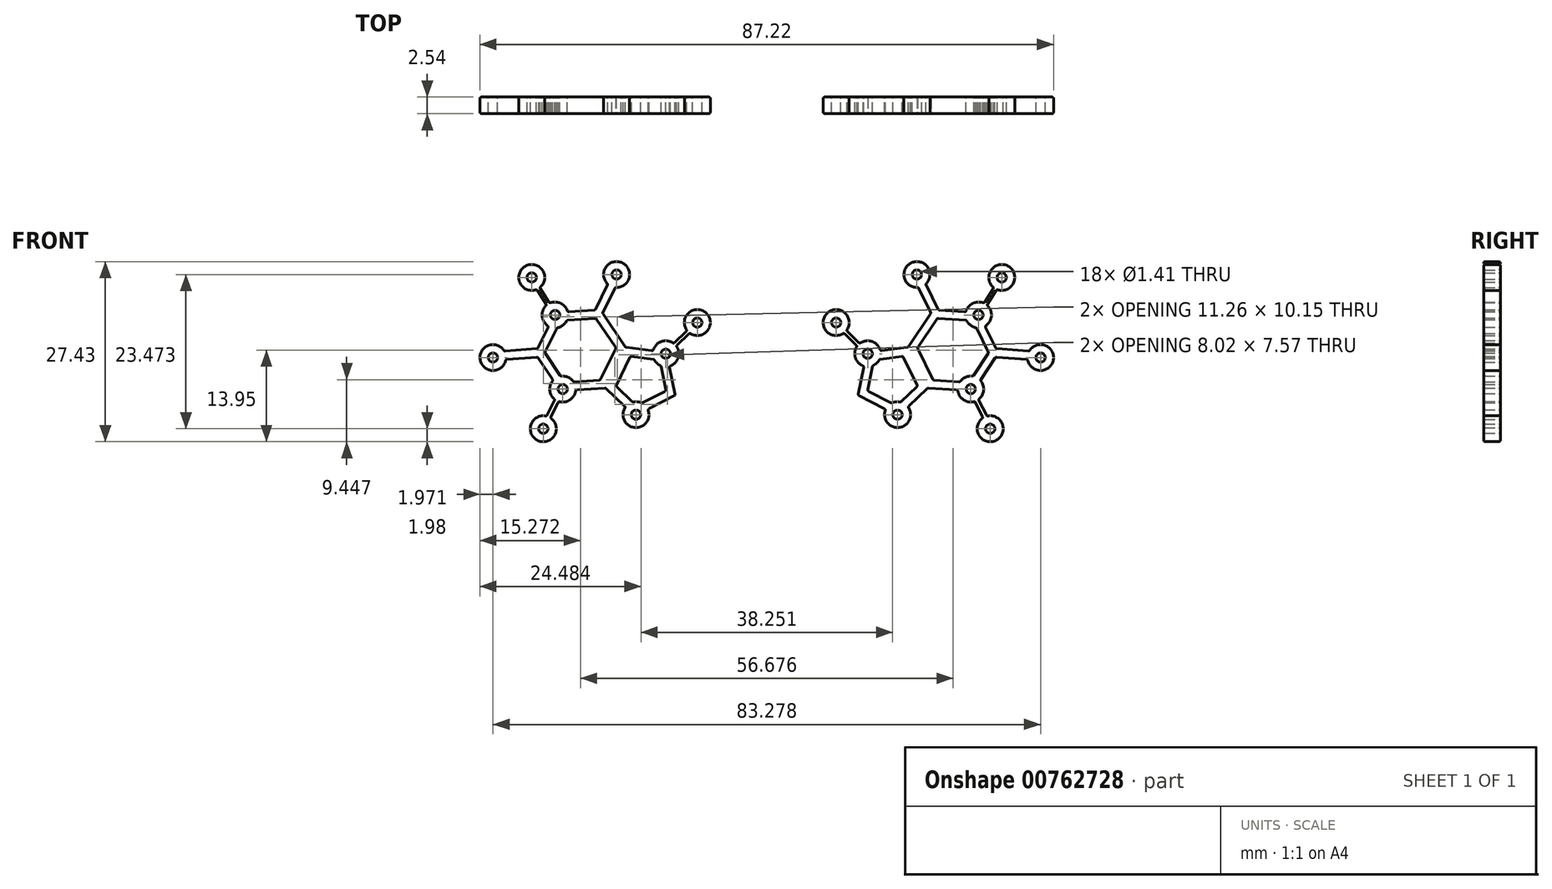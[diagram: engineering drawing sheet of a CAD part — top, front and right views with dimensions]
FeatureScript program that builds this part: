
annotation { "Feature Type Name" : "Feature", "Feature Type Description" : "" }
export const myFeature = defineFeature(function(context is Context, id is Id, definition is map)
    precondition{}
    {
        {
            var Q0;
            Q0=qCreatedBy(makeId("Front.planeOp"),FACE);
            var sketch = newSketch(context, id + "F0", { "sketchPlane" : qUnion([Q0])});
            skLineSegment(sketch, "E0.1", {"start": v(-24.49, 20.36) * mm, "end": v(-29.05, 20.05) * mm});
            skLineSegment(sketch, "E0.2", {"start": v(-32.47, 21.54) * mm, "end": v(-34.85, 25.07) * mm});
            skLineSegment(sketch, "E0.3", {"start": v(-34.85, 26.35) * mm, "end": v(-33.18, 29.77) * mm});
            skLineSegment(sketch, "E0.4", {"start": v(-30.27, 31.94) * mm, "end": v(-26.12, 32.22) * mm});
            skLineSegment(sketch, "E0.5", {"start": v(-24.98, 31.78) * mm, "end": v(-21.46, 26.56) * mm});
            skPoint(sketch, "E0.0.midPoint", {"position": v(-22.97, 23.46) * mm});
            skLineSegment(sketch, "E1", {"start": v(-24.49, 20.36) * mm, "end": v(-21.46, 17.5) * mm});
            skLineSegment(sketch, "E2", {"start": v(-21.46, 26.56) * mm, "end": v(-17.28, 26.01) * mm});
            skLineSegment(sketch, "E3", {"start": v(-14.8, 23.68) * mm, "end": v(-13.9, 19.26) * mm});
            skLineSegment(sketch, "E4", {"start": v(-13.9, 19.26) * mm, "end": v(-18.09, 17.1) * mm});
            skPoint(sketch, "E5.third.point", {"position": v(-19.84, 14.33) * mm});
            skArc(sketch, "E6", {"start": v(-14.8, 23.68) * mm, "mid": v(-13.48, 24.95) * mm, "end": v(-13.77, 26.75) * mm});
            skArc(sketch, "E7", {"start": v(-33.48, 16.07) * mm, "mid": v(-34.78, 12.35) * mm, "end": v(-32.9, 15.81) * mm});
            skArc(sketch, "E8", {"start": v(-39.92, 25.97) * mm, "mid": v(-43.58, 24.63) * mm, "end": v(-39.69, 24.7) * mm});
            skArc(sketch, "E9", {"start": v(-30.27, 31.94) * mm, "mid": v(-33.37, 33.06) * mm, "end": v(-33.18, 29.77) * mm});
            skArc(sketch, "E10", {"start": v(-23.05, 35.67) * mm, "mid": v(-22.02, 39.43) * mm, "end": v(-24.16, 36.17) * mm});
            skArc(sketch, "E11", {"start": v(-34.55, 35.6) * mm, "mid": v(-36.71, 38.9) * mm, "end": v(-35, 35.36) * mm});
            skArc(sketch, "E12", {"start": v(-11.72, 28.73) * mm, "mid": v(-9.19, 31.75) * mm, "end": v(-12.1, 29.1) * mm});
            skLineSegment(sketch, "E13", {"start": v(-26.12, 32.22) * mm, "end": v(-24.16, 36.17) * mm});
            skLineSegment(sketch, "E14", {"start": v(-23.05, 35.67) * mm, "end": v(-24.98, 31.78) * mm});
            skLineSegment(sketch, "E15", {"start": v(-39.92, 25.97) * mm, "end": v(-34.85, 26.35) * mm});
            skLineSegment(sketch, "E16", {"start": v(-39.69, 24.7) * mm, "end": v(-34.85, 25.07) * mm});
            skLineSegment(sketch, "E17", {"start": v(-33.48, 16.07) * mm, "end": v(-32.2, 18.6) * mm});
            skLineSegment(sketch, "E18", {"start": v(-32.9, 15.81) * mm, "end": v(-31.67, 18.33) * mm});
            skLineSegment(sketch, "E19", {"start": v(-35, 35.36) * mm, "end": v(-33.47, 32.97) * mm});
            skLineSegment(sketch, "E20", {"start": v(-34.55, 35.6) * mm, "end": v(-33.02, 33.27) * mm});
            skLineSegment(sketch, "E21", {"start": v(-14.15, 27.14) * mm, "end": v(-12.1, 29.1) * mm});
            skLineSegment(sketch, "E22", {"start": v(-13.77, 26.75) * mm, "end": v(-11.72, 28.73) * mm});
            skPoint(sketch, "E23.orphan", {"position": v(-25.3, 32.28) * mm});
            skArc(sketch, "E24.trimOffspring", {"start": v(-31.67, 18.33) * mm, "mid": v(-29.94, 18.55) * mm, "end": v(-29.05, 20.05) * mm});
            skPoint(sketch, "E25.orphan", {"position": v(-32.19, 31.8) * mm});
            skCircle(sketch, "E26", {"center": v(-41.64, 25) * mm, "radius": 0.7 * mm});
            skCircle(sketch, "E27", {"center": v(-33.98, 14.16) * mm, "radius": 0.7 * mm});
            skCircle(sketch, "E28", {"center": v(-31.02, 20.2) * mm, "radius": 0.7 * mm});
            skCircle(sketch, "E29", {"center": v(-19.89, 16.3) * mm, "radius": 0.7 * mm});
            skCircle(sketch, "E30", {"center": v(-15.36, 25.58) * mm, "radius": 0.7 * mm});
            skCircle(sketch, "E31", {"center": v(-10.56, 30.32) * mm, "radius": 0.7 * mm});
            skCircle(sketch, "E32", {"center": v(-22.83, 37.63) * mm, "radius": 0.7 * mm});
            skCircle(sketch, "E33", {"center": v(-35.74, 37.18) * mm, "radius": 0.7 * mm});
            skCircle(sketch, "E34", {"center": v(-32.19, 31.47) * mm, "radius": 0.7 * mm});
            skLineSegment(sketch, "E35.0", {"start": v(-33.71, 25.8) * mm, "end": v(-32.04, 29.21) * mm});
            skLineSegment(sketch, "E36.0", {"start": v(-29.72, 30.7) * mm, "end": v(-26.03, 30.96) * mm});
            skLineSegment(sketch, "E37.0", {"start": v(-25.95, 30.96) * mm, "end": v(-22.92, 26.46) * mm});
            skLineSegment(sketch, "E38.0", {"start": v(-22.92, 26.46) * mm, "end": v(-25.3, 21.58) * mm});
            skLineSegment(sketch, "E39.0", {"start": v(-25.3, 21.58) * mm, "end": v(-29.14, 21.32) * mm});
            skLineSegment(sketch, "E40.0", {"start": v(-31.42, 22.24) * mm, "end": v(-33.75, 25.71) * mm});
            skLineSegment(sketch, "E41", {"start": v(-32.04, 29.21) * mm, "end": v(-31.9, 29.52) * mm});
            skLineSegment(sketch, "E42", {"start": v(-29.72, 30.7) * mm, "end": v(-30.4, 30.66) * mm});
            skLineSegment(sketch, "E43", {"start": v(-26.03, 30.96) * mm, "end": v(-25.95, 30.96) * mm});
            skLineSegment(sketch, "E44", {"start": v(-33.71, 25.8) * mm, "end": v(-33.75, 25.71) * mm});
            skLineSegment(sketch, "E45", {"start": v(-31.42, 22.24) * mm, "end": v(-31.35, 22.14) * mm});
            skLineSegment(sketch, "E46", {"start": v(-29.14, 21.32) * mm, "end": v(-29.39, 21.3) * mm});
            skLineSegment(sketch, "E47.0", {"start": v(-20.72, 25.18) * mm, "end": v(-22.94, 20.64) * mm});
            skLineSegment(sketch, "E48.0", {"start": v(-22.94, 20.64) * mm, "end": v(-20.59, 18.41) * mm});
            skLineSegment(sketch, "E49.0", {"start": v(-15.34, 19.95) * mm, "end": v(-18.67, 18.24) * mm});
            skLineSegment(sketch, "E50.0", {"start": v(-16.07, 23.53) * mm, "end": v(-15.34, 19.95) * mm});
            skLineSegment(sketch, "E51.0", {"start": v(-20.72, 25.18) * mm, "end": v(-17.44, 24.75) * mm});
            skLineSegment(sketch, "E52", {"start": v(-20.59, 18.41) * mm, "end": v(-20.38, 18.21) * mm});
            skLineSegment(sketch, "E53", {"start": v(-18.67, 18.24) * mm, "end": v(-19, 18.06) * mm});
            skLineSegment(sketch, "E54", {"start": v(-17.44, 24.75) * mm, "end": v(-17.13, 24.71) * mm});
            skArc(sketch, "E55.trimOffspring", {"start": v(-31.9, 29.52) * mm, "mid": v(-31, 29.9) * mm, "end": v(-30.4, 30.66) * mm});
            skArc(sketch, "E56", {"start": v(-29.39, 21.3) * mm, "mid": v(-30.25, 22.01) * mm, "end": v(-31.35, 22.14) * mm});
            skArc(sketch, "E57.trimOffspring", {"start": v(-32.47, 21.54) * mm, "mid": v(-33, 20.01) * mm, "end": v(-32.2, 18.6) * mm});
            skArc(sketch, "E58", {"start": v(-17.13, 24.71) * mm, "mid": v(-16.71, 24.14) * mm, "end": v(-16.11, 23.75) * mm});
            skLineSegment(sketch, "E59", {"start": v(-16.07, 23.53) * mm, "end": v(-16.11, 23.75) * mm});
            skArc(sketch, "E60", {"start": v(-21.46, 17.5) * mm, "mid": v(-20.11, 14.34) * mm, "end": v(-18.09, 17.1) * mm});
            skArc(sketch, "E61.trimOffspring", {"start": v(-19, 18.06) * mm, "mid": v(-19.68, 18.26) * mm, "end": v(-20.38, 18.21) * mm});
            skArc(sketch, "E62.trimOffspring", {"start": v(-14.15, 27.14) * mm, "mid": v(-16.02, 27.44) * mm, "end": v(-17.28, 26.01) * mm});
            skCircle(sketch, "E63.MirrorC", {"center": v(19.89, 16.3) * mm, "radius": 0.7 * mm});
            skLineSegment(sketch, "E64.MirrorCS", {"start": v(31.42, 22.24) * mm, "end": v(31.35, 22.14) * mm});
            skArc(sketch, "E65.MirrorCS", {"start": v(19, 18.06) * mm, "mid": v(19.68, 18.26) * mm, "end": v(20.38, 18.21) * mm});
            skLineSegment(sketch, "E66.MirrorCS", {"start": v(33.71, 25.8) * mm, "end": v(33.75, 25.71) * mm});
            skLineSegment(sketch, "E67.MirrorCS", {"start": v(20.59, 18.41) * mm, "end": v(20.38, 18.21) * mm});
            skLineSegment(sketch, "E68.MirrorCS", {"start": v(29.72, 30.7) * mm, "end": v(30.4, 30.66) * mm});
            skLineSegment(sketch, "E69.MirrorCS", {"start": v(32.04, 29.21) * mm, "end": v(31.9, 29.52) * mm});
            skLineSegment(sketch, "E70.MirrorCS", {"start": v(18.67, 18.24) * mm, "end": v(19, 18.06) * mm});
            skLineSegment(sketch, "E71.MirrorCS", {"start": v(29.14, 21.32) * mm, "end": v(29.39, 21.3) * mm});
            skLineSegment(sketch, "E72.MirrorCS", {"start": v(26.03, 30.96) * mm, "end": v(25.95, 30.96) * mm});
            skLineSegment(sketch, "E73.MirrorCS", {"start": v(17.44, 24.75) * mm, "end": v(17.13, 24.71) * mm});
            skArc(sketch, "E74.MirrorCS", {"start": v(30.27, 31.94) * mm, "mid": v(33.37, 33.06) * mm, "end": v(33.18, 29.77) * mm});
            skLineSegment(sketch, "E75.MirrorCS", {"start": v(30.27, 31.94) * mm, "end": v(26.12, 32.22) * mm});
            skLineSegment(sketch, "E76.MirrorCS", {"start": v(34.85, 26.35) * mm, "end": v(33.18, 29.77) * mm});
            skLineSegment(sketch, "E77.MirrorCS", {"start": v(29.72, 30.7) * mm, "end": v(26.03, 30.96) * mm});
            skCircle(sketch, "E78.MirrorC", {"center": v(31.02, 20.2) * mm, "radius": 0.7 * mm});
            skLineSegment(sketch, "E79.MirrorCS", {"start": v(33.71, 25.8) * mm, "end": v(32.04, 29.21) * mm});
            skLineSegment(sketch, "E80.MirrorCS", {"start": v(31.42, 22.24) * mm, "end": v(33.75, 25.71) * mm});
            skLineSegment(sketch, "E81.MirrorCS", {"start": v(22.94, 20.64) * mm, "end": v(20.59, 18.41) * mm});
            skArc(sketch, "E82.MirrorCS", {"start": v(32.47, 21.54) * mm, "mid": v(33, 20.01) * mm, "end": v(32.2, 18.6) * mm});
            skArc(sketch, "E83.MirrorCS", {"start": v(14.15, 27.14) * mm, "mid": v(16.02, 27.44) * mm, "end": v(17.28, 26.01) * mm});
            skLineSegment(sketch, "E84.MirrorCS", {"start": v(16.07, 23.53) * mm, "end": v(16.11, 23.75) * mm});
            skArc(sketch, "E85.MirrorCS", {"start": v(17.13, 24.71) * mm, "mid": v(16.71, 24.14) * mm, "end": v(16.11, 23.75) * mm});
            skCircle(sketch, "E86.MirrorC", {"center": v(32.19, 31.47) * mm, "radius": 0.7 * mm});
            skArc(sketch, "E87.MirrorCS", {"start": v(31.67, 18.33) * mm, "mid": v(29.94, 18.55) * mm, "end": v(29.05, 20.05) * mm});
            skArc(sketch, "E88.MirrorCS", {"start": v(29.39, 21.3) * mm, "mid": v(30.25, 22.01) * mm, "end": v(31.35, 22.14) * mm});
            skArc(sketch, "E89.MirrorCS", {"start": v(31.9, 29.52) * mm, "mid": v(31, 29.9) * mm, "end": v(30.4, 30.66) * mm});
            skLineSegment(sketch, "E90.MirrorCS", {"start": v(32.47, 21.54) * mm, "end": v(34.85, 25.07) * mm});
            skCircle(sketch, "E91.MirrorC", {"center": v(15.36, 25.58) * mm, "radius": 0.7 * mm});
            skArc(sketch, "E92.MirrorCS", {"start": v(14.8, 23.68) * mm, "mid": v(13.48, 24.95) * mm, "end": v(13.77, 26.75) * mm});
            skLineSegment(sketch, "E93.MirrorCS", {"start": v(13.77, 26.75) * mm, "end": v(11.72, 28.73) * mm});
            skLineSegment(sketch, "E94.MirrorCS", {"start": v(14.15, 27.14) * mm, "end": v(12.1, 29.1) * mm});
            skLineSegment(sketch, "E95.MirrorCS", {"start": v(35, 35.36) * mm, "end": v(33.47, 32.97) * mm});
            skLineSegment(sketch, "E96.MirrorCS", {"start": v(20.72, 25.18) * mm, "end": v(17.44, 24.75) * mm});
            skArc(sketch, "E97.MirrorCS", {"start": v(21.46, 17.5) * mm, "mid": v(20.11, 14.34) * mm, "end": v(18.09, 17.1) * mm});
            skLineSegment(sketch, "E98.MirrorCS", {"start": v(16.07, 23.53) * mm, "end": v(15.34, 19.95) * mm});
            skCircle(sketch, "E99.MirrorC", {"center": v(10.56, 30.32) * mm, "radius": 0.7 * mm});
            skLineSegment(sketch, "E100.MirrorCS", {"start": v(34.55, 35.6) * mm, "end": v(33.02, 33.27) * mm});
            skLineSegment(sketch, "E101.MirrorCS", {"start": v(22.92, 26.46) * mm, "end": v(25.3, 21.58) * mm});
            skLineSegment(sketch, "E102.MirrorCS", {"start": v(13.9, 19.26) * mm, "end": v(18.09, 17.1) * mm});
            skLineSegment(sketch, "E103.MirrorCS", {"start": v(21.46, 26.56) * mm, "end": v(17.28, 26.01) * mm});
            skLineSegment(sketch, "E104.MirrorCS", {"start": v(24.49, 20.36) * mm, "end": v(21.46, 17.5) * mm});
            skLineSegment(sketch, "E105.MirrorCS", {"start": v(24.98, 31.78) * mm, "end": v(21.46, 26.56) * mm});
            skLineSegment(sketch, "E106.MirrorCS", {"start": v(15.34, 19.95) * mm, "end": v(18.67, 18.24) * mm});
            skCircle(sketch, "E107.MirrorC", {"center": v(22.83, 37.63) * mm, "radius": 0.7 * mm});
            skLineSegment(sketch, "E108.MirrorCS", {"start": v(23.05, 35.67) * mm, "end": v(24.98, 31.78) * mm});
            skLineSegment(sketch, "E109.MirrorCS", {"start": v(20.72, 25.18) * mm, "end": v(22.94, 20.64) * mm});
            skLineSegment(sketch, "E110.MirrorCS", {"start": v(25.95, 30.96) * mm, "end": v(22.92, 26.46) * mm});
            skLineSegment(sketch, "E111.MirrorCS", {"start": v(25.3, 21.58) * mm, "end": v(29.14, 21.32) * mm});
            skLineSegment(sketch, "E112.MirrorCS", {"start": v(26.12, 32.22) * mm, "end": v(24.16, 36.17) * mm});
            skLineSegment(sketch, "E113.MirrorCS", {"start": v(14.8, 23.68) * mm, "end": v(13.9, 19.26) * mm});
            skLineSegment(sketch, "E114.MirrorCS", {"start": v(24.49, 20.36) * mm, "end": v(29.05, 20.05) * mm});
            skLineSegment(sketch, "E115.MirrorCS", {"start": v(32.9, 15.81) * mm, "end": v(31.67, 18.33) * mm});
            skLineSegment(sketch, "E116.MirrorCS", {"start": v(33.48, 16.07) * mm, "end": v(32.2, 18.6) * mm});
            skArc(sketch, "E117.MirrorCS", {"start": v(39.92, 25.97) * mm, "mid": v(43.58, 24.63) * mm, "end": v(39.69, 24.7) * mm});
            skArc(sketch, "E118.MirrorCS", {"start": v(33.48, 16.07) * mm, "mid": v(34.78, 12.35) * mm, "end": v(32.9, 15.81) * mm});
            skLineSegment(sketch, "E119.MirrorCS", {"start": v(39.69, 24.7) * mm, "end": v(34.85, 25.07) * mm});
            skLineSegment(sketch, "E120.MirrorCS", {"start": v(39.92, 25.97) * mm, "end": v(34.85, 26.35) * mm});
            skArc(sketch, "E121.MirrorCS", {"start": v(11.72, 28.73) * mm, "mid": v(9.19, 31.75) * mm, "end": v(12.1, 29.1) * mm});
            skArc(sketch, "E122.MirrorCS", {"start": v(23.05, 35.67) * mm, "mid": v(22.02, 39.43) * mm, "end": v(24.16, 36.17) * mm});
            skCircle(sketch, "E123.MirrorC", {"center": v(33.98, 14.16) * mm, "radius": 0.7 * mm});
            skArc(sketch, "E124.MirrorCS", {"start": v(34.55, 35.6) * mm, "mid": v(36.71, 38.9) * mm, "end": v(35, 35.36) * mm});
            skCircle(sketch, "E125.MirrorC", {"center": v(41.64, 25) * mm, "radius": 0.7 * mm});
            skCircle(sketch, "E126.MirrorC", {"center": v(35.74, 37.18) * mm, "radius": 0.7 * mm});
            skPoint(sketch, "E127.MirrorP", {"position": v(22.97, 23.46) * mm});
            skPoint(sketch, "E128.MirrorP", {"position": v(32.19, 31.8) * mm});
            skPoint(sketch, "E129.MirrorP", {"position": v(19.84, 14.33) * mm});
            skPoint(sketch, "E130.MirrorP", {"position": v(25.3, 32.28) * mm});
            skSolve(sketch);
        }
        {
            var Q0;
            Q0 = qSketchRegion(id + "F0", true);
            extrude(context, id + "F1", {"entities" : qUnion([Q0]), "depth" : 2.54 * mm, "offsetDistance" : 25.4 * mm});
        }
        {
            var Q0;
            Q0 = qSketchRegion(id + "F0", true);
            extrude(context, id + "F2", {"entities" : qUnion([Q0]), "depth" : 2.54 * mm, "offsetDistance" : 25.4 * mm});
        }
        {
            var Q0;
            Q0=makeQuery(id+"F1.opExtrude","SWEPT_FACE",FACE,{"disambiguationData":[OSD([sQuery(id+"F0.wireOp",EDGE,"E83.MirrorCS")])]});
            var Q1;
            Q1=makeQuery(id+"F1.opExtrude","SWEPT_FACE",FACE,{"disambiguationData":[OSD([sQuery(id+"F0.wireOp",EDGE,"E126.MirrorC")])]});
            var Q2;
            Q2=makeQuery(id+"F1.opExtrude","SWEPT_FACE",FACE,{"disambiguationData":[OSD([sQuery(id+"F0.wireOp",EDGE,"E108.MirrorCS")])]});
            var Q3;
            Q3=makeQuery(id+"F1.opExtrude","SWEPT_FACE",FACE,{"disambiguationData":[OSD([sQuery(id+"F0.wireOp",EDGE,"E67.MirrorCS"),sQuery(id+"F0.wireOp",EDGE,"E81.MirrorCS")])]});
            var Q4;
            Q4=makeQuery(id+"F1.opExtrude","SWEPT_FACE",FACE,{"disambiguationData":[OSD([sQuery(id+"F0.wireOp",EDGE,"E112.MirrorCS")])]});
            var Q5;
            Q5=makeQuery(id+"F1.opExtrude","SWEPT_FACE",FACE,{"disambiguationData":[OSD([sQuery(id+"F0.wireOp",EDGE,"E116.MirrorCS")])]});
            var Q6;
            Q6=makeQuery(id+"F1.opExtrude","SWEPT_FACE",FACE,{"disambiguationData":[OSD([sQuery(id+"F0.wireOp",EDGE,"E90.MirrorCS")])]});
            var Q7;
            Q7=makeQuery(id+"F1.opExtrude","SWEPT_FACE",FACE,{"disambiguationData":[OSD([sQuery(id+"F0.wireOp",EDGE,"E107.MirrorC")])]});
            var Q8;
            Q8=makeQuery(id+"F1.opExtrude","SWEPT_FACE",FACE,{"disambiguationData":[OSD([sQuery(id+"F0.wireOp",EDGE,"E76.MirrorCS")])]});
            var Q9;
            Q9=makeQuery(id+"F1.opExtrude","SWEPT_FACE",FACE,{"disambiguationData":[OSD([sQuery(id+"F0.wireOp",EDGE,"E89.MirrorCS")])]});
            var Q10;
            Q10=makeQuery(id+"F1.opExtrude","SWEPT_FACE",FACE,{"disambiguationData":[OSD([sQuery(id+"F0.wireOp",EDGE,"E125.MirrorC")])]});
            var Q11;
            Q11=makeQuery(id+"F1.opExtrude","CAP_EDGE",EDGE,{"disambiguationData":[OSD([sQuery(id+"F0.wireOp",EDGE,"E69.MirrorCS"),sQuery(id+"F0.wireOp",EDGE,"E79.MirrorCS"),sQuery(id+"F0.wireOp",EDGE,"E66.MirrorCS")])],"isStart":false});
            var Q12;
            Q12=makeQuery(id+"F1.opExtrude","CAP_EDGE",EDGE,{"disambiguationData":[OSD([sQuery(id+"F0.wireOp",EDGE,"E102.MirrorCS")])],"isStart":false});
            var Q13;
            Q13=makeQuery(id+"F1.opExtrude","SWEPT_FACE",FACE,{"disambiguationData":[OSD([sQuery(id+"F0.wireOp",EDGE,"E69.MirrorCS"),sQuery(id+"F0.wireOp",EDGE,"E79.MirrorCS"),sQuery(id+"F0.wireOp",EDGE,"E66.MirrorCS")])]});
            var Q14;
            Q14=makeQuery(id+"F1.opExtrude","SWEPT_FACE",FACE,{"disambiguationData":[OSD([sQuery(id+"F0.wireOp",EDGE,"E92.MirrorCS")])]});
            var Q15;
            Q15=makeQuery(id+"F1.opExtrude","SWEPT_FACE",FACE,{"disambiguationData":[OSD([sQuery(id+"F0.wireOp",EDGE,"E84.MirrorCS"),sQuery(id+"F0.wireOp",EDGE,"E98.MirrorCS")])]});
            var Q16;
            Q16=makeQuery(id+"F1.opExtrude","CAP_EDGE",EDGE,{"disambiguationData":[OSD([sQuery(id+"F0.wireOp",EDGE,"E90.MirrorCS")])],"isStart":false});
            var Q17;
            Q17=makeQuery(id+"F1.opExtrude","SWEPT_FACE",FACE,{"disambiguationData":[OSD([sQuery(id+"F0.wireOp",EDGE,"E119.MirrorCS")])]});
            var Q18;
            Q18=makeQuery(id+"F1.opExtrude","SWEPT_FACE",FACE,{"disambiguationData":[OSD([sQuery(id+"F0.wireOp",EDGE,"E101.MirrorCS")])]});
            var Q19;
            Q19=makeQuery(id+"F1.opExtrude","SWEPT_FACE",FACE,{"disambiguationData":[OSD([sQuery(id+"F0.wireOp",EDGE,"E91.MirrorC")])]});
            var Q20;
            {var subQ0=sQuery(id+"F0.wireOp",EDGE,"E74.MirrorCS");Q20=makeQuery(id+"F1.opExtrude","SWEPT_FACE",FACE,{"disambiguationData":[OSD([subQ0]),TDD([makeQuery(id+"F0.imprint","IMPRINT",EDGE,{"disambiguationData":[TD([[makeQuery(id+"F0.imprint","INTERSECT",VERTEX,{"derivedFrom":[sQuery(id+"F0.wireOp",EDGE,"E75.MirrorCS"),subQ0]}),-1.0]])],"derivedFrom":subQ0})])]});}
            var Q21;
            Q21=makeQuery(id+"F1.opExtrude","SWEPT_FACE",FACE,{"disambiguationData":[OSD([sQuery(id+"F0.wireOp",EDGE,"E93.MirrorCS")])]});
            var Q22;
            Q22=makeQuery(id+"F1.opExtrude","CAP_EDGE",EDGE,{"disambiguationData":[OSD([sQuery(id+"F0.wireOp",EDGE,"E112.MirrorCS")])],"isStart":false});
            var Q23;
            Q23=makeQuery(id+"F1.opExtrude","SWEPT_FACE",FACE,{"disambiguationData":[OSD([sQuery(id+"F0.wireOp",EDGE,"E75.MirrorCS")])]});
            var Q24;
            Q24=makeQuery(id+"F1.opExtrude","CAP_EDGE",EDGE,{"disambiguationData":[OSD([sQuery(id+"F0.wireOp",EDGE,"E109.MirrorCS")])],"isStart":false});
            var Q25;
            Q25=makeQuery(id+"F1.opExtrude","SWEPT_FACE",FACE,{"disambiguationData":[OSD([sQuery(id+"F0.wireOp",EDGE,"E82.MirrorCS")])]});
            var Q26;
            Q26=makeQuery(id+"F1.opExtrude","SWEPT_FACE",FACE,{"disambiguationData":[OSD([sQuery(id+"F0.wireOp",EDGE,"E85.MirrorCS")])]});
            var Q27;
            Q27=makeQuery(id+"F1.opExtrude","SWEPT_FACE",FACE,{"disambiguationData":[OSD([sQuery(id+"F0.wireOp",EDGE,"E63.MirrorC")])]});
            var Q28;
            {var subQ0=sQuery(id+"F0.wireOp",EDGE,"E74.MirrorCS");Q28=makeQuery(id+"F1.opExtrude","SWEPT_FACE",FACE,{"disambiguationData":[OSD([subQ0]),TDD([makeQuery(id+"F0.imprint","IMPRINT",EDGE,{"disambiguationData":[TD([[makeQuery(id+"F0.imprint","INTERSECT",VERTEX,{"derivedFrom":[sQuery(id+"F0.wireOp",EDGE,"E76.MirrorCS"),subQ0]}),1.0]])],"derivedFrom":subQ0})])]});}
            var Q29;
            Q29=makeQuery(id+"F1.opExtrude","CAP_EDGE",EDGE,{"disambiguationData":[OSD([sQuery(id+"F0.wireOp",EDGE,"E105.MirrorCS")])],"isStart":false});
            var Q30;
            Q30=makeQuery(id+"F1.opExtrude","SWEPT_FACE",FACE,{"disambiguationData":[OSD([sQuery(id+"F0.wireOp",EDGE,"E95.MirrorCS")])]});
            var Q31;
            Q31=makeQuery(id+"F1.opExtrude","SWEPT_FACE",FACE,{"disambiguationData":[OSD([sQuery(id+"F0.wireOp",EDGE,"E114.MirrorCS")])]});
            var Q32;
            Q32=makeQuery(id+"F1.opExtrude","SWEPT_FACE",FACE,{"disambiguationData":[OSD([sQuery(id+"F0.wireOp",EDGE,"E110.MirrorCS")])]});
            var Q33;
            Q33=makeQuery(id+"F1.opExtrude","SWEPT_FACE",FACE,{"disambiguationData":[OSD([sQuery(id+"F0.wireOp",EDGE,"E117.MirrorCS")])]});
            var Q34;
            Q34=makeQuery(id+"F1.opExtrude","SWEPT_FACE",FACE,{"disambiguationData":[OSD([sQuery(id+"F0.wireOp",EDGE,"E104.MirrorCS")])]});
            var Q35;
            Q35=makeQuery(id+"F1.opExtrude","SWEPT_FACE",FACE,{"disambiguationData":[OSD([sQuery(id+"F0.wireOp",EDGE,"E78.MirrorC")])]});
            var Q36;
            Q36=makeQuery(id+"F1.opExtrude","SWEPT_FACE",FACE,{"disambiguationData":[OSD([sQuery(id+"F0.wireOp",EDGE,"E80.MirrorCS"),sQuery(id+"F0.wireOp",EDGE,"E64.MirrorCS")])]});
            var Q37;
            Q37=makeQuery(id+"F1.opExtrude","SWEPT_FACE",FACE,{"disambiguationData":[OSD([sQuery(id+"F0.wireOp",EDGE,"E103.MirrorCS")])]});
            var Q38;
            Q38=makeQuery(id+"F1.opExtrude","SWEPT_FACE",FACE,{"disambiguationData":[OSD([sQuery(id+"F0.wireOp",EDGE,"E123.MirrorC")])]});
            var Q39;
            Q39=makeQuery(id+"F1.opExtrude","SWEPT_FACE",FACE,{"disambiguationData":[OSD([sQuery(id+"F0.wireOp",EDGE,"E94.MirrorCS")])]});
            var Q40;
            Q40=makeQuery(id+"F1.opExtrude","SWEPT_FACE",FACE,{"disambiguationData":[OSD([sQuery(id+"F0.wireOp",EDGE,"E109.MirrorCS")])]});
            var Q41;
            Q41=makeQuery(id+"F1.opExtrude","SWEPT_FACE",FACE,{"disambiguationData":[OSD([sQuery(id+"F0.wireOp",EDGE,"E88.MirrorCS")])]});
            var Q42;
            Q42=makeQuery(id+"F1.opExtrude","CAP_EDGE",EDGE,{"disambiguationData":[OSD([sQuery(id+"F0.wireOp",EDGE,"E101.MirrorCS")])],"isStart":false});
            var Q43;
            Q43=makeQuery(id+"F1.opExtrude","SWEPT_FACE",FACE,{"disambiguationData":[OSD([sQuery(id+"F0.wireOp",EDGE,"E97.MirrorCS")])]});
            var Q44;
            Q44=makeQuery(id+"F1.opExtrude","SWEPT_FACE",FACE,{"disambiguationData":[OSD([sQuery(id+"F0.wireOp",EDGE,"E120.MirrorCS")])]});
            var Q45;
            Q45=makeQuery(id+"F1.opExtrude","SWEPT_FACE",FACE,{"disambiguationData":[OSD([sQuery(id+"F0.wireOp",EDGE,"E70.MirrorCS"),sQuery(id+"F0.wireOp",EDGE,"E106.MirrorCS")])]});
            var Q46;
            Q46=makeQuery(id+"F1.opExtrude","SWEPT_FACE",FACE,{"disambiguationData":[OSD([sQuery(id+"F0.wireOp",EDGE,"E105.MirrorCS")])]});
            var Q47;
            Q47=makeQuery(id+"F1.opExtrude","SWEPT_FACE",FACE,{"disambiguationData":[OSD([sQuery(id+"F0.wireOp",EDGE,"E121.MirrorCS")])]});
            var Q48;
            Q48=makeQuery(id+"F1.opExtrude","SWEPT_FACE",FACE,{"disambiguationData":[OSD([sQuery(id+"F0.wireOp",EDGE,"E71.MirrorCS"),sQuery(id+"F0.wireOp",EDGE,"E111.MirrorCS")])]});
            var Q49;
            Q49=makeQuery(id+"F1.opExtrude","SWEPT_FACE",FACE,{"disambiguationData":[OSD([sQuery(id+"F0.wireOp",EDGE,"E122.MirrorCS")])]});
            var Q50;
            Q50=makeQuery(id+"F1.opExtrude","SWEPT_FACE",FACE,{"disambiguationData":[OSD([sQuery(id+"F0.wireOp",EDGE,"E68.MirrorCS"),sQuery(id+"F0.wireOp",EDGE,"E77.MirrorCS"),sQuery(id+"F0.wireOp",EDGE,"E72.MirrorCS")])]});
            var Q51;
            Q51=makeQuery(id+"F1.opExtrude","SWEPT_FACE",FACE,{"disambiguationData":[OSD([sQuery(id+"F0.wireOp",EDGE,"E102.MirrorCS")])]});
            var Q52;
            Q52=makeQuery(id+"F1.opExtrude","SWEPT_FACE",FACE,{"disambiguationData":[OSD([sQuery(id+"F0.wireOp",EDGE,"E86.MirrorC")])]});
            var Q53;
            Q53=makeQuery(id+"F1.opExtrude","SWEPT_FACE",FACE,{"disambiguationData":[OSD([sQuery(id+"F0.wireOp",EDGE,"E113.MirrorCS")])]});
            var Q54;
            Q54=makeQuery(id+"F1.opExtrude","SWEPT_FACE",FACE,{"disambiguationData":[OSD([sQuery(id+"F0.wireOp",EDGE,"E124.MirrorCS")])]});
            var Q55;
            Q55=makeQuery(id+"F1.opExtrude","CAP_FACE",FACE,{"disambiguationData":[OSD([sQuery(id+"F0.wireOp",EDGE,"E73.MirrorCS"),sQuery(id+"F0.wireOp",EDGE,"E68.MirrorCS"),sQuery(id+"F0.wireOp",EDGE,"E69.MirrorCS"),sQuery(id+"F0.wireOp",EDGE,"E89.MirrorCS"),sQuery(id+"F0.wireOp",EDGE,"E77.MirrorCS"),sQuery(id+"F0.wireOp",EDGE,"E67.MirrorCS"),sQuery(id+"F0.wireOp",EDGE,"E84.MirrorCS"),sQuery(id+"F0.wireOp",EDGE,"E85.MirrorCS"),sQuery(id+"F0.wireOp",EDGE,"E72.MirrorCS"),sQuery(id+"F0.wireOp",EDGE,"E91.MirrorC"),sQuery(id+"F0.wireOp",EDGE,"E75.MirrorCS"),sQuery(id+"F0.wireOp",EDGE,"E82.MirrorCS"),sQuery(id+"F0.wireOp",EDGE,"E87.MirrorCS"),sQuery(id+"F0.wireOp",EDGE,"E79.MirrorCS"),sQuery(id+"F0.wireOp",EDGE,"E78.MirrorC"),sQuery(id+"F0.wireOp",EDGE,"E70.MirrorCS"),sQuery(id+"F0.wireOp",EDGE,"E66.MirrorCS"),sQuery(id+"F0.wireOp",EDGE,"E80.MirrorCS"),sQuery(id+"F0.wireOp",EDGE,"E88.MirrorCS"),sQuery(id+"F0.wireOp",EDGE,"E86.MirrorC"),sQuery(id+"F0.wireOp",EDGE,"E65.MirrorCS"),sQuery(id+"F0.wireOp",EDGE,"E71.MirrorCS"),sQuery(id+"F0.wireOp",EDGE,"E83.MirrorCS"),sQuery(id+"F0.wireOp",EDGE,"E90.MirrorCS"),sQuery(id+"F0.wireOp",EDGE,"E76.MirrorCS"),sQuery(id+"F0.wireOp",EDGE,"E92.MirrorCS"),sQuery(id+"F0.wireOp",EDGE,"E63.MirrorC"),sQuery(id+"F0.wireOp",EDGE,"E64.MirrorCS"),sQuery(id+"F0.wireOp",EDGE,"E74.MirrorCS"),sQuery(id+"F0.wireOp",EDGE,"E96.MirrorCS"),sQuery(id+"F0.wireOp",EDGE,"E95.MirrorCS"),sQuery(id+"F0.wireOp",EDGE,"E93.MirrorCS"),sQuery(id+"F0.wireOp",EDGE,"E98.MirrorCS"),sQuery(id+"F0.wireOp",EDGE,"E94.MirrorCS"),sQuery(id+"F0.wireOp",EDGE,"E100.MirrorCS"),sQuery(id+"F0.wireOp",EDGE,"E97.MirrorCS"),sQuery(id+"F0.wireOp",EDGE,"E103.MirrorCS"),sQuery(id+"F0.wireOp",EDGE,"E113.MirrorCS"),sQuery(id+"F0.wireOp",EDGE,"E99.MirrorC"),sQuery(id+"F0.wireOp",EDGE,"E102.MirrorCS"),sQuery(id+"F0.wireOp",EDGE,"E106.MirrorCS"),sQuery(id+"F0.wireOp",EDGE,"E126.MirrorC"),sQuery(id+"F0.wireOp",EDGE,"E125.MirrorC"),sQuery(id+"F0.wireOp",EDGE,"E116.MirrorCS"),sQuery(id+"F0.wireOp",EDGE,"E115.MirrorCS"),sQuery(id+"F0.wireOp",EDGE,"E110.MirrorCS"),sQuery(id+"F0.wireOp",EDGE,"E101.MirrorCS"),sQuery(id+"F0.wireOp",EDGE,"E111.MirrorCS"),sQuery(id+"F0.wireOp",EDGE,"E119.MirrorCS"),sQuery(id+"F0.wireOp",EDGE,"E114.MirrorCS"),sQuery(id+"F0.wireOp",EDGE,"E104.MirrorCS"),sQuery(id+"F0.wireOp",EDGE,"E109.MirrorCS"),sQuery(id+"F0.wireOp",EDGE,"E105.MirrorCS"),sQuery(id+"F0.wireOp",EDGE,"E81.MirrorCS"),sQuery(id+"F0.wireOp",EDGE,"E120.MirrorCS"),sQuery(id+"F0.wireOp",EDGE,"E123.MirrorC"),sQuery(id+"F0.wireOp",EDGE,"E124.MirrorCS"),sQuery(id+"F0.wireOp",EDGE,"E122.MirrorCS"),sQuery(id+"F0.wireOp",EDGE,"E121.MirrorCS"),sQuery(id+"F0.wireOp",EDGE,"E108.MirrorCS"),sQuery(id+"F0.wireOp",EDGE,"E107.MirrorC"),sQuery(id+"F0.wireOp",EDGE,"E112.MirrorCS"),sQuery(id+"F0.wireOp",EDGE,"E118.MirrorCS"),sQuery(id+"F0.wireOp",EDGE,"E117.MirrorCS")])],"isStart":false});
            var Q56;
            Q56=makeQuery(id+"F1.opExtrude","SWEPT_FACE",FACE,{"disambiguationData":[OSD([sQuery(id+"F0.wireOp",EDGE,"E73.MirrorCS"),sQuery(id+"F0.wireOp",EDGE,"E96.MirrorCS")])]});
            var Q57;
            Q57=makeQuery(id+"F1.opExtrude","SWEPT_FACE",FACE,{"disambiguationData":[OSD([sQuery(id+"F0.wireOp",EDGE,"E99.MirrorC")])]});
            var Q58;
            Q58=makeQuery(id+"F1.opExtrude","CAP_EDGE",EDGE,{"disambiguationData":[OSD([sQuery(id+"F0.wireOp",EDGE,"E110.MirrorCS")])],"isStart":false});
            var Q59;
            Q59=makeQuery(id+"F1.opExtrude","SWEPT_FACE",FACE,{"disambiguationData":[OSD([sQuery(id+"F0.wireOp",EDGE,"E100.MirrorCS")])]});
            var Q60;
            Q60=makeQuery(id+"F1.opExtrude","SWEPT_FACE",FACE,{"disambiguationData":[OSD([sQuery(id+"F0.wireOp",EDGE,"E87.MirrorCS")])]});
            var Q61;
            Q61=makeQuery(id+"F1.opExtrude","SWEPT_FACE",FACE,{"disambiguationData":[OSD([sQuery(id+"F0.wireOp",EDGE,"E115.MirrorCS")])]});
            var Q62;
            Q62=makeQuery(id+"F1.opExtrude","SWEPT_FACE",FACE,{"disambiguationData":[OSD([sQuery(id+"F0.wireOp",EDGE,"E118.MirrorCS")])]});
            var Q63;
            Q63=makeQuery(id+"F1.opExtrude","SWEPT_FACE",FACE,{"disambiguationData":[OSD([sQuery(id+"F0.wireOp",EDGE,"E22")])]});
            var Q64;
            Q64=makeQuery(id+"F1.opExtrude","SWEPT_FACE",FACE,{"disambiguationData":[OSD([sQuery(id+"F0.wireOp",EDGE,"E40.0"),sQuery(id+"F0.wireOp",EDGE,"E45")])]});
            var Q65;
            Q65=makeQuery(id+"F1.opExtrude","SWEPT_FACE",FACE,{"disambiguationData":[OSD([sQuery(id+"F0.wireOp",EDGE,"E37.0")])]});
            var Q66;
            Q66=makeQuery(id+"F1.opExtrude","SWEPT_FACE",FACE,{"disambiguationData":[OSD([sQuery(id+"F0.wireOp",EDGE,"E19")])]});
            var Q67;
            Q67=makeQuery(id+"F1.opExtrude","SWEPT_FACE",FACE,{"disambiguationData":[OSD([sQuery(id+"F0.wireOp",EDGE,"E21")])]});
            var Q68;
            Q68=makeQuery(id+"F1.opExtrude","SWEPT_FACE",FACE,{"disambiguationData":[OSD([sQuery(id+"F0.wireOp",EDGE,"E39.0"),sQuery(id+"F0.wireOp",EDGE,"E46")])]});
            var Q69;
            Q69=makeQuery(id+"F1.opExtrude","CAP_EDGE",EDGE,{"disambiguationData":[OSD([sQuery(id+"F0.wireOp",EDGE,"E37.0")])],"isStart":false});
            var Q70;
            Q70=makeQuery(id+"F1.opExtrude","SWEPT_FACE",FACE,{"disambiguationData":[OSD([sQuery(id+"F0.wireOp",EDGE,"E20")])]});
            var Q71;
            Q71=makeQuery(id+"F1.opExtrude","SWEPT_FACE",FACE,{"disambiguationData":[OSD([sQuery(id+"F0.wireOp",EDGE,"E38.0")])]});
            var Q72;
            Q72=makeQuery(id+"F1.opExtrude","SWEPT_FACE",FACE,{"disambiguationData":[OSD([sQuery(id+"F0.wireOp",EDGE,"E61.trimOffspring")])]});
            var Q73;
            Q73=makeQuery(id+"F1.opExtrude","SWEPT_FACE",FACE,{"disambiguationData":[OSD([sQuery(id+"F0.wireOp",EDGE,"E17")])]});
            var Q74;
            Q74=makeQuery(id+"F1.opExtrude","SWEPT_FACE",FACE,{"disambiguationData":[OSD([sQuery(id+"F0.wireOp",EDGE,"E35.0"),sQuery(id+"F0.wireOp",EDGE,"E41"),sQuery(id+"F0.wireOp",EDGE,"E44")])]});
            var Q75;
            Q75=makeQuery(id+"F1.opExtrude","SWEPT_FACE",FACE,{"disambiguationData":[OSD([sQuery(id+"F0.wireOp",EDGE,"E16")])]});
            var Q76;
            Q76=makeQuery(id+"F1.opExtrude","SWEPT_FACE",FACE,{"disambiguationData":[OSD([sQuery(id+"F0.wireOp",EDGE,"E34")])]});
            var Q77;
            Q77=makeQuery(id+"F1.opExtrude","SWEPT_FACE",FACE,{"disambiguationData":[OSD([sQuery(id+"F0.wireOp",EDGE,"E60")])]});
            var Q78;
            Q78=makeQuery(id+"F1.opExtrude","SWEPT_FACE",FACE,{"disambiguationData":[OSD([sQuery(id+"F0.wireOp",EDGE,"E62.trimOffspring")])]});
            var Q79;
            Q79=makeQuery(id+"F1.opExtrude","SWEPT_FACE",FACE,{"disambiguationData":[OSD([sQuery(id+"F0.wireOp",EDGE,"E18")])]});
            var Q80;
            Q80=makeQuery(id+"F1.opExtrude","SWEPT_FACE",FACE,{"disambiguationData":[OSD([sQuery(id+"F0.wireOp",EDGE,"E36.0"),sQuery(id+"F0.wireOp",EDGE,"E42"),sQuery(id+"F0.wireOp",EDGE,"E43")])]});
            var Q81;
            Q81=makeQuery(id+"F1.opExtrude","SWEPT_FACE",FACE,{"disambiguationData":[OSD([sQuery(id+"F0.wireOp",EDGE,"E32")])]});
            var Q82;
            Q82=makeQuery(id+"F1.opExtrude","SWEPT_FACE",FACE,{"disambiguationData":[OSD([sQuery(id+"F0.wireOp",EDGE,"E57.trimOffspring")])]});
            var Q83;
            Q83=makeQuery(id+"F1.opExtrude","SWEPT_FACE",FACE,{"disambiguationData":[OSD([sQuery(id+"F0.wireOp",EDGE,"E14")])]});
            var Q84;
            Q84=makeQuery(id+"F1.opExtrude","SWEPT_FACE",FACE,{"disambiguationData":[OSD([sQuery(id+"F0.wireOp",EDGE,"E15")])]});
            var Q85;
            Q85=makeQuery(id+"F1.opExtrude","SWEPT_FACE",FACE,{"disambiguationData":[OSD([sQuery(id+"F0.wireOp",EDGE,"E33")])]});
            var Q86;
            Q86=makeQuery(id+"F1.opExtrude","SWEPT_FACE",FACE,{"disambiguationData":[OSD([sQuery(id+"F0.wireOp",EDGE,"E58")])]});
            var Q87;
            Q87=makeQuery(id+"F1.opExtrude","SWEPT_FACE",FACE,{"disambiguationData":[OSD([sQuery(id+"F0.wireOp",EDGE,"E13")])]});
            var Q88;
            Q88=makeQuery(id+"F1.opExtrude","SWEPT_FACE",FACE,{"disambiguationData":[OSD([sQuery(id+"F0.wireOp",EDGE,"E31")])]});
            var Q89;
            Q89=makeQuery(id+"F1.opExtrude","SWEPT_FACE",FACE,{"disambiguationData":[OSD([sQuery(id+"F0.wireOp",EDGE,"E56")])]});
            var Q90;
            Q90=makeQuery(id+"F1.opExtrude","CAP_EDGE",EDGE,{"disambiguationData":[OSD([sQuery(id+"F0.wireOp",EDGE,"E0.3")])],"isStart":false});
            var Q91;
            Q91=makeQuery(id+"F1.opExtrude","SWEPT_FACE",FACE,{"disambiguationData":[OSD([sQuery(id+"F0.wireOp",EDGE,"E50.0"),sQuery(id+"F0.wireOp",EDGE,"E59")])]});
            var Q92;
            Q92=makeQuery(id+"F1.opExtrude","SWEPT_FACE",FACE,{"disambiguationData":[OSD([sQuery(id+"F0.wireOp",EDGE,"E28")])]});
            var Q93;
            Q93=makeQuery(id+"F1.opExtrude","CAP_EDGE",EDGE,{"disambiguationData":[OSD([sQuery(id+"F0.wireOp",EDGE,"E14")])],"isStart":false});
            var Q94;
            Q94=makeQuery(id+"F1.opExtrude","CAP_EDGE",EDGE,{"disambiguationData":[OSD([sQuery(id+"F0.wireOp",EDGE,"E40.0"),sQuery(id+"F0.wireOp",EDGE,"E45")])],"isStart":false});
            var Q95;
            Q95=makeQuery(id+"F1.opExtrude","SWEPT_FACE",FACE,{"disambiguationData":[OSD([sQuery(id+"F0.wireOp",EDGE,"E10")])]});
            var Q96;
            Q96=makeQuery(id+"F1.opExtrude","SWEPT_FACE",FACE,{"disambiguationData":[OSD([sQuery(id+"F0.wireOp",EDGE,"E12")])]});
            var Q97;
            Q97=makeQuery(id+"F1.opExtrude","SWEPT_FACE",FACE,{"disambiguationData":[OSD([sQuery(id+"F0.wireOp",EDGE,"E30")])]});
            var Q98;
            Q98=makeQuery(id+"F1.opExtrude","SWEPT_FACE",FACE,{"disambiguationData":[OSD([sQuery(id+"F0.wireOp",EDGE,"E55.trimOffspring")])]});
            var Q99;
            Q99=makeQuery(id+"F1.opExtrude","SWEPT_FACE",FACE,{"disambiguationData":[OSD([sQuery(id+"F0.wireOp",EDGE,"E29")])]});
            var Q100;
            Q100=makeQuery(id+"F1.opExtrude","SWEPT_FACE",FACE,{"disambiguationData":[OSD([sQuery(id+"F0.wireOp",EDGE,"E51.0"),sQuery(id+"F0.wireOp",EDGE,"E54")])]});
            var Q101;
            Q101=makeQuery(id+"F1.opExtrude","SWEPT_FACE",FACE,{"disambiguationData":[OSD([sQuery(id+"F0.wireOp",EDGE,"E11")])]});
            var Q102;
            Q102=makeQuery(id+"F1.opExtrude","SWEPT_FACE",FACE,{"disambiguationData":[OSD([sQuery(id+"F0.wireOp",EDGE,"E26")])]});
            var Q103;
            Q103=makeQuery(id+"F1.opExtrude","SWEPT_FACE",FACE,{"disambiguationData":[OSD([sQuery(id+"F0.wireOp",EDGE,"E48.0"),sQuery(id+"F0.wireOp",EDGE,"E52")])]});
            var Q104;
            Q104=makeQuery(id+"F1.opExtrude","SWEPT_FACE",FACE,{"disambiguationData":[OSD([sQuery(id+"F0.wireOp",EDGE,"E24.trimOffspring")])]});
            var Q105;
            Q105=makeQuery(id+"F1.opExtrude","SWEPT_FACE",FACE,{"disambiguationData":[OSD([sQuery(id+"F0.wireOp",EDGE,"E47.0")])]});
            var Q106;
            Q106=makeQuery(id+"F1.opExtrude","SWEPT_FACE",FACE,{"disambiguationData":[OSD([sQuery(id+"F0.wireOp",EDGE,"E2")])]});
            var Q107;
            Q107=makeQuery(id+"F1.opExtrude","SWEPT_FACE",FACE,{"disambiguationData":[OSD([sQuery(id+"F0.wireOp",EDGE,"E3")])]});
            var Q108;
            Q108=makeQuery(id+"F1.opExtrude","SWEPT_FACE",FACE,{"disambiguationData":[OSD([sQuery(id+"F0.wireOp",EDGE,"E1")])]});
            var Q109;
            Q109=makeQuery(id+"F1.opExtrude","SWEPT_FACE",FACE,{"disambiguationData":[OSD([sQuery(id+"F0.wireOp",EDGE,"E0.3")])]});
            var Q110;
            Q110=makeQuery(id+"F1.opExtrude","SWEPT_FACE",FACE,{"disambiguationData":[OSD([sQuery(id+"F0.wireOp",EDGE,"E0.1")])]});
            var Q111;
            Q111=makeQuery(id+"F1.opExtrude","CAP_FACE",FACE,{"disambiguationData":[OSD([sQuery(id+"F0.wireOp",EDGE,"E0.1"),sQuery(id+"F0.wireOp",EDGE,"E0.2"),sQuery(id+"F0.wireOp",EDGE,"E0.3"),sQuery(id+"F0.wireOp",EDGE,"E0.4"),sQuery(id+"F0.wireOp",EDGE,"E0.5"),sQuery(id+"F0.wireOp",EDGE,"E1"),sQuery(id+"F0.wireOp",EDGE,"E2"),sQuery(id+"F0.wireOp",EDGE,"E3"),sQuery(id+"F0.wireOp",EDGE,"E4"),sQuery(id+"F0.wireOp",EDGE,"E6"),sQuery(id+"F0.wireOp",EDGE,"E7"),sQuery(id+"F0.wireOp",EDGE,"E8"),sQuery(id+"F0.wireOp",EDGE,"E9"),sQuery(id+"F0.wireOp",EDGE,"E10"),sQuery(id+"F0.wireOp",EDGE,"E11"),sQuery(id+"F0.wireOp",EDGE,"E12"),sQuery(id+"F0.wireOp",EDGE,"E13"),sQuery(id+"F0.wireOp",EDGE,"E14"),sQuery(id+"F0.wireOp",EDGE,"E15"),sQuery(id+"F0.wireOp",EDGE,"E16"),sQuery(id+"F0.wireOp",EDGE,"E17"),sQuery(id+"F0.wireOp",EDGE,"E18"),sQuery(id+"F0.wireOp",EDGE,"E19"),sQuery(id+"F0.wireOp",EDGE,"E20"),sQuery(id+"F0.wireOp",EDGE,"E21"),sQuery(id+"F0.wireOp",EDGE,"E22"),sQuery(id+"F0.wireOp",EDGE,"E24.trimOffspring"),sQuery(id+"F0.wireOp",EDGE,"E26"),sQuery(id+"F0.wireOp",EDGE,"E27"),sQuery(id+"F0.wireOp",EDGE,"E28"),sQuery(id+"F0.wireOp",EDGE,"E29"),sQuery(id+"F0.wireOp",EDGE,"E30"),sQuery(id+"F0.wireOp",EDGE,"E31"),sQuery(id+"F0.wireOp",EDGE,"E32"),sQuery(id+"F0.wireOp",EDGE,"E33"),sQuery(id+"F0.wireOp",EDGE,"E34"),sQuery(id+"F0.wireOp",EDGE,"E35.0"),sQuery(id+"F0.wireOp",EDGE,"E36.0"),sQuery(id+"F0.wireOp",EDGE,"E37.0"),sQuery(id+"F0.wireOp",EDGE,"E38.0"),sQuery(id+"F0.wireOp",EDGE,"E39.0"),sQuery(id+"F0.wireOp",EDGE,"E40.0"),sQuery(id+"F0.wireOp",EDGE,"E41"),sQuery(id+"F0.wireOp",EDGE,"E42"),sQuery(id+"F0.wireOp",EDGE,"E43"),sQuery(id+"F0.wireOp",EDGE,"E44"),sQuery(id+"F0.wireOp",EDGE,"E45"),sQuery(id+"F0.wireOp",EDGE,"E46"),sQuery(id+"F0.wireOp",EDGE,"E47.0"),sQuery(id+"F0.wireOp",EDGE,"E48.0"),sQuery(id+"F0.wireOp",EDGE,"E49.0"),sQuery(id+"F0.wireOp",EDGE,"E50.0"),sQuery(id+"F0.wireOp",EDGE,"E51.0"),sQuery(id+"F0.wireOp",EDGE,"E52"),sQuery(id+"F0.wireOp",EDGE,"E53"),sQuery(id+"F0.wireOp",EDGE,"E54"),sQuery(id+"F0.wireOp",EDGE,"E55.trimOffspring"),sQuery(id+"F0.wireOp",EDGE,"E56"),sQuery(id+"F0.wireOp",EDGE,"E57.trimOffspring"),sQuery(id+"F0.wireOp",EDGE,"E58"),sQuery(id+"F0.wireOp",EDGE,"E59"),sQuery(id+"F0.wireOp",EDGE,"E60"),sQuery(id+"F0.wireOp",EDGE,"E61.trimOffspring"),sQuery(id+"F0.wireOp",EDGE,"E62.trimOffspring")])],"isStart":false});
            var Q112;
            {var subQ0=sQuery(id+"F0.wireOp",EDGE,"E9");Q112=makeQuery(id+"F1.opExtrude","SWEPT_FACE",FACE,{"disambiguationData":[OSD([subQ0]),TDD([makeQuery(id+"F0.imprint","IMPRINT",EDGE,{"disambiguationData":[TD([[makeQuery(id+"F0.imprint","INTERSECT",VERTEX,{"derivedFrom":[sQuery(id+"F0.wireOp",EDGE,"E0.4"),subQ0]}),-1.0]])],"derivedFrom":subQ0})])]});}
            var Q113;
            Q113=makeQuery(id+"F1.opExtrude","SWEPT_FACE",FACE,{"disambiguationData":[OSD([sQuery(id+"F0.wireOp",EDGE,"E0.4")])]});
            var Q114;
            Q114=makeQuery(id+"F1.opExtrude","SWEPT_FACE",FACE,{"disambiguationData":[OSD([sQuery(id+"F0.wireOp",EDGE,"E0.5")])]});
            var Q115;
            Q115=makeQuery(id+"F1.opExtrude","SWEPT_FACE",FACE,{"disambiguationData":[OSD([sQuery(id+"F0.wireOp",EDGE,"E0.2")])]});
            var Q116;
            Q116=makeQuery(id+"F1.opExtrude","SWEPT_FACE",FACE,{"disambiguationData":[OSD([sQuery(id+"F0.wireOp",EDGE,"E8")])]});
            var Q117;
            {var subQ0=sQuery(id+"F0.wireOp",EDGE,"E9");Q117=makeQuery(id+"F1.opExtrude","SWEPT_FACE",FACE,{"disambiguationData":[OSD([subQ0]),TDD([makeQuery(id+"F0.imprint","IMPRINT",EDGE,{"disambiguationData":[TD([[makeQuery(id+"F0.imprint","INTERSECT",VERTEX,{"derivedFrom":[sQuery(id+"F0.wireOp",EDGE,"E0.3"),subQ0]}),1.0]])],"derivedFrom":subQ0})])]});}
            var Q118;
            Q118=makeQuery(id+"F1.opExtrude","CAP_EDGE",EDGE,{"disambiguationData":[OSD([sQuery(id+"F0.wireOp",EDGE,"E20")])],"isStart":false});
            var Q119;
            Q119=makeQuery(id+"F1.opExtrude","SWEPT_FACE",FACE,{"disambiguationData":[OSD([sQuery(id+"F0.wireOp",EDGE,"E7")])]});
            var Q120;
            Q120=makeQuery(id+"F1.opExtrude","SWEPT_FACE",FACE,{"disambiguationData":[OSD([sQuery(id+"F0.wireOp",EDGE,"E27")])]});
            var Q121;
            Q121=makeQuery(id+"F1.opExtrude","SWEPT_FACE",FACE,{"disambiguationData":[OSD([sQuery(id+"F0.wireOp",EDGE,"E49.0"),sQuery(id+"F0.wireOp",EDGE,"E53")])]});
            var Q122;
            Q122=makeQuery(id+"F1.opExtrude","SWEPT_FACE",FACE,{"disambiguationData":[OSD([sQuery(id+"F0.wireOp",EDGE,"E6")])]});
            var Q123;
            Q123=makeQuery(id+"F1.opExtrude","SWEPT_FACE",FACE,{"disambiguationData":[OSD([sQuery(id+"F0.wireOp",EDGE,"E4")])]});
            var Q124;
            Q124=makeQuery(id+"F1.opExtrude","SWEPT_FACE",FACE,{"disambiguationData":[OSD([sQuery(id+"F0.wireOp",EDGE,"E65.MirrorCS")])]});
            var Q125;
            Q125=makeQuery(id+"F2.opExtrude","SWEPT_FACE",FACE,{"disambiguationData":[OSD([sQuery(id+"F0.wireOp",EDGE,"E58")])]});
            var Q126;
            Q126=makeQuery(id+"F2.opExtrude","SWEPT_FACE",FACE,{"disambiguationData":[OSD([sQuery(id+"F0.wireOp",EDGE,"E37.0")])]});
            var Q127;
            Q127=makeQuery(id+"F2.opExtrude","SWEPT_FACE",FACE,{"disambiguationData":[OSD([sQuery(id+"F0.wireOp",EDGE,"E39.0"),sQuery(id+"F0.wireOp",EDGE,"E46")])]});
            var Q128;
            Q128=makeQuery(id+"F2.opExtrude","CAP_EDGE",EDGE,{"disambiguationData":[OSD([sQuery(id+"F0.wireOp",EDGE,"E37.0")])],"isStart":false});
            var Q129;
            Q129=makeQuery(id+"F2.opExtrude","SWEPT_FACE",FACE,{"disambiguationData":[OSD([sQuery(id+"F0.wireOp",EDGE,"E38.0")])]});
            var Q130;
            Q130=makeQuery(id+"F2.opExtrude","SWEPT_FACE",FACE,{"disambiguationData":[OSD([sQuery(id+"F0.wireOp",EDGE,"E20")])]});
            var Q131;
            Q131=makeQuery(id+"F2.opExtrude","SWEPT_FACE",FACE,{"disambiguationData":[OSD([sQuery(id+"F0.wireOp",EDGE,"E36.0"),sQuery(id+"F0.wireOp",EDGE,"E42"),sQuery(id+"F0.wireOp",EDGE,"E43")])]});
            var Q132;
            Q132=makeQuery(id+"F2.opExtrude","SWEPT_FACE",FACE,{"disambiguationData":[OSD([sQuery(id+"F0.wireOp",EDGE,"E19")])]});
            var Q133;
            Q133=makeQuery(id+"F2.opExtrude","SWEPT_FACE",FACE,{"disambiguationData":[OSD([sQuery(id+"F0.wireOp",EDGE,"E62.trimOffspring")])]});
            var Q134;
            Q134=makeQuery(id+"F2.opExtrude","SWEPT_FACE",FACE,{"disambiguationData":[OSD([sQuery(id+"F0.wireOp",EDGE,"E18")])]});
            var Q135;
            Q135=makeQuery(id+"F2.opExtrude","SWEPT_FACE",FACE,{"disambiguationData":[OSD([sQuery(id+"F0.wireOp",EDGE,"E17")])]});
            var Q136;
            Q136=makeQuery(id+"F2.opExtrude","SWEPT_FACE",FACE,{"disambiguationData":[OSD([sQuery(id+"F0.wireOp",EDGE,"E14")])]});
            var Q137;
            Q137=makeQuery(id+"F2.opExtrude","CAP_EDGE",EDGE,{"disambiguationData":[OSD([sQuery(id+"F0.wireOp",EDGE,"E0.3")])],"isStart":false});
            var Q138;
            Q138=makeQuery(id+"F2.opExtrude","CAP_EDGE",EDGE,{"disambiguationData":[OSD([sQuery(id+"F0.wireOp",EDGE,"E14")])],"isStart":false});
            var Q139;
            Q139=makeQuery(id+"F2.opExtrude","CAP_EDGE",EDGE,{"disambiguationData":[OSD([sQuery(id+"F0.wireOp",EDGE,"E40.0"),sQuery(id+"F0.wireOp",EDGE,"E45")])],"isStart":false});
            var Q140;
            Q140=makeQuery(id+"F2.opExtrude","SWEPT_FACE",FACE,{"disambiguationData":[OSD([sQuery(id+"F0.wireOp",EDGE,"E16")])]});
            var Q141;
            Q141=makeQuery(id+"F2.opExtrude","SWEPT_FACE",FACE,{"disambiguationData":[OSD([sQuery(id+"F0.wireOp",EDGE,"E57.trimOffspring")])]});
            var Q142;
            Q142=makeQuery(id+"F2.opExtrude","SWEPT_FACE",FACE,{"disambiguationData":[OSD([sQuery(id+"F0.wireOp",EDGE,"E40.0"),sQuery(id+"F0.wireOp",EDGE,"E45")])]});
            var Q143;
            Q143=makeQuery(id+"F2.opExtrude","SWEPT_FACE",FACE,{"disambiguationData":[OSD([sQuery(id+"F0.wireOp",EDGE,"E34")])]});
            var Q144;
            Q144=makeQuery(id+"F2.opExtrude","SWEPT_FACE",FACE,{"disambiguationData":[OSD([sQuery(id+"F0.wireOp",EDGE,"E33")])]});
            var Q145;
            Q145=makeQuery(id+"F2.opExtrude","SWEPT_FACE",FACE,{"disambiguationData":[OSD([sQuery(id+"F0.wireOp",EDGE,"E61.trimOffspring")])]});
            var Q146;
            Q146=makeQuery(id+"F2.opExtrude","SWEPT_FACE",FACE,{"disambiguationData":[OSD([sQuery(id+"F0.wireOp",EDGE,"E15")])]});
            var Q147;
            Q147=makeQuery(id+"F2.opExtrude","SWEPT_FACE",FACE,{"disambiguationData":[OSD([sQuery(id+"F0.wireOp",EDGE,"E60")])]});
            var Q148;
            Q148=makeQuery(id+"F2.opExtrude","SWEPT_FACE",FACE,{"disambiguationData":[OSD([sQuery(id+"F0.wireOp",EDGE,"E35.0"),sQuery(id+"F0.wireOp",EDGE,"E41"),sQuery(id+"F0.wireOp",EDGE,"E44")])]});
            var Q149;
            Q149=makeQuery(id+"F2.opExtrude","SWEPT_FACE",FACE,{"disambiguationData":[OSD([sQuery(id+"F0.wireOp",EDGE,"E32")])]});
            var Q150;
            Q150=makeQuery(id+"F2.opExtrude","SWEPT_FACE",FACE,{"disambiguationData":[OSD([sQuery(id+"F0.wireOp",EDGE,"E50.0"),sQuery(id+"F0.wireOp",EDGE,"E59")])]});
            var Q151;
            Q151=makeQuery(id+"F2.opExtrude","SWEPT_FACE",FACE,{"disambiguationData":[OSD([sQuery(id+"F0.wireOp",EDGE,"E28")])]});
            var Q152;
            Q152=makeQuery(id+"F2.opExtrude","SWEPT_FACE",FACE,{"disambiguationData":[OSD([sQuery(id+"F0.wireOp",EDGE,"E10")])]});
            var Q153;
            Q153=makeQuery(id+"F2.opExtrude","SWEPT_FACE",FACE,{"disambiguationData":[OSD([sQuery(id+"F0.wireOp",EDGE,"E48.0"),sQuery(id+"F0.wireOp",EDGE,"E52")])]});
            var Q154;
            Q154=makeQuery(id+"F2.opExtrude","SWEPT_FACE",FACE,{"disambiguationData":[OSD([sQuery(id+"F0.wireOp",EDGE,"E26")])]});
            var Q155;
            Q155=makeQuery(id+"F2.opExtrude","SWEPT_FACE",FACE,{"disambiguationData":[OSD([sQuery(id+"F0.wireOp",EDGE,"E47.0")])]});
            var Q156;
            Q156=makeQuery(id+"F2.opExtrude","SWEPT_FACE",FACE,{"disambiguationData":[OSD([sQuery(id+"F0.wireOp",EDGE,"E24.trimOffspring")])]});
            var Q157;
            Q157=makeQuery(id+"F2.opExtrude","SWEPT_FACE",FACE,{"disambiguationData":[OSD([sQuery(id+"F0.wireOp",EDGE,"E56")])]});
            var Q158;
            Q158=makeQuery(id+"F2.opExtrude","SWEPT_FACE",FACE,{"disambiguationData":[OSD([sQuery(id+"F0.wireOp",EDGE,"E31")])]});
            var Q159;
            Q159=makeQuery(id+"F2.opExtrude","SWEPT_FACE",FACE,{"disambiguationData":[OSD([sQuery(id+"F0.wireOp",EDGE,"E13")])]});
            var Q160;
            Q160=makeQuery(id+"F2.opExtrude","CAP_EDGE",EDGE,{"disambiguationData":[OSD([sQuery(id+"F0.wireOp",EDGE,"E20")])],"isStart":false});
            var Q161;
            Q161=makeQuery(id+"F2.opExtrude","SWEPT_FACE",FACE,{"disambiguationData":[OSD([sQuery(id+"F0.wireOp",EDGE,"E49.0"),sQuery(id+"F0.wireOp",EDGE,"E53")])]});
            var Q162;
            Q162=makeQuery(id+"F2.opExtrude","SWEPT_FACE",FACE,{"disambiguationData":[OSD([sQuery(id+"F0.wireOp",EDGE,"E27")])]});
            var Q163;
            Q163=makeQuery(id+"F2.opExtrude","SWEPT_FACE",FACE,{"disambiguationData":[OSD([sQuery(id+"F0.wireOp",EDGE,"E7")])]});
            var Q164;
            Q164=makeQuery(id+"F2.opExtrude","SWEPT_FACE",FACE,{"disambiguationData":[OSD([sQuery(id+"F0.wireOp",EDGE,"E6")])]});
            var Q165;
            Q165=makeQuery(id+"F2.opExtrude","SWEPT_FACE",FACE,{"disambiguationData":[OSD([sQuery(id+"F0.wireOp",EDGE,"E4")])]});
            var Q166;
            Q166=makeQuery(id+"F2.opExtrude","SWEPT_FACE",FACE,{"disambiguationData":[OSD([sQuery(id+"F0.wireOp",EDGE,"E3")])]});
            var Q167;
            Q167=makeQuery(id+"F2.opExtrude","SWEPT_FACE",FACE,{"disambiguationData":[OSD([sQuery(id+"F0.wireOp",EDGE,"E2")])]});
            var Q168;
            Q168=makeQuery(id+"F2.opExtrude","SWEPT_FACE",FACE,{"disambiguationData":[OSD([sQuery(id+"F0.wireOp",EDGE,"E1")])]});
            var Q169;
            Q169=makeQuery(id+"F2.opExtrude","SWEPT_FACE",FACE,{"disambiguationData":[OSD([sQuery(id+"F0.wireOp",EDGE,"E0.5")])]});
            var Q170;
            Q170=makeQuery(id+"F2.opExtrude","SWEPT_FACE",FACE,{"disambiguationData":[OSD([sQuery(id+"F0.wireOp",EDGE,"E0.4")])]});
            var Q171;
            Q171=makeQuery(id+"F2.opExtrude","SWEPT_FACE",FACE,{"disambiguationData":[OSD([sQuery(id+"F0.wireOp",EDGE,"E0.3")])]});
            var Q172;
            Q172=makeQuery(id+"F2.opExtrude","SWEPT_FACE",FACE,{"disambiguationData":[OSD([sQuery(id+"F0.wireOp",EDGE,"E0.2")])]});
            var Q173;
            Q173=makeQuery(id+"F2.opExtrude","CAP_FACE",FACE,{"disambiguationData":[OSD([sQuery(id+"F0.wireOp",EDGE,"E0.1"),sQuery(id+"F0.wireOp",EDGE,"E0.2"),sQuery(id+"F0.wireOp",EDGE,"E0.3"),sQuery(id+"F0.wireOp",EDGE,"E0.4"),sQuery(id+"F0.wireOp",EDGE,"E0.5"),sQuery(id+"F0.wireOp",EDGE,"E1"),sQuery(id+"F0.wireOp",EDGE,"E2"),sQuery(id+"F0.wireOp",EDGE,"E3"),sQuery(id+"F0.wireOp",EDGE,"E4"),sQuery(id+"F0.wireOp",EDGE,"E6"),sQuery(id+"F0.wireOp",EDGE,"E7"),sQuery(id+"F0.wireOp",EDGE,"E8"),sQuery(id+"F0.wireOp",EDGE,"E9"),sQuery(id+"F0.wireOp",EDGE,"E10"),sQuery(id+"F0.wireOp",EDGE,"E11"),sQuery(id+"F0.wireOp",EDGE,"E12"),sQuery(id+"F0.wireOp",EDGE,"E13"),sQuery(id+"F0.wireOp",EDGE,"E14"),sQuery(id+"F0.wireOp",EDGE,"E15"),sQuery(id+"F0.wireOp",EDGE,"E16"),sQuery(id+"F0.wireOp",EDGE,"E17"),sQuery(id+"F0.wireOp",EDGE,"E18"),sQuery(id+"F0.wireOp",EDGE,"E19"),sQuery(id+"F0.wireOp",EDGE,"E20"),sQuery(id+"F0.wireOp",EDGE,"E21"),sQuery(id+"F0.wireOp",EDGE,"E22"),sQuery(id+"F0.wireOp",EDGE,"E24.trimOffspring"),sQuery(id+"F0.wireOp",EDGE,"E26"),sQuery(id+"F0.wireOp",EDGE,"E27"),sQuery(id+"F0.wireOp",EDGE,"E28"),sQuery(id+"F0.wireOp",EDGE,"E29"),sQuery(id+"F0.wireOp",EDGE,"E30"),sQuery(id+"F0.wireOp",EDGE,"E31"),sQuery(id+"F0.wireOp",EDGE,"E32"),sQuery(id+"F0.wireOp",EDGE,"E33"),sQuery(id+"F0.wireOp",EDGE,"E34"),sQuery(id+"F0.wireOp",EDGE,"E35.0"),sQuery(id+"F0.wireOp",EDGE,"E36.0"),sQuery(id+"F0.wireOp",EDGE,"E37.0"),sQuery(id+"F0.wireOp",EDGE,"E38.0"),sQuery(id+"F0.wireOp",EDGE,"E39.0"),sQuery(id+"F0.wireOp",EDGE,"E40.0"),sQuery(id+"F0.wireOp",EDGE,"E41"),sQuery(id+"F0.wireOp",EDGE,"E42"),sQuery(id+"F0.wireOp",EDGE,"E43"),sQuery(id+"F0.wireOp",EDGE,"E44"),sQuery(id+"F0.wireOp",EDGE,"E45"),sQuery(id+"F0.wireOp",EDGE,"E46"),sQuery(id+"F0.wireOp",EDGE,"E47.0"),sQuery(id+"F0.wireOp",EDGE,"E48.0"),sQuery(id+"F0.wireOp",EDGE,"E49.0"),sQuery(id+"F0.wireOp",EDGE,"E50.0"),sQuery(id+"F0.wireOp",EDGE,"E51.0"),sQuery(id+"F0.wireOp",EDGE,"E52"),sQuery(id+"F0.wireOp",EDGE,"E53"),sQuery(id+"F0.wireOp",EDGE,"E54"),sQuery(id+"F0.wireOp",EDGE,"E55.trimOffspring"),sQuery(id+"F0.wireOp",EDGE,"E56"),sQuery(id+"F0.wireOp",EDGE,"E57.trimOffspring"),sQuery(id+"F0.wireOp",EDGE,"E58"),sQuery(id+"F0.wireOp",EDGE,"E59"),sQuery(id+"F0.wireOp",EDGE,"E60"),sQuery(id+"F0.wireOp",EDGE,"E61.trimOffspring"),sQuery(id+"F0.wireOp",EDGE,"E62.trimOffspring")])],"isStart":false});
            var Q174;
            Q174=makeQuery(id+"F2.opExtrude","SWEPT_FACE",FACE,{"disambiguationData":[OSD([sQuery(id+"F0.wireOp",EDGE,"E0.1")])]});
            var Q175;
            Q175=makeQuery(id+"F2.opExtrude","SWEPT_FACE",FACE,{"disambiguationData":[OSD([sQuery(id+"F0.wireOp",EDGE,"E55.trimOffspring")])]});
            var Q176;
            Q176=makeQuery(id+"F2.opExtrude","SWEPT_FACE",FACE,{"disambiguationData":[OSD([sQuery(id+"F0.wireOp",EDGE,"E30")])]});
            var Q177;
            Q177=makeQuery(id+"F2.opExtrude","SWEPT_FACE",FACE,{"disambiguationData":[OSD([sQuery(id+"F0.wireOp",EDGE,"E12")])]});
            var Q178;
            {var subQ0=sQuery(id+"F0.wireOp",EDGE,"E9");Q178=makeQuery(id+"F2.opExtrude","SWEPT_FACE",FACE,{"disambiguationData":[OSD([subQ0]),TDD([makeQuery(id+"F0.imprint","IMPRINT",EDGE,{"disambiguationData":[TD([[makeQuery(id+"F0.imprint","INTERSECT",VERTEX,{"derivedFrom":[sQuery(id+"F0.wireOp",EDGE,"E0.4"),subQ0]}),-1.0]])],"derivedFrom":subQ0})])]});}
            var Q179;
            Q179=makeQuery(id+"F2.opExtrude","SWEPT_FACE",FACE,{"disambiguationData":[OSD([sQuery(id+"F0.wireOp",EDGE,"E8")])]});
            var Q180;
            {var subQ0=sQuery(id+"F0.wireOp",EDGE,"E9");Q180=makeQuery(id+"F2.opExtrude","SWEPT_FACE",FACE,{"disambiguationData":[OSD([subQ0]),TDD([makeQuery(id+"F0.imprint","IMPRINT",EDGE,{"disambiguationData":[TD([[makeQuery(id+"F0.imprint","INTERSECT",VERTEX,{"derivedFrom":[sQuery(id+"F0.wireOp",EDGE,"E0.3"),subQ0]}),1.0]])],"derivedFrom":subQ0})])]});}
            var Q181;
            Q181=makeQuery(id+"F2.opExtrude","SWEPT_FACE",FACE,{"disambiguationData":[OSD([sQuery(id+"F0.wireOp",EDGE,"E51.0"),sQuery(id+"F0.wireOp",EDGE,"E54")])]});
            var Q182;
            Q182=makeQuery(id+"F2.opExtrude","SWEPT_FACE",FACE,{"disambiguationData":[OSD([sQuery(id+"F0.wireOp",EDGE,"E29")])]});
            var Q183;
            Q183=makeQuery(id+"F2.opExtrude","SWEPT_FACE",FACE,{"disambiguationData":[OSD([sQuery(id+"F0.wireOp",EDGE,"E11")])]});
            var Q184;
            Q184=makeQuery(id+"F2.opExtrude","SWEPT_FACE",FACE,{"disambiguationData":[OSD([sQuery(id+"F0.wireOp",EDGE,"E114.MirrorCS")])]});
            var Q185;
            Q185=makeQuery(id+"F2.opExtrude","CAP_EDGE",EDGE,{"disambiguationData":[OSD([sQuery(id+"F0.wireOp",EDGE,"E90.MirrorCS")])],"isStart":false});
            var Q186;
            Q186=makeQuery(id+"F2.opExtrude","SWEPT_FACE",FACE,{"disambiguationData":[OSD([sQuery(id+"F0.wireOp",EDGE,"E88.MirrorCS")])]});
            var Q187;
            Q187=makeQuery(id+"F2.opExtrude","SWEPT_FACE",FACE,{"disambiguationData":[OSD([sQuery(id+"F0.wireOp",EDGE,"E121.MirrorCS")])]});
            var Q188;
            Q188=makeQuery(id+"F2.opExtrude","SWEPT_FACE",FACE,{"disambiguationData":[OSD([sQuery(id+"F0.wireOp",EDGE,"E68.MirrorCS"),sQuery(id+"F0.wireOp",EDGE,"E77.MirrorCS"),sQuery(id+"F0.wireOp",EDGE,"E72.MirrorCS")])]});
            var Q189;
            Q189=makeQuery(id+"F2.opExtrude","SWEPT_FACE",FACE,{"disambiguationData":[OSD([sQuery(id+"F0.wireOp",EDGE,"E102.MirrorCS")])]});
            var Q190;
            Q190=makeQuery(id+"F2.opExtrude","SWEPT_FACE",FACE,{"disambiguationData":[OSD([sQuery(id+"F0.wireOp",EDGE,"E73.MirrorCS"),sQuery(id+"F0.wireOp",EDGE,"E96.MirrorCS")])]});
            var Q191;
            Q191=makeQuery(id+"F2.opExtrude","SWEPT_FACE",FACE,{"disambiguationData":[OSD([sQuery(id+"F0.wireOp",EDGE,"E122.MirrorCS")])]});
            var Q192;
            Q192=makeQuery(id+"F2.opExtrude","SWEPT_FACE",FACE,{"disambiguationData":[OSD([sQuery(id+"F0.wireOp",EDGE,"E124.MirrorCS")])]});
            var Q193;
            Q193=makeQuery(id+"F2.opExtrude","SWEPT_FACE",FACE,{"disambiguationData":[OSD([sQuery(id+"F0.wireOp",EDGE,"E86.MirrorC")])]});
            var Q194;
            Q194=makeQuery(id+"F2.opExtrude","CAP_FACE",FACE,{"disambiguationData":[OSD([sQuery(id+"F0.wireOp",EDGE,"E73.MirrorCS"),sQuery(id+"F0.wireOp",EDGE,"E68.MirrorCS"),sQuery(id+"F0.wireOp",EDGE,"E69.MirrorCS"),sQuery(id+"F0.wireOp",EDGE,"E89.MirrorCS"),sQuery(id+"F0.wireOp",EDGE,"E77.MirrorCS"),sQuery(id+"F0.wireOp",EDGE,"E67.MirrorCS"),sQuery(id+"F0.wireOp",EDGE,"E84.MirrorCS"),sQuery(id+"F0.wireOp",EDGE,"E85.MirrorCS"),sQuery(id+"F0.wireOp",EDGE,"E72.MirrorCS"),sQuery(id+"F0.wireOp",EDGE,"E91.MirrorC"),sQuery(id+"F0.wireOp",EDGE,"E75.MirrorCS"),sQuery(id+"F0.wireOp",EDGE,"E82.MirrorCS"),sQuery(id+"F0.wireOp",EDGE,"E87.MirrorCS"),sQuery(id+"F0.wireOp",EDGE,"E79.MirrorCS"),sQuery(id+"F0.wireOp",EDGE,"E78.MirrorC"),sQuery(id+"F0.wireOp",EDGE,"E70.MirrorCS"),sQuery(id+"F0.wireOp",EDGE,"E66.MirrorCS"),sQuery(id+"F0.wireOp",EDGE,"E80.MirrorCS"),sQuery(id+"F0.wireOp",EDGE,"E88.MirrorCS"),sQuery(id+"F0.wireOp",EDGE,"E86.MirrorC"),sQuery(id+"F0.wireOp",EDGE,"E65.MirrorCS"),sQuery(id+"F0.wireOp",EDGE,"E71.MirrorCS"),sQuery(id+"F0.wireOp",EDGE,"E83.MirrorCS"),sQuery(id+"F0.wireOp",EDGE,"E90.MirrorCS"),sQuery(id+"F0.wireOp",EDGE,"E76.MirrorCS"),sQuery(id+"F0.wireOp",EDGE,"E92.MirrorCS"),sQuery(id+"F0.wireOp",EDGE,"E63.MirrorC"),sQuery(id+"F0.wireOp",EDGE,"E64.MirrorCS"),sQuery(id+"F0.wireOp",EDGE,"E74.MirrorCS"),sQuery(id+"F0.wireOp",EDGE,"E96.MirrorCS"),sQuery(id+"F0.wireOp",EDGE,"E95.MirrorCS"),sQuery(id+"F0.wireOp",EDGE,"E93.MirrorCS"),sQuery(id+"F0.wireOp",EDGE,"E98.MirrorCS"),sQuery(id+"F0.wireOp",EDGE,"E94.MirrorCS"),sQuery(id+"F0.wireOp",EDGE,"E100.MirrorCS"),sQuery(id+"F0.wireOp",EDGE,"E97.MirrorCS"),sQuery(id+"F0.wireOp",EDGE,"E103.MirrorCS"),sQuery(id+"F0.wireOp",EDGE,"E113.MirrorCS"),sQuery(id+"F0.wireOp",EDGE,"E99.MirrorC"),sQuery(id+"F0.wireOp",EDGE,"E102.MirrorCS"),sQuery(id+"F0.wireOp",EDGE,"E106.MirrorCS"),sQuery(id+"F0.wireOp",EDGE,"E126.MirrorC"),sQuery(id+"F0.wireOp",EDGE,"E125.MirrorC"),sQuery(id+"F0.wireOp",EDGE,"E116.MirrorCS"),sQuery(id+"F0.wireOp",EDGE,"E115.MirrorCS"),sQuery(id+"F0.wireOp",EDGE,"E110.MirrorCS"),sQuery(id+"F0.wireOp",EDGE,"E101.MirrorCS"),sQuery(id+"F0.wireOp",EDGE,"E111.MirrorCS"),sQuery(id+"F0.wireOp",EDGE,"E119.MirrorCS"),sQuery(id+"F0.wireOp",EDGE,"E114.MirrorCS"),sQuery(id+"F0.wireOp",EDGE,"E104.MirrorCS"),sQuery(id+"F0.wireOp",EDGE,"E109.MirrorCS"),sQuery(id+"F0.wireOp",EDGE,"E105.MirrorCS"),sQuery(id+"F0.wireOp",EDGE,"E81.MirrorCS"),sQuery(id+"F0.wireOp",EDGE,"E120.MirrorCS"),sQuery(id+"F0.wireOp",EDGE,"E123.MirrorC"),sQuery(id+"F0.wireOp",EDGE,"E124.MirrorCS"),sQuery(id+"F0.wireOp",EDGE,"E122.MirrorCS"),sQuery(id+"F0.wireOp",EDGE,"E121.MirrorCS"),sQuery(id+"F0.wireOp",EDGE,"E108.MirrorCS"),sQuery(id+"F0.wireOp",EDGE,"E107.MirrorC"),sQuery(id+"F0.wireOp",EDGE,"E112.MirrorCS"),sQuery(id+"F0.wireOp",EDGE,"E118.MirrorCS"),sQuery(id+"F0.wireOp",EDGE,"E117.MirrorCS")])],"isStart":false});
            var Q195;
            Q195=makeQuery(id+"F2.opExtrude","SWEPT_FACE",FACE,{"disambiguationData":[OSD([sQuery(id+"F0.wireOp",EDGE,"E113.MirrorCS")])]});
            var Q196;
            Q196=makeQuery(id+"F2.opExtrude","SWEPT_FACE",FACE,{"disambiguationData":[OSD([sQuery(id+"F0.wireOp",EDGE,"E103.MirrorCS")])]});
            var Q197;
            Q197=makeQuery(id+"F2.opExtrude","SWEPT_FACE",FACE,{"disambiguationData":[OSD([sQuery(id+"F0.wireOp",EDGE,"E97.MirrorCS")])]});
            var Q198;
            Q198=makeQuery(id+"F2.opExtrude","SWEPT_FACE",FACE,{"disambiguationData":[OSD([sQuery(id+"F0.wireOp",EDGE,"E123.MirrorC")])]});
            var Q199;
            Q199=makeQuery(id+"F2.opExtrude","CAP_EDGE",EDGE,{"disambiguationData":[OSD([sQuery(id+"F0.wireOp",EDGE,"E101.MirrorCS")])],"isStart":false});
            var Q200;
            Q200=makeQuery(id+"F2.opExtrude","SWEPT_FACE",FACE,{"disambiguationData":[OSD([sQuery(id+"F0.wireOp",EDGE,"E99.MirrorC")])]});
            var Q201;
            Q201=makeQuery(id+"F2.opExtrude","CAP_EDGE",EDGE,{"disambiguationData":[OSD([sQuery(id+"F0.wireOp",EDGE,"E109.MirrorCS")])],"isStart":false});
            var Q202;
            Q202=makeQuery(id+"F2.opExtrude","SWEPT_FACE",FACE,{"disambiguationData":[OSD([sQuery(id+"F0.wireOp",EDGE,"E82.MirrorCS")])]});
            var Q203;
            Q203=makeQuery(id+"F2.opExtrude","CAP_EDGE",EDGE,{"disambiguationData":[OSD([sQuery(id+"F0.wireOp",EDGE,"E110.MirrorCS")])],"isStart":false});
            var Q204;
            Q204=makeQuery(id+"F2.opExtrude","SWEPT_FACE",FACE,{"disambiguationData":[OSD([sQuery(id+"F0.wireOp",EDGE,"E87.MirrorCS")])]});
            var Q205;
            Q205=makeQuery(id+"F2.opExtrude","SWEPT_FACE",FACE,{"disambiguationData":[OSD([sQuery(id+"F0.wireOp",EDGE,"E80.MirrorCS"),sQuery(id+"F0.wireOp",EDGE,"E64.MirrorCS")])]});
            var Q206;
            Q206=makeQuery(id+"F2.opExtrude","SWEPT_FACE",FACE,{"disambiguationData":[OSD([sQuery(id+"F0.wireOp",EDGE,"E120.MirrorCS")])]});
            var Q207;
            Q207=makeQuery(id+"F2.opExtrude","SWEPT_FACE",FACE,{"disambiguationData":[OSD([sQuery(id+"F0.wireOp",EDGE,"E71.MirrorCS"),sQuery(id+"F0.wireOp",EDGE,"E111.MirrorCS")])]});
            var Q208;
            Q208=makeQuery(id+"F2.opExtrude","SWEPT_FACE",FACE,{"disambiguationData":[OSD([sQuery(id+"F0.wireOp",EDGE,"E94.MirrorCS")])]});
            var Q209;
            Q209=makeQuery(id+"F2.opExtrude","SWEPT_FACE",FACE,{"disambiguationData":[OSD([sQuery(id+"F0.wireOp",EDGE,"E93.MirrorCS")])]});
            var Q210;
            Q210=makeQuery(id+"F2.opExtrude","SWEPT_FACE",FACE,{"disambiguationData":[OSD([sQuery(id+"F0.wireOp",EDGE,"E105.MirrorCS")])]});
            var Q211;
            Q211=makeQuery(id+"F2.opExtrude","SWEPT_FACE",FACE,{"disambiguationData":[OSD([sQuery(id+"F0.wireOp",EDGE,"E109.MirrorCS")])]});
            var Q212;
            Q212=makeQuery(id+"F2.opExtrude","SWEPT_FACE",FACE,{"disambiguationData":[OSD([sQuery(id+"F0.wireOp",EDGE,"E70.MirrorCS"),sQuery(id+"F0.wireOp",EDGE,"E106.MirrorCS")])]});
            var Q213;
            Q213=makeQuery(id+"F2.opExtrude","SWEPT_FACE",FACE,{"disambiguationData":[OSD([sQuery(id+"F0.wireOp",EDGE,"E104.MirrorCS")])]});
            var Q214;
            Q214=makeQuery(id+"F2.opExtrude","SWEPT_FACE",FACE,{"disambiguationData":[OSD([sQuery(id+"F0.wireOp",EDGE,"E78.MirrorC")])]});
            var Q215;
            Q215=makeQuery(id+"F2.opExtrude","SWEPT_FACE",FACE,{"disambiguationData":[OSD([sQuery(id+"F0.wireOp",EDGE,"E100.MirrorCS")])]});
            var Q216;
            Q216=makeQuery(id+"F2.opExtrude","SWEPT_FACE",FACE,{"disambiguationData":[OSD([sQuery(id+"F0.wireOp",EDGE,"E95.MirrorCS")])]});
            var Q217;
            Q217=makeQuery(id+"F2.opExtrude","SWEPT_FACE",FACE,{"disambiguationData":[OSD([sQuery(id+"F0.wireOp",EDGE,"E118.MirrorCS")])]});
            var Q218;
            Q218=makeQuery(id+"F2.opExtrude","SWEPT_FACE",FACE,{"disambiguationData":[OSD([sQuery(id+"F0.wireOp",EDGE,"E115.MirrorCS")])]});
            var Q219;
            Q219=makeQuery(id+"F2.opExtrude","SWEPT_FACE",FACE,{"disambiguationData":[OSD([sQuery(id+"F0.wireOp",EDGE,"E92.MirrorCS")])]});
            var Q220;
            Q220=makeQuery(id+"F2.opExtrude","SWEPT_FACE",FACE,{"disambiguationData":[OSD([sQuery(id+"F0.wireOp",EDGE,"E84.MirrorCS"),sQuery(id+"F0.wireOp",EDGE,"E98.MirrorCS")])]});
            var Q221;
            Q221=makeQuery(id+"F2.opExtrude","CAP_EDGE",EDGE,{"disambiguationData":[OSD([sQuery(id+"F0.wireOp",EDGE,"E69.MirrorCS"),sQuery(id+"F0.wireOp",EDGE,"E79.MirrorCS"),sQuery(id+"F0.wireOp",EDGE,"E66.MirrorCS")])],"isStart":false});
            var Q222;
            Q222=makeQuery(id+"F2.opExtrude","SWEPT_FACE",FACE,{"disambiguationData":[OSD([sQuery(id+"F0.wireOp",EDGE,"E107.MirrorC")])]});
            var Q223;
            Q223=makeQuery(id+"F2.opExtrude","SWEPT_FACE",FACE,{"disambiguationData":[OSD([sQuery(id+"F0.wireOp",EDGE,"E125.MirrorC")])]});
            var Q224;
            Q224=makeQuery(id+"F2.opExtrude","SWEPT_FACE",FACE,{"disambiguationData":[OSD([sQuery(id+"F0.wireOp",EDGE,"E90.MirrorCS")])]});
            var Q225;
            Q225=makeQuery(id+"F2.opExtrude","SWEPT_FACE",FACE,{"disambiguationData":[OSD([sQuery(id+"F0.wireOp",EDGE,"E89.MirrorCS")])]});
            var Q226;
            Q226=makeQuery(id+"F2.opExtrude","SWEPT_FACE",FACE,{"disambiguationData":[OSD([sQuery(id+"F0.wireOp",EDGE,"E108.MirrorCS")])]});
            var Q227;
            Q227=makeQuery(id+"F2.opExtrude","SWEPT_FACE",FACE,{"disambiguationData":[OSD([sQuery(id+"F0.wireOp",EDGE,"E126.MirrorC")])]});
            var Q228;
            Q228=makeQuery(id+"F2.opExtrude","SWEPT_FACE",FACE,{"disambiguationData":[OSD([sQuery(id+"F0.wireOp",EDGE,"E83.MirrorCS")])]});
            var Q229;
            Q229=makeQuery(id+"F2.opExtrude","SWEPT_FACE",FACE,{"disambiguationData":[OSD([sQuery(id+"F0.wireOp",EDGE,"E69.MirrorCS"),sQuery(id+"F0.wireOp",EDGE,"E79.MirrorCS"),sQuery(id+"F0.wireOp",EDGE,"E66.MirrorCS")])]});
            var Q230;
            Q230=makeQuery(id+"F2.opExtrude","SWEPT_FACE",FACE,{"disambiguationData":[OSD([sQuery(id+"F0.wireOp",EDGE,"E119.MirrorCS")])]});
            var Q231;
            Q231=makeQuery(id+"F2.opExtrude","CAP_EDGE",EDGE,{"disambiguationData":[OSD([sQuery(id+"F0.wireOp",EDGE,"E102.MirrorCS")])],"isStart":false});
            var Q232;
            {var subQ0=sQuery(id+"F0.wireOp",EDGE,"E74.MirrorCS");Q232=makeQuery(id+"F2.opExtrude","SWEPT_FACE",FACE,{"disambiguationData":[OSD([subQ0]),TDD([makeQuery(id+"F0.imprint","IMPRINT",EDGE,{"disambiguationData":[TD([[makeQuery(id+"F0.imprint","INTERSECT",VERTEX,{"derivedFrom":[sQuery(id+"F0.wireOp",EDGE,"E76.MirrorCS"),subQ0]}),1.0]])],"derivedFrom":subQ0})])]});}
            var Q233;
            Q233=makeQuery(id+"F2.opExtrude","SWEPT_FACE",FACE,{"disambiguationData":[OSD([sQuery(id+"F0.wireOp",EDGE,"E75.MirrorCS")])]});
            var Q234;
            Q234=makeQuery(id+"F2.opExtrude","CAP_EDGE",EDGE,{"disambiguationData":[OSD([sQuery(id+"F0.wireOp",EDGE,"E112.MirrorCS")])],"isStart":false});
            var Q235;
            Q235=makeQuery(id+"F2.opExtrude","CAP_EDGE",EDGE,{"disambiguationData":[OSD([sQuery(id+"F0.wireOp",EDGE,"E105.MirrorCS")])],"isStart":false});
            var Q236;
            Q236=makeQuery(id+"F2.opExtrude","SWEPT_FACE",FACE,{"disambiguationData":[OSD([sQuery(id+"F0.wireOp",EDGE,"E112.MirrorCS")])]});
            var Q237;
            Q237=makeQuery(id+"F2.opExtrude","SWEPT_FACE",FACE,{"disambiguationData":[OSD([sQuery(id+"F0.wireOp",EDGE,"E116.MirrorCS")])]});
            var Q238;
            Q238=makeQuery(id+"F2.opExtrude","SWEPT_FACE",FACE,{"disambiguationData":[OSD([sQuery(id+"F0.wireOp",EDGE,"E76.MirrorCS")])]});
            var Q239;
            Q239=makeQuery(id+"F2.opExtrude","SWEPT_FACE",FACE,{"disambiguationData":[OSD([sQuery(id+"F0.wireOp",EDGE,"E67.MirrorCS"),sQuery(id+"F0.wireOp",EDGE,"E81.MirrorCS")])]});
            var Q240;
            Q240=makeQuery(id+"F2.opExtrude","SWEPT_FACE",FACE,{"disambiguationData":[OSD([sQuery(id+"F0.wireOp",EDGE,"E101.MirrorCS")])]});
            var Q241;
            {var subQ0=sQuery(id+"F0.wireOp",EDGE,"E74.MirrorCS");Q241=makeQuery(id+"F2.opExtrude","SWEPT_FACE",FACE,{"disambiguationData":[OSD([subQ0]),TDD([makeQuery(id+"F0.imprint","IMPRINT",EDGE,{"disambiguationData":[TD([[makeQuery(id+"F0.imprint","INTERSECT",VERTEX,{"derivedFrom":[sQuery(id+"F0.wireOp",EDGE,"E75.MirrorCS"),subQ0]}),-1.0]])],"derivedFrom":subQ0})])]});}
            var Q242;
            Q242=makeQuery(id+"F2.opExtrude","SWEPT_FACE",FACE,{"disambiguationData":[OSD([sQuery(id+"F0.wireOp",EDGE,"E91.MirrorC")])]});
            var Q243;
            Q243=makeQuery(id+"F2.opExtrude","SWEPT_FACE",FACE,{"disambiguationData":[OSD([sQuery(id+"F0.wireOp",EDGE,"E117.MirrorCS")])]});
            var Q244;
            Q244=makeQuery(id+"F2.opExtrude","SWEPT_FACE",FACE,{"disambiguationData":[OSD([sQuery(id+"F0.wireOp",EDGE,"E110.MirrorCS")])]});
            var Q245;
            Q245=makeQuery(id+"F2.opExtrude","SWEPT_FACE",FACE,{"disambiguationData":[OSD([sQuery(id+"F0.wireOp",EDGE,"E63.MirrorC")])]});
            var Q246;
            Q246=makeQuery(id+"F2.opExtrude","SWEPT_FACE",FACE,{"disambiguationData":[OSD([sQuery(id+"F0.wireOp",EDGE,"E85.MirrorCS")])]});
            var Q247;
            Q247=makeQuery(id+"F1.opExtrude","SWEPT_EDGE",EDGE,{"disambiguationData":[OSD([sQuery(id+"F0.wireOp",EDGE,"E97.MirrorCS"),sQuery(id+"F0.wireOp",EDGE,"E102.MirrorCS")])]});
            var Q248;
            Q248=makeQuery(id+"F1.opExtrude","SWEPT_EDGE",EDGE,{"disambiguationData":[OSD([sQuery(id+"F0.wireOp",EDGE,"E69.MirrorCS"),sQuery(id+"F0.wireOp",EDGE,"E89.MirrorCS")])]});
            var Q249;
            Q249=makeQuery(id+"F1.opExtrude","CAP_EDGE",EDGE,{"disambiguationData":[OSD([sQuery(id+"F0.wireOp",EDGE,"E109.MirrorCS")])],"isStart":true});
            var Q250;
            Q250=makeQuery(id+"F1.opExtrude","SWEPT_EDGE",EDGE,{"disambiguationData":[OSD([sQuery(id+"F0.wireOp",EDGE,"E90.MirrorCS"),sQuery(id+"F0.wireOp",EDGE,"E119.MirrorCS")])]});
            var Q251;
            Q251=makeQuery(id+"F1.opExtrude","CAP_EDGE",EDGE,{"disambiguationData":[OSD([sQuery(id+"F0.wireOp",EDGE,"E90.MirrorCS")])],"isStart":true});
            var Q252;
            Q252=makeQuery(id+"F1.opExtrude","CAP_EDGE",EDGE,{"disambiguationData":[OSD([sQuery(id+"F0.wireOp",EDGE,"E87.MirrorCS")])],"isStart":false});
            var Q253;
            Q253=makeQuery(id+"F1.opExtrude","SWEPT_EDGE",EDGE,{"disambiguationData":[OSD([sQuery(id+"F0.wireOp",EDGE,"E83.MirrorCS"),sQuery(id+"F0.wireOp",EDGE,"E103.MirrorCS")])]});
            var Q254;
            Q254=makeQuery(id+"F1.opExtrude","CAP_EDGE",EDGE,{"disambiguationData":[OSD([sQuery(id+"F0.wireOp",EDGE,"E82.MirrorCS")])],"isStart":false});
            var Q255;
            Q255=makeQuery(id+"F1.opExtrude","CAP_EDGE",EDGE,{"disambiguationData":[OSD([sQuery(id+"F0.wireOp",EDGE,"E71.MirrorCS"),sQuery(id+"F0.wireOp",EDGE,"E111.MirrorCS")])],"isStart":false});
            var Q256;
            Q256=makeQuery(id+"F1.opExtrude","SWEPT_EDGE",EDGE,{"disambiguationData":[OSD([sQuery(id+"F0.wireOp",EDGE,"E103.MirrorCS"),sQuery(id+"F0.wireOp",EDGE,"E105.MirrorCS")])]});
            var Q257;
            Q257=makeQuery(id+"F1.opExtrude","CAP_EDGE",EDGE,{"disambiguationData":[OSD([sQuery(id+"F0.wireOp",EDGE,"E114.MirrorCS")])],"isStart":false});
            var Q258;
            Q258=makeQuery(id+"F1.opExtrude","CAP_EDGE",EDGE,{"disambiguationData":[OSD([sQuery(id+"F0.wireOp",EDGE,"E68.MirrorCS"),sQuery(id+"F0.wireOp",EDGE,"E77.MirrorCS"),sQuery(id+"F0.wireOp",EDGE,"E72.MirrorCS")])],"isStart":false});
            var Q259;
            Q259=makeQuery(id+"F1.opExtrude","CAP_EDGE",EDGE,{"disambiguationData":[OSD([sQuery(id+"F0.wireOp",EDGE,"E95.MirrorCS")])],"isStart":false});
            var Q260;
            Q260=makeQuery(id+"F1.opExtrude","SWEPT_EDGE",EDGE,{"disambiguationData":[OSD([sQuery(id+"F0.wireOp",EDGE,"E88.MirrorCS"),sQuery(id+"F0.wireOp",EDGE,"E64.MirrorCS")])]});
            var Q261;
            Q261=makeQuery(id+"F1.opExtrude","SWEPT_EDGE",EDGE,{"disambiguationData":[OSD([sQuery(id+"F0.wireOp",EDGE,"E97.MirrorCS"),sQuery(id+"F0.wireOp",EDGE,"E104.MirrorCS")])]});
            var Q262;
            Q262=makeQuery(id+"F1.opExtrude","CAP_EDGE",EDGE,{"disambiguationData":[OSD([sQuery(id+"F0.wireOp",EDGE,"E121.MirrorCS")])],"isStart":false});
            var Q263;
            Q263=makeQuery(id+"F1.opExtrude","CAP_EDGE",EDGE,{"disambiguationData":[OSD([sQuery(id+"F0.wireOp",EDGE,"E89.MirrorCS")])],"isStart":false});
            var Q264;
            Q264=makeQuery(id+"F1.opExtrude","CAP_EDGE",EDGE,{"disambiguationData":[OSD([sQuery(id+"F0.wireOp",EDGE,"E78.MirrorC")])],"isStart":false});
            var Q265;
            Q265=makeQuery(id+"F1.opExtrude","SWEPT_EDGE",EDGE,{"disambiguationData":[OSD([sQuery(id+"F0.wireOp",EDGE,"E76.MirrorCS"),sQuery(id+"F0.wireOp",EDGE,"E120.MirrorCS")])]});
            var Q266;
            Q266=makeQuery(id+"F1.opExtrude","CAP_EDGE",EDGE,{"disambiguationData":[OSD([sQuery(id+"F0.wireOp",EDGE,"E67.MirrorCS"),sQuery(id+"F0.wireOp",EDGE,"E81.MirrorCS")])],"isStart":false});
            var Q267;
            Q267=makeQuery(id+"F1.opExtrude","CAP_EDGE",EDGE,{"disambiguationData":[OSD([sQuery(id+"F0.wireOp",EDGE,"E76.MirrorCS")])],"isStart":false});
            var Q268;
            Q268=makeQuery(id+"F1.opExtrude","SWEPT_EDGE",EDGE,{"disambiguationData":[OSD([sQuery(id+"F0.wireOp",EDGE,"E92.MirrorCS"),sQuery(id+"F0.wireOp",EDGE,"E113.MirrorCS")])]});
            var Q269;
            Q269=makeQuery(id+"F1.opExtrude","SWEPT_EDGE",EDGE,{"disambiguationData":[OSD([sQuery(id+"F0.wireOp",EDGE,"E84.MirrorCS"),sQuery(id+"F0.wireOp",EDGE,"E85.MirrorCS")])]});
            var Q270;
            Q270=makeQuery(id+"F1.opExtrude","SWEPT_EDGE",EDGE,{"disambiguationData":[OSD([sQuery(id+"F0.wireOp",EDGE,"E76.MirrorCS"),sQuery(id+"F0.wireOp",EDGE,"E74.MirrorCS")])]});
            var Q271;
            Q271=makeQuery(id+"F1.opExtrude","SWEPT_EDGE",EDGE,{"disambiguationData":[OSD([sQuery(id+"F0.wireOp",EDGE,"E115.MirrorCS"),sQuery(id+"F0.wireOp",EDGE,"E118.MirrorCS")])]});
            var Q272;
            Q272=makeQuery(id+"F1.opExtrude","CAP_EDGE",EDGE,{"disambiguationData":[OSD([sQuery(id+"F0.wireOp",EDGE,"E112.MirrorCS")])],"isStart":true});
            var Q273;
            Q273=makeQuery(id+"F1.opExtrude","CAP_EDGE",EDGE,{"disambiguationData":[OSD([sQuery(id+"F0.wireOp",EDGE,"E84.MirrorCS"),sQuery(id+"F0.wireOp",EDGE,"E98.MirrorCS")])],"isStart":false});
            var Q274;
            Q274=makeQuery(id+"F1.opExtrude","SWEPT_EDGE",EDGE,{"disambiguationData":[OSD([sQuery(id+"F0.wireOp",EDGE,"E96.MirrorCS"),sQuery(id+"F0.wireOp",EDGE,"E109.MirrorCS")])]});
            var Q275;
            Q275=makeQuery(id+"F1.opExtrude","SWEPT_EDGE",EDGE,{"disambiguationData":[OSD([sQuery(id+"F0.wireOp",EDGE,"E119.MirrorCS"),sQuery(id+"F0.wireOp",EDGE,"E117.MirrorCS")])]});
            var Q276;
            Q276=makeQuery(id+"F1.opExtrude","CAP_EDGE",EDGE,{"disambiguationData":[OSD([sQuery(id+"F0.wireOp",EDGE,"E80.MirrorCS"),sQuery(id+"F0.wireOp",EDGE,"E64.MirrorCS")])],"isStart":false});
            var Q277;
            Q277=makeQuery(id+"F1.opExtrude","CAP_EDGE",EDGE,{"disambiguationData":[OSD([sQuery(id+"F0.wireOp",EDGE,"E97.MirrorCS")])],"isStart":false});
            var Q278;
            Q278=makeQuery(id+"F1.opExtrude","CAP_EDGE",EDGE,{"disambiguationData":[OSD([sQuery(id+"F0.wireOp",EDGE,"E118.MirrorCS")])],"isStart":false});
            var Q279;
            Q279=makeQuery(id+"F1.opExtrude","CAP_EDGE",EDGE,{"disambiguationData":[OSD([sQuery(id+"F0.wireOp",EDGE,"E116.MirrorCS")])],"isStart":false});
            var Q280;
            Q280=makeQuery(id+"F1.opExtrude","SWEPT_EDGE",EDGE,{"disambiguationData":[OSD([sQuery(id+"F0.wireOp",EDGE,"E110.MirrorCS"),sQuery(id+"F0.wireOp",EDGE,"E101.MirrorCS")])]});
            var Q281;
            Q281=makeQuery(id+"F1.opExtrude","CAP_EDGE",EDGE,{"disambiguationData":[OSD([sQuery(id+"F0.wireOp",EDGE,"E100.MirrorCS")])],"isStart":false});
            var Q282;
            Q282=makeQuery(id+"F1.opExtrude","SWEPT_EDGE",EDGE,{"disambiguationData":[OSD([sQuery(id+"F0.wireOp",EDGE,"E75.MirrorCS"),sQuery(id+"F0.wireOp",EDGE,"E74.MirrorCS")])]});
            var Q283;
            Q283=makeQuery(id+"F1.opExtrude","CAP_EDGE",EDGE,{"disambiguationData":[OSD([sQuery(id+"F0.wireOp",EDGE,"E125.MirrorC")])],"isStart":false});
            var Q284;
            Q284=makeQuery(id+"F1.opExtrude","CAP_EDGE",EDGE,{"disambiguationData":[OSD([sQuery(id+"F0.wireOp",EDGE,"E70.MirrorCS"),sQuery(id+"F0.wireOp",EDGE,"E106.MirrorCS")])],"isStart":false});
            var Q285;
            Q285=makeQuery(id+"F1.opExtrude","CAP_EDGE",EDGE,{"disambiguationData":[OSD([sQuery(id+"F0.wireOp",EDGE,"E94.MirrorCS")])],"isStart":false});
            var Q286;
            Q286=makeQuery(id+"F1.opExtrude","CAP_EDGE",EDGE,{"disambiguationData":[OSD([sQuery(id+"F0.wireOp",EDGE,"E107.MirrorC")])],"isStart":false});
            var Q287;
            Q287=makeQuery(id+"F1.opExtrude","CAP_EDGE",EDGE,{"disambiguationData":[OSD([sQuery(id+"F0.wireOp",EDGE,"E110.MirrorCS")])],"isStart":true});
            var Q288;
            Q288=makeQuery(id+"F1.opExtrude","CAP_EDGE",EDGE,{"disambiguationData":[OSD([sQuery(id+"F0.wireOp",EDGE,"E91.MirrorC")])],"isStart":false});
            var Q289;
            {var subQ0=sQuery(id+"F0.wireOp",EDGE,"E74.MirrorCS");Q289=makeQuery(id+"F1.opExtrude","CAP_EDGE",EDGE,{"disambiguationData":[OSD([subQ0]),TDD([makeQuery(id+"F0.imprint","IMPRINT",EDGE,{"disambiguationData":[TD([[makeQuery(id+"F0.imprint","INTERSECT",VERTEX,{"derivedFrom":[sQuery(id+"F0.wireOp",EDGE,"E75.MirrorCS"),subQ0]}),-1.0]])],"derivedFrom":subQ0})])],"isStart":false});}
            var Q290;
            Q290=makeQuery(id+"F1.opExtrude","CAP_EDGE",EDGE,{"disambiguationData":[OSD([sQuery(id+"F0.wireOp",EDGE,"E101.MirrorCS")])],"isStart":true});
            var Q291;
            Q291=makeQuery(id+"F1.opExtrude","CAP_EDGE",EDGE,{"disambiguationData":[OSD([sQuery(id+"F0.wireOp",EDGE,"E113.MirrorCS")])],"isStart":false});
            var Q292;
            Q292=makeQuery(id+"F1.opExtrude","CAP_FACE",FACE,{"disambiguationData":[OSD([sQuery(id+"F0.wireOp",EDGE,"E73.MirrorCS"),sQuery(id+"F0.wireOp",EDGE,"E68.MirrorCS"),sQuery(id+"F0.wireOp",EDGE,"E69.MirrorCS"),sQuery(id+"F0.wireOp",EDGE,"E89.MirrorCS"),sQuery(id+"F0.wireOp",EDGE,"E77.MirrorCS"),sQuery(id+"F0.wireOp",EDGE,"E67.MirrorCS"),sQuery(id+"F0.wireOp",EDGE,"E84.MirrorCS"),sQuery(id+"F0.wireOp",EDGE,"E85.MirrorCS"),sQuery(id+"F0.wireOp",EDGE,"E72.MirrorCS"),sQuery(id+"F0.wireOp",EDGE,"E91.MirrorC"),sQuery(id+"F0.wireOp",EDGE,"E75.MirrorCS"),sQuery(id+"F0.wireOp",EDGE,"E82.MirrorCS"),sQuery(id+"F0.wireOp",EDGE,"E87.MirrorCS"),sQuery(id+"F0.wireOp",EDGE,"E79.MirrorCS"),sQuery(id+"F0.wireOp",EDGE,"E78.MirrorC"),sQuery(id+"F0.wireOp",EDGE,"E70.MirrorCS"),sQuery(id+"F0.wireOp",EDGE,"E66.MirrorCS"),sQuery(id+"F0.wireOp",EDGE,"E80.MirrorCS"),sQuery(id+"F0.wireOp",EDGE,"E88.MirrorCS"),sQuery(id+"F0.wireOp",EDGE,"E86.MirrorC"),sQuery(id+"F0.wireOp",EDGE,"E65.MirrorCS"),sQuery(id+"F0.wireOp",EDGE,"E71.MirrorCS"),sQuery(id+"F0.wireOp",EDGE,"E83.MirrorCS"),sQuery(id+"F0.wireOp",EDGE,"E90.MirrorCS"),sQuery(id+"F0.wireOp",EDGE,"E76.MirrorCS"),sQuery(id+"F0.wireOp",EDGE,"E92.MirrorCS"),sQuery(id+"F0.wireOp",EDGE,"E63.MirrorC"),sQuery(id+"F0.wireOp",EDGE,"E64.MirrorCS"),sQuery(id+"F0.wireOp",EDGE,"E74.MirrorCS"),sQuery(id+"F0.wireOp",EDGE,"E96.MirrorCS"),sQuery(id+"F0.wireOp",EDGE,"E95.MirrorCS"),sQuery(id+"F0.wireOp",EDGE,"E93.MirrorCS"),sQuery(id+"F0.wireOp",EDGE,"E98.MirrorCS"),sQuery(id+"F0.wireOp",EDGE,"E94.MirrorCS"),sQuery(id+"F0.wireOp",EDGE,"E100.MirrorCS"),sQuery(id+"F0.wireOp",EDGE,"E97.MirrorCS"),sQuery(id+"F0.wireOp",EDGE,"E103.MirrorCS"),sQuery(id+"F0.wireOp",EDGE,"E113.MirrorCS"),sQuery(id+"F0.wireOp",EDGE,"E99.MirrorC"),sQuery(id+"F0.wireOp",EDGE,"E102.MirrorCS"),sQuery(id+"F0.wireOp",EDGE,"E106.MirrorCS"),sQuery(id+"F0.wireOp",EDGE,"E126.MirrorC"),sQuery(id+"F0.wireOp",EDGE,"E125.MirrorC"),sQuery(id+"F0.wireOp",EDGE,"E116.MirrorCS"),sQuery(id+"F0.wireOp",EDGE,"E115.MirrorCS"),sQuery(id+"F0.wireOp",EDGE,"E110.MirrorCS"),sQuery(id+"F0.wireOp",EDGE,"E101.MirrorCS"),sQuery(id+"F0.wireOp",EDGE,"E111.MirrorCS"),sQuery(id+"F0.wireOp",EDGE,"E119.MirrorCS"),sQuery(id+"F0.wireOp",EDGE,"E114.MirrorCS"),sQuery(id+"F0.wireOp",EDGE,"E104.MirrorCS"),sQuery(id+"F0.wireOp",EDGE,"E109.MirrorCS"),sQuery(id+"F0.wireOp",EDGE,"E105.MirrorCS"),sQuery(id+"F0.wireOp",EDGE,"E81.MirrorCS"),sQuery(id+"F0.wireOp",EDGE,"E120.MirrorCS"),sQuery(id+"F0.wireOp",EDGE,"E123.MirrorC"),sQuery(id+"F0.wireOp",EDGE,"E124.MirrorCS"),sQuery(id+"F0.wireOp",EDGE,"E122.MirrorCS"),sQuery(id+"F0.wireOp",EDGE,"E121.MirrorCS"),sQuery(id+"F0.wireOp",EDGE,"E108.MirrorCS"),sQuery(id+"F0.wireOp",EDGE,"E107.MirrorC"),sQuery(id+"F0.wireOp",EDGE,"E112.MirrorCS"),sQuery(id+"F0.wireOp",EDGE,"E118.MirrorCS"),sQuery(id+"F0.wireOp",EDGE,"E117.MirrorCS")])],"isStart":true});
            var Q293;
            Q293=makeQuery(id+"F1.opExtrude","CAP_EDGE",EDGE,{"disambiguationData":[OSD([sQuery(id+"F0.wireOp",EDGE,"E85.MirrorCS")])],"isStart":false});
            var Q294;
            Q294=makeQuery(id+"F1.opExtrude","CAP_EDGE",EDGE,{"disambiguationData":[OSD([sQuery(id+"F0.wireOp",EDGE,"E124.MirrorCS")])],"isStart":false});
            var Q295;
            Q295=makeQuery(id+"F1.opExtrude","CAP_EDGE",EDGE,{"disambiguationData":[OSD([sQuery(id+"F0.wireOp",EDGE,"E86.MirrorC")])],"isStart":false});
            var Q296;
            Q296=makeQuery(id+"F1.opExtrude","CAP_EDGE",EDGE,{"disambiguationData":[OSD([sQuery(id+"F0.wireOp",EDGE,"E63.MirrorC")])],"isStart":false});
            var Q297;
            Q297=makeQuery(id+"F1.opExtrude","CAP_EDGE",EDGE,{"disambiguationData":[OSD([sQuery(id+"F0.wireOp",EDGE,"E103.MirrorCS")])],"isStart":false});
            var Q298;
            Q298=makeQuery(id+"F1.opExtrude","CAP_EDGE",EDGE,{"disambiguationData":[OSD([sQuery(id+"F0.wireOp",EDGE,"E117.MirrorCS")])],"isStart":false});
            var Q299;
            Q299=makeQuery(id+"F1.opExtrude","CAP_EDGE",EDGE,{"disambiguationData":[OSD([sQuery(id+"F0.wireOp",EDGE,"E99.MirrorC")])],"isStart":false});
            var Q300;
            Q300=makeQuery(id+"F1.opExtrude","CAP_EDGE",EDGE,{"disambiguationData":[OSD([sQuery(id+"F0.wireOp",EDGE,"E102.MirrorCS")])],"isStart":true});
            var Q301;
            Q301=makeQuery(id+"F1.opExtrude","CAP_EDGE",EDGE,{"disambiguationData":[OSD([sQuery(id+"F0.wireOp",EDGE,"E75.MirrorCS")])],"isStart":false});
            var Q302;
            Q302=makeQuery(id+"F1.opExtrude","CAP_EDGE",EDGE,{"disambiguationData":[OSD([sQuery(id+"F0.wireOp",EDGE,"E73.MirrorCS"),sQuery(id+"F0.wireOp",EDGE,"E96.MirrorCS")])],"isStart":false});
            var Q303;
            Q303=makeQuery(id+"F1.opExtrude","CAP_EDGE",EDGE,{"disambiguationData":[OSD([sQuery(id+"F0.wireOp",EDGE,"E122.MirrorCS")])],"isStart":false});
            var Q304;
            Q304=makeQuery(id+"F1.opExtrude","CAP_EDGE",EDGE,{"disambiguationData":[OSD([sQuery(id+"F0.wireOp",EDGE,"E119.MirrorCS")])],"isStart":false});
            var Q305;
            Q305=makeQuery(id+"F1.opExtrude","SWEPT_EDGE",EDGE,{"disambiguationData":[OSD([sQuery(id+"F0.wireOp",EDGE,"E122.MirrorCS"),sQuery(id+"F0.wireOp",EDGE,"E112.MirrorCS")])]});
            var Q306;
            {var subQ0=sQuery(id+"F0.wireOp",EDGE,"E74.MirrorCS");Q306=makeQuery(id+"F1.opExtrude","CAP_EDGE",EDGE,{"disambiguationData":[OSD([subQ0]),TDD([makeQuery(id+"F0.imprint","IMPRINT",EDGE,{"disambiguationData":[TD([[makeQuery(id+"F0.imprint","INTERSECT",VERTEX,{"derivedFrom":[sQuery(id+"F0.wireOp",EDGE,"E76.MirrorCS"),subQ0]}),1.0]])],"derivedFrom":subQ0})])],"isStart":false});}
            var Q307;
            Q307=makeQuery(id+"F1.opExtrude","CAP_EDGE",EDGE,{"disambiguationData":[OSD([sQuery(id+"F0.wireOp",EDGE,"E88.MirrorCS")])],"isStart":false});
            var Q308;
            Q308=makeQuery(id+"F1.opExtrude","CAP_EDGE",EDGE,{"disambiguationData":[OSD([sQuery(id+"F0.wireOp",EDGE,"E123.MirrorC")])],"isStart":false});
            var Q309;
            Q309=makeQuery(id+"F1.opExtrude","CAP_EDGE",EDGE,{"disambiguationData":[OSD([sQuery(id+"F0.wireOp",EDGE,"E92.MirrorCS")])],"isStart":false});
            var Q310;
            Q310=makeQuery(id+"F1.opExtrude","CAP_EDGE",EDGE,{"disambiguationData":[OSD([sQuery(id+"F0.wireOp",EDGE,"E115.MirrorCS")])],"isStart":false});
            var Q311;
            Q311=makeQuery(id+"F1.opExtrude","CAP_EDGE",EDGE,{"disambiguationData":[OSD([sQuery(id+"F0.wireOp",EDGE,"E120.MirrorCS")])],"isStart":false});
            var Q312;
            Q312=makeQuery(id+"F1.opExtrude","SWEPT_EDGE",EDGE,{"disambiguationData":[OSD([sQuery(id+"F0.wireOp",EDGE,"E75.MirrorCS"),sQuery(id+"F0.wireOp",EDGE,"E112.MirrorCS")])]});
            var Q313;
            Q313=makeQuery(id+"F1.opExtrude","CAP_EDGE",EDGE,{"disambiguationData":[OSD([sQuery(id+"F0.wireOp",EDGE,"E105.MirrorCS")])],"isStart":true});
            var Q314;
            Q314=makeQuery(id+"F1.opExtrude","CAP_EDGE",EDGE,{"disambiguationData":[OSD([sQuery(id+"F0.wireOp",EDGE,"E126.MirrorC")])],"isStart":false});
            var Q315;
            Q315=makeQuery(id+"F1.opExtrude","CAP_EDGE",EDGE,{"disambiguationData":[OSD([sQuery(id+"F0.wireOp",EDGE,"E104.MirrorCS")])],"isStart":false});
            var Q316;
            Q316=makeQuery(id+"F1.opExtrude","CAP_EDGE",EDGE,{"disambiguationData":[OSD([sQuery(id+"F0.wireOp",EDGE,"E108.MirrorCS")])],"isStart":false});
            var Q317;
            Q317=makeQuery(id+"F1.opExtrude","CAP_EDGE",EDGE,{"disambiguationData":[OSD([sQuery(id+"F0.wireOp",EDGE,"E83.MirrorCS")])],"isStart":false});
            var Q318;
            Q318=makeQuery(id+"F1.opExtrude","CAP_EDGE",EDGE,{"disambiguationData":[OSD([sQuery(id+"F0.wireOp",EDGE,"E93.MirrorCS")])],"isStart":false});
            var Q319;
            Q319=makeQuery(id+"F1.opExtrude","SWEPT_EDGE",EDGE,{"disambiguationData":[OSD([sQuery(id+"F0.wireOp",EDGE,"E116.MirrorCS"),sQuery(id+"F0.wireOp",EDGE,"E118.MirrorCS")])]});
            var Q320;
            Q320=makeQuery(id+"F1.opExtrude","SWEPT_EDGE",EDGE,{"disambiguationData":[OSD([sQuery(id+"F0.wireOp",EDGE,"E113.MirrorCS"),sQuery(id+"F0.wireOp",EDGE,"E102.MirrorCS")])]});
            var Q321;
            Q321=makeQuery(id+"F1.opExtrude","SWEPT_EDGE",EDGE,{"disambiguationData":[OSD([sQuery(id+"F0.wireOp",EDGE,"E73.MirrorCS"),sQuery(id+"F0.wireOp",EDGE,"E85.MirrorCS")])]});
            var Q322;
            Q322=makeQuery(id+"F1.opExtrude","SWEPT_EDGE",EDGE,{"disambiguationData":[OSD([sQuery(id+"F0.wireOp",EDGE,"E83.MirrorCS"),sQuery(id+"F0.wireOp",EDGE,"E94.MirrorCS")])]});
            var Q323;
            Q323=makeQuery(id+"F1.opExtrude","CAP_EDGE",EDGE,{"disambiguationData":[OSD([sQuery(id+"F0.wireOp",EDGE,"E69.MirrorCS"),sQuery(id+"F0.wireOp",EDGE,"E79.MirrorCS"),sQuery(id+"F0.wireOp",EDGE,"E66.MirrorCS")])],"isStart":true});
            var Q324;
            Q324=makeQuery(id+"F1.opExtrude","CAP_EDGE",EDGE,{"disambiguationData":[OSD([sQuery(id+"F0.wireOp",EDGE,"E20")])],"isStart":true});
            var Q325;
            Q325=makeQuery(id+"F1.opExtrude","CAP_EDGE",EDGE,{"disambiguationData":[OSD([sQuery(id+"F0.wireOp",EDGE,"E51.0"),sQuery(id+"F0.wireOp",EDGE,"E54")])],"isStart":false});
            var Q326;
            Q326=makeQuery(id+"F1.opExtrude","CAP_EDGE",EDGE,{"disambiguationData":[OSD([sQuery(id+"F0.wireOp",EDGE,"E11")])],"isStart":false});
            var Q327;
            Q327=makeQuery(id+"F1.opExtrude","CAP_EDGE",EDGE,{"disambiguationData":[OSD([sQuery(id+"F0.wireOp",EDGE,"E37.0")])],"isStart":true});
            var Q328;
            Q328=makeQuery(id+"F1.opExtrude","CAP_EDGE",EDGE,{"disambiguationData":[OSD([sQuery(id+"F0.wireOp",EDGE,"E3")])],"isStart":false});
            var Q329;
            Q329=makeQuery(id+"F1.opExtrude","CAP_EDGE",EDGE,{"disambiguationData":[OSD([sQuery(id+"F0.wireOp",EDGE,"E19")])],"isStart":false});
            var Q330;
            Q330=makeQuery(id+"F1.opExtrude","CAP_EDGE",EDGE,{"disambiguationData":[OSD([sQuery(id+"F0.wireOp",EDGE,"E29")])],"isStart":false});
            var Q331;
            Q331=makeQuery(id+"F1.opExtrude","CAP_EDGE",EDGE,{"disambiguationData":[OSD([sQuery(id+"F0.wireOp",EDGE,"E49.0"),sQuery(id+"F0.wireOp",EDGE,"E53")])],"isStart":false});
            var Q332;
            Q332=makeQuery(id+"F1.opExtrude","CAP_EDGE",EDGE,{"disambiguationData":[OSD([sQuery(id+"F0.wireOp",EDGE,"E61.trimOffspring")])],"isStart":false});
            var Q333;
            {var subQ0=sQuery(id+"F0.wireOp",EDGE,"E9");Q333=makeQuery(id+"F1.opExtrude","CAP_EDGE",EDGE,{"disambiguationData":[OSD([subQ0]),TDD([makeQuery(id+"F0.imprint","IMPRINT",EDGE,{"disambiguationData":[TD([[makeQuery(id+"F0.imprint","INTERSECT",VERTEX,{"derivedFrom":[sQuery(id+"F0.wireOp",EDGE,"E0.3"),subQ0]}),1.0]])],"derivedFrom":subQ0})])],"isStart":false});}
            var Q334;
            Q334=makeQuery(id+"F1.opExtrude","CAP_EDGE",EDGE,{"disambiguationData":[OSD([sQuery(id+"F0.wireOp",EDGE,"E17")])],"isStart":false});
            var Q335;
            Q335=makeQuery(id+"F1.opExtrude","CAP_EDGE",EDGE,{"disambiguationData":[OSD([sQuery(id+"F0.wireOp",EDGE,"E27")])],"isStart":false});
            var Q336;
            Q336=makeQuery(id+"F1.opExtrude","CAP_EDGE",EDGE,{"disambiguationData":[OSD([sQuery(id+"F0.wireOp",EDGE,"E35.0"),sQuery(id+"F0.wireOp",EDGE,"E41"),sQuery(id+"F0.wireOp",EDGE,"E44")])],"isStart":false});
            var Q337;
            Q337=makeQuery(id+"F1.opExtrude","CAP_EDGE",EDGE,{"disambiguationData":[OSD([sQuery(id+"F0.wireOp",EDGE,"E1")])],"isStart":false});
            var Q338;
            Q338=makeQuery(id+"F1.opExtrude","CAP_EDGE",EDGE,{"disambiguationData":[OSD([sQuery(id+"F0.wireOp",EDGE,"E50.0"),sQuery(id+"F0.wireOp",EDGE,"E59")])],"isStart":false});
            var Q339;
            Q339=makeQuery(id+"F1.opExtrude","CAP_EDGE",EDGE,{"disambiguationData":[OSD([sQuery(id+"F0.wireOp",EDGE,"E62.trimOffspring")])],"isStart":false});
            var Q340;
            Q340=makeQuery(id+"F1.opExtrude","CAP_EDGE",EDGE,{"disambiguationData":[OSD([sQuery(id+"F0.wireOp",EDGE,"E36.0"),sQuery(id+"F0.wireOp",EDGE,"E42"),sQuery(id+"F0.wireOp",EDGE,"E43")])],"isStart":false});
            var Q341;
            Q341=makeQuery(id+"F1.opExtrude","CAP_EDGE",EDGE,{"disambiguationData":[OSD([sQuery(id+"F0.wireOp",EDGE,"E2")])],"isStart":false});
            var Q342;
            Q342=makeQuery(id+"F1.opExtrude","CAP_EDGE",EDGE,{"disambiguationData":[OSD([sQuery(id+"F0.wireOp",EDGE,"E10")])],"isStart":false});
            var Q343;
            Q343=makeQuery(id+"F1.opExtrude","CAP_EDGE",EDGE,{"disambiguationData":[OSD([sQuery(id+"F0.wireOp",EDGE,"E18")])],"isStart":false});
            var Q344;
            Q344=makeQuery(id+"F1.opExtrude","CAP_EDGE",EDGE,{"disambiguationData":[OSD([sQuery(id+"F0.wireOp",EDGE,"E28")])],"isStart":false});
            var Q345;
            Q345=makeQuery(id+"F1.opExtrude","SWEPT_EDGE",EDGE,{"disambiguationData":[OSD([sQuery(id+"F0.wireOp",EDGE,"E11"),sQuery(id+"F0.wireOp",EDGE,"E19")])]});
            var Q346;
            Q346=makeQuery(id+"F1.opExtrude","CAP_EDGE",EDGE,{"disambiguationData":[OSD([sQuery(id+"F0.wireOp",EDGE,"E60")])],"isStart":false});
            var Q347;
            Q347=makeQuery(id+"F1.opExtrude","CAP_EDGE",EDGE,{"disambiguationData":[OSD([sQuery(id+"F0.wireOp",EDGE,"E16")])],"isStart":false});
            var Q348;
            Q348=makeQuery(id+"F1.opExtrude","CAP_EDGE",EDGE,{"disambiguationData":[OSD([sQuery(id+"F0.wireOp",EDGE,"E26")])],"isStart":false});
            var Q349;
            Q349=makeQuery(id+"F1.opExtrude","CAP_EDGE",EDGE,{"disambiguationData":[OSD([sQuery(id+"F0.wireOp",EDGE,"E34")])],"isStart":false});
            var Q350;
            Q350=makeQuery(id+"F1.opExtrude","CAP_EDGE",EDGE,{"disambiguationData":[OSD([sQuery(id+"F0.wireOp",EDGE,"E48.0"),sQuery(id+"F0.wireOp",EDGE,"E52")])],"isStart":false});
            var Q351;
            Q351=makeQuery(id+"F1.opExtrude","SWEPT_EDGE",EDGE,{"disambiguationData":[OSD([sQuery(id+"F0.wireOp",EDGE,"E11"),sQuery(id+"F0.wireOp",EDGE,"E20")])]});
            var Q352;
            Q352=makeQuery(id+"F1.opExtrude","CAP_EDGE",EDGE,{"disambiguationData":[OSD([sQuery(id+"F0.wireOp",EDGE,"E0.5")])],"isStart":false});
            var Q353;
            {var subQ0=sQuery(id+"F0.wireOp",EDGE,"E9");Q353=makeQuery(id+"F1.opExtrude","CAP_EDGE",EDGE,{"disambiguationData":[OSD([subQ0]),TDD([makeQuery(id+"F0.imprint","IMPRINT",EDGE,{"disambiguationData":[TD([[makeQuery(id+"F0.imprint","INTERSECT",VERTEX,{"derivedFrom":[sQuery(id+"F0.wireOp",EDGE,"E0.4"),subQ0]}),-1.0]])],"derivedFrom":subQ0})])],"isStart":false});}
            var Q354;
            Q354=makeQuery(id+"F1.opExtrude","CAP_EDGE",EDGE,{"disambiguationData":[OSD([sQuery(id+"F0.wireOp",EDGE,"E58")])],"isStart":false});
            var Q355;
            Q355=makeQuery(id+"F1.opExtrude","CAP_EDGE",EDGE,{"disambiguationData":[OSD([sQuery(id+"F0.wireOp",EDGE,"E15")])],"isStart":false});
            var Q356;
            Q356=makeQuery(id+"F1.opExtrude","CAP_EDGE",EDGE,{"disambiguationData":[OSD([sQuery(id+"F0.wireOp",EDGE,"E24.trimOffspring")])],"isStart":false});
            var Q357;
            Q357=makeQuery(id+"F1.opExtrude","CAP_EDGE",EDGE,{"disambiguationData":[OSD([sQuery(id+"F0.wireOp",EDGE,"E33")])],"isStart":false});
            var Q358;
            Q358=makeQuery(id+"F1.opExtrude","CAP_EDGE",EDGE,{"disambiguationData":[OSD([sQuery(id+"F0.wireOp",EDGE,"E47.0")])],"isStart":false});
            var Q359;
            Q359=makeQuery(id+"F1.opExtrude","SWEPT_EDGE",EDGE,{"disambiguationData":[OSD([sQuery(id+"F0.wireOp",EDGE,"E10"),sQuery(id+"F0.wireOp",EDGE,"E14")])]});
            var Q360;
            Q360=makeQuery(id+"F1.opExtrude","CAP_EDGE",EDGE,{"disambiguationData":[OSD([sQuery(id+"F0.wireOp",EDGE,"E0.4")])],"isStart":false});
            var Q361;
            Q361=makeQuery(id+"F1.opExtrude","CAP_EDGE",EDGE,{"disambiguationData":[OSD([sQuery(id+"F0.wireOp",EDGE,"E8")])],"isStart":false});
            var Q362;
            Q362=makeQuery(id+"F1.opExtrude","CAP_EDGE",EDGE,{"disambiguationData":[OSD([sQuery(id+"F0.wireOp",EDGE,"E7")])],"isStart":false});
            var Q363;
            Q363=makeQuery(id+"F1.opExtrude","CAP_EDGE",EDGE,{"disambiguationData":[OSD([sQuery(id+"F0.wireOp",EDGE,"E32")])],"isStart":false});
            var Q364;
            Q364=makeQuery(id+"F1.opExtrude","SWEPT_EDGE",EDGE,{"disambiguationData":[OSD([sQuery(id+"F0.wireOp",EDGE,"E8"),sQuery(id+"F0.wireOp",EDGE,"E15")])]});
            var Q365;
            Q365=makeQuery(id+"F1.opExtrude","CAP_EDGE",EDGE,{"disambiguationData":[OSD([sQuery(id+"F0.wireOp",EDGE,"E14")])],"isStart":true});
            var Q366;
            Q366=makeQuery(id+"F1.opExtrude","CAP_EDGE",EDGE,{"disambiguationData":[OSD([sQuery(id+"F0.wireOp",EDGE,"E0.3")])],"isStart":true});
            var Q367;
            Q367=makeQuery(id+"F1.opExtrude","CAP_EDGE",EDGE,{"disambiguationData":[OSD([sQuery(id+"F0.wireOp",EDGE,"E31")])],"isStart":false});
            var Q368;
            Q368=makeQuery(id+"F1.opExtrude","CAP_EDGE",EDGE,{"disambiguationData":[OSD([sQuery(id+"F0.wireOp",EDGE,"E39.0"),sQuery(id+"F0.wireOp",EDGE,"E46")])],"isStart":false});
            var Q369;
            Q369=makeQuery(id+"F1.opExtrude","SWEPT_EDGE",EDGE,{"disambiguationData":[OSD([sQuery(id+"F0.wireOp",EDGE,"E40.0"),sQuery(id+"F0.wireOp",EDGE,"E44")])]});
            var Q370;
            Q370=makeQuery(id+"F1.opExtrude","CAP_EDGE",EDGE,{"disambiguationData":[OSD([sQuery(id+"F0.wireOp",EDGE,"E40.0"),sQuery(id+"F0.wireOp",EDGE,"E45")])],"isStart":true});
            var Q371;
            Q371=makeQuery(id+"F1.opExtrude","SWEPT_EDGE",EDGE,{"disambiguationData":[OSD([sQuery(id+"F0.wireOp",EDGE,"E7"),sQuery(id+"F0.wireOp",EDGE,"E18")])]});
            var Q372;
            Q372=makeQuery(id+"F1.opExtrude","CAP_EDGE",EDGE,{"disambiguationData":[OSD([sQuery(id+"F0.wireOp",EDGE,"E21")])],"isStart":false});
            var Q373;
            Q373=makeQuery(id+"F1.opExtrude","CAP_EDGE",EDGE,{"disambiguationData":[OSD([sQuery(id+"F0.wireOp",EDGE,"E56")])],"isStart":false});
            var Q374;
            Q374=makeQuery(id+"F1.opExtrude","CAP_EDGE",EDGE,{"disambiguationData":[OSD([sQuery(id+"F0.wireOp",EDGE,"E0.2")])],"isStart":false});
            var Q375;
            Q375=makeQuery(id+"F1.opExtrude","CAP_EDGE",EDGE,{"disambiguationData":[OSD([sQuery(id+"F0.wireOp",EDGE,"E6")])],"isStart":false});
            var Q376;
            Q376=makeQuery(id+"F1.opExtrude","CAP_EDGE",EDGE,{"disambiguationData":[OSD([sQuery(id+"F0.wireOp",EDGE,"E13")])],"isStart":false});
            var Q377;
            Q377=makeQuery(id+"F1.opExtrude","SWEPT_EDGE",EDGE,{"disambiguationData":[OSD([sQuery(id+"F0.wireOp",EDGE,"E8"),sQuery(id+"F0.wireOp",EDGE,"E16")])]});
            var Q378;
            Q378=makeQuery(id+"F1.opExtrude","CAP_EDGE",EDGE,{"disambiguationData":[OSD([sQuery(id+"F0.wireOp",EDGE,"E57.trimOffspring")])],"isStart":false});
            var Q379;
            Q379=makeQuery(id+"F1.opExtrude","SWEPT_EDGE",EDGE,{"disambiguationData":[OSD([sQuery(id+"F0.wireOp",EDGE,"E37.0"),sQuery(id+"F0.wireOp",EDGE,"E43")])]});
            var Q380;
            Q380=makeQuery(id+"F1.opExtrude","SWEPT_EDGE",EDGE,{"disambiguationData":[OSD([sQuery(id+"F0.wireOp",EDGE,"E0.5"),sQuery(id+"F0.wireOp",EDGE,"E14")])]});
            var Q381;
            Q381=makeQuery(id+"F1.opExtrude","SWEPT_EDGE",EDGE,{"disambiguationData":[OSD([sQuery(id+"F0.wireOp",EDGE,"E0.4"),sQuery(id+"F0.wireOp",EDGE,"E9")])]});
            var Q382;
            Q382=makeQuery(id+"F1.opExtrude","SWEPT_EDGE",EDGE,{"disambiguationData":[OSD([sQuery(id+"F0.wireOp",EDGE,"E0.2"),sQuery(id+"F0.wireOp",EDGE,"E16")])]});
            var Q383;
            Q383=makeQuery(id+"F1.opExtrude","SWEPT_EDGE",EDGE,{"disambiguationData":[OSD([sQuery(id+"F0.wireOp",EDGE,"E7"),sQuery(id+"F0.wireOp",EDGE,"E17")])]});
            var Q384;
            Q384=makeQuery(id+"F1.opExtrude","SWEPT_EDGE",EDGE,{"disambiguationData":[OSD([sQuery(id+"F0.wireOp",EDGE,"E0.5"),sQuery(id+"F0.wireOp",EDGE,"E2")])]});
            var Q385;
            Q385=makeQuery(id+"F1.opExtrude","SWEPT_EDGE",EDGE,{"disambiguationData":[OSD([sQuery(id+"F0.wireOp",EDGE,"E0.4"),sQuery(id+"F0.wireOp",EDGE,"E13")])]});
            var Q386;
            Q386=makeQuery(id+"F1.opExtrude","SWEPT_EDGE",EDGE,{"disambiguationData":[OSD([sQuery(id+"F0.wireOp",EDGE,"E0.3"),sQuery(id+"F0.wireOp",EDGE,"E15")])]});
            var Q387;
            Q387=makeQuery(id+"F1.opExtrude","SWEPT_EDGE",EDGE,{"disambiguationData":[OSD([sQuery(id+"F0.wireOp",EDGE,"E0.3"),sQuery(id+"F0.wireOp",EDGE,"E9")])]});
            var Q388;
            Q388=makeQuery(id+"F1.opExtrude","SWEPT_EDGE",EDGE,{"disambiguationData":[OSD([sQuery(id+"F0.wireOp",EDGE,"E0.1"),sQuery(id+"F0.wireOp",EDGE,"E1")])]});
            var Q389;
            Q389=makeQuery(id+"F1.opExtrude","SWEPT_EDGE",EDGE,{"disambiguationData":[OSD([sQuery(id+"F0.wireOp",EDGE,"E0.1"),sQuery(id+"F0.wireOp",EDGE,"E24.trimOffspring")])]});
            var Q390;
            Q390=makeQuery(id+"F1.opExtrude","CAP_FACE",FACE,{"disambiguationData":[OSD([sQuery(id+"F0.wireOp",EDGE,"E0.1"),sQuery(id+"F0.wireOp",EDGE,"E0.2"),sQuery(id+"F0.wireOp",EDGE,"E0.3"),sQuery(id+"F0.wireOp",EDGE,"E0.4"),sQuery(id+"F0.wireOp",EDGE,"E0.5"),sQuery(id+"F0.wireOp",EDGE,"E1"),sQuery(id+"F0.wireOp",EDGE,"E2"),sQuery(id+"F0.wireOp",EDGE,"E3"),sQuery(id+"F0.wireOp",EDGE,"E4"),sQuery(id+"F0.wireOp",EDGE,"E6"),sQuery(id+"F0.wireOp",EDGE,"E7"),sQuery(id+"F0.wireOp",EDGE,"E8"),sQuery(id+"F0.wireOp",EDGE,"E9"),sQuery(id+"F0.wireOp",EDGE,"E10"),sQuery(id+"F0.wireOp",EDGE,"E11"),sQuery(id+"F0.wireOp",EDGE,"E12"),sQuery(id+"F0.wireOp",EDGE,"E13"),sQuery(id+"F0.wireOp",EDGE,"E14"),sQuery(id+"F0.wireOp",EDGE,"E15"),sQuery(id+"F0.wireOp",EDGE,"E16"),sQuery(id+"F0.wireOp",EDGE,"E17"),sQuery(id+"F0.wireOp",EDGE,"E18"),sQuery(id+"F0.wireOp",EDGE,"E19"),sQuery(id+"F0.wireOp",EDGE,"E20"),sQuery(id+"F0.wireOp",EDGE,"E21"),sQuery(id+"F0.wireOp",EDGE,"E22"),sQuery(id+"F0.wireOp",EDGE,"E24.trimOffspring"),sQuery(id+"F0.wireOp",EDGE,"E26"),sQuery(id+"F0.wireOp",EDGE,"E27"),sQuery(id+"F0.wireOp",EDGE,"E28"),sQuery(id+"F0.wireOp",EDGE,"E29"),sQuery(id+"F0.wireOp",EDGE,"E30"),sQuery(id+"F0.wireOp",EDGE,"E31"),sQuery(id+"F0.wireOp",EDGE,"E32"),sQuery(id+"F0.wireOp",EDGE,"E33"),sQuery(id+"F0.wireOp",EDGE,"E34"),sQuery(id+"F0.wireOp",EDGE,"E35.0"),sQuery(id+"F0.wireOp",EDGE,"E36.0"),sQuery(id+"F0.wireOp",EDGE,"E37.0"),sQuery(id+"F0.wireOp",EDGE,"E38.0"),sQuery(id+"F0.wireOp",EDGE,"E39.0"),sQuery(id+"F0.wireOp",EDGE,"E40.0"),sQuery(id+"F0.wireOp",EDGE,"E41"),sQuery(id+"F0.wireOp",EDGE,"E42"),sQuery(id+"F0.wireOp",EDGE,"E43"),sQuery(id+"F0.wireOp",EDGE,"E44"),sQuery(id+"F0.wireOp",EDGE,"E45"),sQuery(id+"F0.wireOp",EDGE,"E46"),sQuery(id+"F0.wireOp",EDGE,"E47.0"),sQuery(id+"F0.wireOp",EDGE,"E48.0"),sQuery(id+"F0.wireOp",EDGE,"E49.0"),sQuery(id+"F0.wireOp",EDGE,"E50.0"),sQuery(id+"F0.wireOp",EDGE,"E51.0"),sQuery(id+"F0.wireOp",EDGE,"E52"),sQuery(id+"F0.wireOp",EDGE,"E53"),sQuery(id+"F0.wireOp",EDGE,"E54"),sQuery(id+"F0.wireOp",EDGE,"E55.trimOffspring"),sQuery(id+"F0.wireOp",EDGE,"E56"),sQuery(id+"F0.wireOp",EDGE,"E57.trimOffspring"),sQuery(id+"F0.wireOp",EDGE,"E58"),sQuery(id+"F0.wireOp",EDGE,"E59"),sQuery(id+"F0.wireOp",EDGE,"E60"),sQuery(id+"F0.wireOp",EDGE,"E61.trimOffspring"),sQuery(id+"F0.wireOp",EDGE,"E62.trimOffspring")])],"isStart":true});
            var Q391;
            Q391=makeQuery(id+"F1.opExtrude","SWEPT_EDGE",EDGE,{"disambiguationData":[OSD([sQuery(id+"F0.wireOp",EDGE,"E0.2"),sQuery(id+"F0.wireOp",EDGE,"E57.trimOffspring")])]});
            var Q392;
            Q392=makeQuery(id+"F1.opExtrude","SWEPT_EDGE",EDGE,{"disambiguationData":[OSD([sQuery(id+"F0.wireOp",EDGE,"E4"),sQuery(id+"F0.wireOp",EDGE,"E60")])]});
            var Q393;
            Q393=makeQuery(id+"F1.opExtrude","CAP_EDGE",EDGE,{"disambiguationData":[OSD([sQuery(id+"F0.wireOp",EDGE,"E30")])],"isStart":false});
            var Q394;
            Q394=makeQuery(id+"F1.opExtrude","CAP_EDGE",EDGE,{"disambiguationData":[OSD([sQuery(id+"F0.wireOp",EDGE,"E38.0")])],"isStart":false});
            var Q395;
            Q395=makeQuery(id+"F1.opExtrude","CAP_EDGE",EDGE,{"disambiguationData":[OSD([sQuery(id+"F0.wireOp",EDGE,"E55.trimOffspring")])],"isStart":false});
            var Q396;
            Q396=makeQuery(id+"F1.opExtrude","SWEPT_EDGE",EDGE,{"disambiguationData":[OSD([sQuery(id+"F0.wireOp",EDGE,"E2"),sQuery(id+"F0.wireOp",EDGE,"E62.trimOffspring")])]});
            var Q397;
            Q397=makeQuery(id+"F1.opExtrude","CAP_EDGE",EDGE,{"disambiguationData":[OSD([sQuery(id+"F0.wireOp",EDGE,"E0.1")])],"isStart":false});
            var Q398;
            Q398=makeQuery(id+"F1.opExtrude","CAP_EDGE",EDGE,{"disambiguationData":[OSD([sQuery(id+"F0.wireOp",EDGE,"E4")])],"isStart":false});
            var Q399;
            Q399=makeQuery(id+"F1.opExtrude","CAP_EDGE",EDGE,{"disambiguationData":[OSD([sQuery(id+"F0.wireOp",EDGE,"E12")])],"isStart":false});
            var Q400;
            Q400=makeQuery(id+"F1.opExtrude","SWEPT_EDGE",EDGE,{"disambiguationData":[OSD([sQuery(id+"F0.wireOp",EDGE,"E3"),sQuery(id+"F0.wireOp",EDGE,"E4")])]});
            var Q401;
            Q401=makeQuery(id+"F1.opExtrude","SWEPT_EDGE",EDGE,{"disambiguationData":[OSD([sQuery(id+"F0.wireOp",EDGE,"E1"),sQuery(id+"F0.wireOp",EDGE,"E60")])]});
            var Q402;
            Q402=makeQuery(id+"F1.opExtrude","SWEPT_EDGE",EDGE,{"disambiguationData":[OSD([sQuery(id+"F0.wireOp",EDGE,"E3"),sQuery(id+"F0.wireOp",EDGE,"E6")])]});
            var Q403;
            Q403=makeQuery(id+"F2.opExtrude","SWEPT_FACE",FACE,{"disambiguationData":[OSD([sQuery(id+"F0.wireOp",EDGE,"E22")])]});
            var Q404;
            Q404=makeQuery(id+"F2.opExtrude","SWEPT_FACE",FACE,{"disambiguationData":[OSD([sQuery(id+"F0.wireOp",EDGE,"E21")])]});
            var Q405;
            Q405=makeQuery(id+"F2.opExtrude","SWEPT_FACE",FACE,{"disambiguationData":[OSD([sQuery(id+"F0.wireOp",EDGE,"E65.MirrorCS")])]});
            var Q406;
            Q406=makeQuery(id+"F1.opExtrude","SWEPT_EDGE",EDGE,{"disambiguationData":[OSD([sQuery(id+"F0.wireOp",EDGE,"E68.MirrorCS"),sQuery(id+"F0.wireOp",EDGE,"E89.MirrorCS")])]});
            var Q407;
            Q407=makeQuery(id+"F1.opExtrude","SWEPT_EDGE",EDGE,{"disambiguationData":[OSD([sQuery(id+"F0.wireOp",EDGE,"E72.MirrorCS"),sQuery(id+"F0.wireOp",EDGE,"E110.MirrorCS")])]});
            var Q408;
            Q408=makeQuery(id+"F1.opExtrude","SWEPT_EDGE",EDGE,{"disambiguationData":[OSD([sQuery(id+"F0.wireOp",EDGE,"E92.MirrorCS"),sQuery(id+"F0.wireOp",EDGE,"E93.MirrorCS")])]});
            var Q409;
            Q409=makeQuery(id+"F1.opExtrude","SWEPT_EDGE",EDGE,{"disambiguationData":[OSD([sQuery(id+"F0.wireOp",EDGE,"E101.MirrorCS"),sQuery(id+"F0.wireOp",EDGE,"E111.MirrorCS")])]});
            var Q410;
            Q410=makeQuery(id+"F1.opExtrude","SWEPT_EDGE",EDGE,{"disambiguationData":[OSD([sQuery(id+"F0.wireOp",EDGE,"E95.MirrorCS"),sQuery(id+"F0.wireOp",EDGE,"E124.MirrorCS")])]});
            var Q411;
            Q411=makeQuery(id+"F1.opExtrude","SWEPT_EDGE",EDGE,{"disambiguationData":[OSD([sQuery(id+"F0.wireOp",EDGE,"E114.MirrorCS"),sQuery(id+"F0.wireOp",EDGE,"E104.MirrorCS")])]});
            var Q412;
            Q412=makeQuery(id+"F1.opExtrude","SWEPT_EDGE",EDGE,{"disambiguationData":[OSD([sQuery(id+"F0.wireOp",EDGE,"E82.MirrorCS"),sQuery(id+"F0.wireOp",EDGE,"E90.MirrorCS")])]});
            var Q413;
            Q413=makeQuery(id+"F1.opExtrude","SWEPT_EDGE",EDGE,{"disambiguationData":[OSD([sQuery(id+"F0.wireOp",EDGE,"E105.MirrorCS"),sQuery(id+"F0.wireOp",EDGE,"E108.MirrorCS")])]});
            var Q414;
            Q414=makeQuery(id+"F1.opExtrude","SWEPT_EDGE",EDGE,{"disambiguationData":[OSD([sQuery(id+"F0.wireOp",EDGE,"E87.MirrorCS"),sQuery(id+"F0.wireOp",EDGE,"E114.MirrorCS")])]});
            var Q415;
            Q415=makeQuery(id+"F1.opExtrude","SWEPT_EDGE",EDGE,{"disambiguationData":[OSD([sQuery(id+"F0.wireOp",EDGE,"E98.MirrorCS"),sQuery(id+"F0.wireOp",EDGE,"E106.MirrorCS")])]});
            var Q416;
            Q416=makeQuery(id+"F1.opExtrude","SWEPT_EDGE",EDGE,{"disambiguationData":[OSD([sQuery(id+"F0.wireOp",EDGE,"E70.MirrorCS"),sQuery(id+"F0.wireOp",EDGE,"E65.MirrorCS")])]});
            var Q417;
            Q417=makeQuery(id+"F1.opExtrude","SWEPT_EDGE",EDGE,{"disambiguationData":[OSD([sQuery(id+"F0.wireOp",EDGE,"E122.MirrorCS"),sQuery(id+"F0.wireOp",EDGE,"E108.MirrorCS")])]});
            var Q418;
            Q418=makeQuery(id+"F1.opExtrude","SWEPT_EDGE",EDGE,{"disambiguationData":[OSD([sQuery(id+"F0.wireOp",EDGE,"E94.MirrorCS"),sQuery(id+"F0.wireOp",EDGE,"E121.MirrorCS")])]});
            var Q419;
            Q419=makeQuery(id+"F1.opExtrude","SWEPT_EDGE",EDGE,{"disambiguationData":[OSD([sQuery(id+"F0.wireOp",EDGE,"E120.MirrorCS"),sQuery(id+"F0.wireOp",EDGE,"E117.MirrorCS")])]});
            var Q420;
            Q420=makeQuery(id+"F1.opExtrude","SWEPT_EDGE",EDGE,{"disambiguationData":[OSD([sQuery(id+"F0.wireOp",EDGE,"E82.MirrorCS"),sQuery(id+"F0.wireOp",EDGE,"E116.MirrorCS")])]});
            var Q421;
            Q421=makeQuery(id+"F1.opExtrude","SWEPT_EDGE",EDGE,{"disambiguationData":[OSD([sQuery(id+"F0.wireOp",EDGE,"E74.MirrorCS"),sQuery(id+"F0.wireOp",EDGE,"E95.MirrorCS")])]});
            var Q422;
            Q422=makeQuery(id+"F1.opExtrude","SWEPT_EDGE",EDGE,{"disambiguationData":[OSD([sQuery(id+"F0.wireOp",EDGE,"E109.MirrorCS"),sQuery(id+"F0.wireOp",EDGE,"E81.MirrorCS")])]});
            var Q423;
            Q423=makeQuery(id+"F1.opExtrude","SWEPT_EDGE",EDGE,{"disambiguationData":[OSD([sQuery(id+"F0.wireOp",EDGE,"E87.MirrorCS"),sQuery(id+"F0.wireOp",EDGE,"E115.MirrorCS")])]});
            var Q424;
            Q424=makeQuery(id+"F1.opExtrude","SWEPT_EDGE",EDGE,{"disambiguationData":[OSD([sQuery(id+"F0.wireOp",EDGE,"E93.MirrorCS"),sQuery(id+"F0.wireOp",EDGE,"E121.MirrorCS")])]});
            var Q425;
            Q425=makeQuery(id+"F1.opExtrude","SWEPT_EDGE",EDGE,{"disambiguationData":[OSD([sQuery(id+"F0.wireOp",EDGE,"E100.MirrorCS"),sQuery(id+"F0.wireOp",EDGE,"E124.MirrorCS")])]});
            var Q426;
            Q426=makeQuery(id+"F1.opExtrude","SWEPT_EDGE",EDGE,{"disambiguationData":[OSD([sQuery(id+"F0.wireOp",EDGE,"E88.MirrorCS"),sQuery(id+"F0.wireOp",EDGE,"E71.MirrorCS")])]});
            var Q427;
            Q427=makeQuery(id+"F1.opExtrude","SWEPT_EDGE",EDGE,{"disambiguationData":[OSD([sQuery(id+"F0.wireOp",EDGE,"E74.MirrorCS"),sQuery(id+"F0.wireOp",EDGE,"E100.MirrorCS")])]});
            var Q428;
            Q428=makeQuery(id+"F1.opExtrude","SWEPT_EDGE",EDGE,{"disambiguationData":[OSD([sQuery(id+"F0.wireOp",EDGE,"E66.MirrorCS"),sQuery(id+"F0.wireOp",EDGE,"E80.MirrorCS")])]});
            var Q429;
            Q429=makeQuery(id+"F1.opExtrude","CAP_EDGE",EDGE,{"disambiguationData":[OSD([sQuery(id+"F0.wireOp",EDGE,"E65.MirrorCS")])],"isStart":false});
            var Q430;
            Q430=makeQuery(id+"F1.opExtrude","SWEPT_EDGE",EDGE,{"disambiguationData":[OSD([sQuery(id+"F0.wireOp",EDGE,"E67.MirrorCS"),sQuery(id+"F0.wireOp",EDGE,"E65.MirrorCS")])]});
            var Q431;
            Q431=makeQuery(id+"F1.opExtrude","SWEPT_EDGE",EDGE,{"disambiguationData":[OSD([sQuery(id+"F0.wireOp",EDGE,"E9"),sQuery(id+"F0.wireOp",EDGE,"E20")])]});
            var Q432;
            Q432=makeQuery(id+"F1.opExtrude","SWEPT_EDGE",EDGE,{"disambiguationData":[OSD([sQuery(id+"F0.wireOp",EDGE,"E58"),sQuery(id+"F0.wireOp",EDGE,"E59")])]});
            var Q433;
            Q433=makeQuery(id+"F1.opExtrude","SWEPT_EDGE",EDGE,{"disambiguationData":[OSD([sQuery(id+"F0.wireOp",EDGE,"E54"),sQuery(id+"F0.wireOp",EDGE,"E58")])]});
            var Q434;
            Q434=makeQuery(id+"F1.opExtrude","SWEPT_EDGE",EDGE,{"disambiguationData":[OSD([sQuery(id+"F0.wireOp",EDGE,"E18"),sQuery(id+"F0.wireOp",EDGE,"E24.trimOffspring")])]});
            var Q435;
            Q435=makeQuery(id+"F1.opExtrude","SWEPT_EDGE",EDGE,{"disambiguationData":[OSD([sQuery(id+"F0.wireOp",EDGE,"E9"),sQuery(id+"F0.wireOp",EDGE,"E19")])]});
            var Q436;
            Q436=makeQuery(id+"F1.opExtrude","SWEPT_EDGE",EDGE,{"disambiguationData":[OSD([sQuery(id+"F0.wireOp",EDGE,"E53"),sQuery(id+"F0.wireOp",EDGE,"E61.trimOffspring")])]});
            var Q437;
            Q437=makeQuery(id+"F1.opExtrude","SWEPT_EDGE",EDGE,{"disambiguationData":[OSD([sQuery(id+"F0.wireOp",EDGE,"E12"),sQuery(id+"F0.wireOp",EDGE,"E21")])]});
            var Q438;
            Q438=makeQuery(id+"F1.opExtrude","SWEPT_EDGE",EDGE,{"disambiguationData":[OSD([sQuery(id+"F0.wireOp",EDGE,"E49.0"),sQuery(id+"F0.wireOp",EDGE,"E50.0")])]});
            var Q439;
            Q439=makeQuery(id+"F1.opExtrude","SWEPT_EDGE",EDGE,{"disambiguationData":[OSD([sQuery(id+"F0.wireOp",EDGE,"E47.0"),sQuery(id+"F0.wireOp",EDGE,"E48.0")])]});
            var Q440;
            Q440=makeQuery(id+"F1.opExtrude","SWEPT_EDGE",EDGE,{"disambiguationData":[OSD([sQuery(id+"F0.wireOp",EDGE,"E17"),sQuery(id+"F0.wireOp",EDGE,"E57.trimOffspring")])]});
            var Q441;
            Q441=makeQuery(id+"F1.opExtrude","SWEPT_EDGE",EDGE,{"disambiguationData":[OSD([sQuery(id+"F0.wireOp",EDGE,"E52"),sQuery(id+"F0.wireOp",EDGE,"E61.trimOffspring")])]});
            var Q442;
            Q442=makeQuery(id+"F1.opExtrude","SWEPT_EDGE",EDGE,{"disambiguationData":[OSD([sQuery(id+"F0.wireOp",EDGE,"E10"),sQuery(id+"F0.wireOp",EDGE,"E13")])]});
            var Q443;
            Q443=makeQuery(id+"F1.opExtrude","SWEPT_EDGE",EDGE,{"disambiguationData":[OSD([sQuery(id+"F0.wireOp",EDGE,"E45"),sQuery(id+"F0.wireOp",EDGE,"E56")])]});
            var Q444;
            Q444=makeQuery(id+"F1.opExtrude","SWEPT_EDGE",EDGE,{"disambiguationData":[OSD([sQuery(id+"F0.wireOp",EDGE,"E47.0"),sQuery(id+"F0.wireOp",EDGE,"E51.0")])]});
            var Q445;
            Q445=makeQuery(id+"F1.opExtrude","SWEPT_EDGE",EDGE,{"disambiguationData":[OSD([sQuery(id+"F0.wireOp",EDGE,"E46"),sQuery(id+"F0.wireOp",EDGE,"E56")])]});
            var Q446;
            Q446=makeQuery(id+"F1.opExtrude","SWEPT_EDGE",EDGE,{"disambiguationData":[OSD([sQuery(id+"F0.wireOp",EDGE,"E42"),sQuery(id+"F0.wireOp",EDGE,"E55.trimOffspring")])]});
            var Q447;
            Q447=makeQuery(id+"F1.opExtrude","CAP_EDGE",EDGE,{"disambiguationData":[OSD([sQuery(id+"F0.wireOp",EDGE,"E22")])],"isStart":false});
            var Q448;
            Q448=makeQuery(id+"F1.opExtrude","SWEPT_EDGE",EDGE,{"disambiguationData":[OSD([sQuery(id+"F0.wireOp",EDGE,"E38.0"),sQuery(id+"F0.wireOp",EDGE,"E39.0")])]});
            var Q449;
            Q449=makeQuery(id+"F1.opExtrude","SWEPT_EDGE",EDGE,{"disambiguationData":[OSD([sQuery(id+"F0.wireOp",EDGE,"E37.0"),sQuery(id+"F0.wireOp",EDGE,"E38.0")])]});
            var Q450;
            Q450=makeQuery(id+"F1.opExtrude","SWEPT_EDGE",EDGE,{"disambiguationData":[OSD([sQuery(id+"F0.wireOp",EDGE,"E41"),sQuery(id+"F0.wireOp",EDGE,"E55.trimOffspring")])]});
            var Q451;
            Q451=makeQuery(id+"F1.opExtrude","SWEPT_EDGE",EDGE,{"disambiguationData":[OSD([sQuery(id+"F0.wireOp",EDGE,"E6"),sQuery(id+"F0.wireOp",EDGE,"E22")])]});
            var Q452;
            Q452=makeQuery(id+"F1.opExtrude","SWEPT_EDGE",EDGE,{"disambiguationData":[OSD([sQuery(id+"F0.wireOp",EDGE,"E21"),sQuery(id+"F0.wireOp",EDGE,"E62.trimOffspring")])]});
            var Q453;
            Q453=makeQuery(id+"F2.opExtrude","CAP_EDGE",EDGE,{"disambiguationData":[OSD([sQuery(id+"F0.wireOp",EDGE,"E19")])],"isStart":false});
            var Q454;
            Q454=makeQuery(id+"F2.opExtrude","CAP_EDGE",EDGE,{"disambiguationData":[OSD([sQuery(id+"F0.wireOp",EDGE,"E7")])],"isStart":false});
            var Q455;
            Q455=makeQuery(id+"F2.opExtrude","SWEPT_EDGE",EDGE,{"disambiguationData":[OSD([sQuery(id+"F0.wireOp",EDGE,"E40.0"),sQuery(id+"F0.wireOp",EDGE,"E44")])]});
            var Q456;
            Q456=makeQuery(id+"F2.opExtrude","CAP_EDGE",EDGE,{"disambiguationData":[OSD([sQuery(id+"F0.wireOp",EDGE,"E11")])],"isStart":false});
            var Q457;
            Q457=makeQuery(id+"F2.opExtrude","CAP_EDGE",EDGE,{"disambiguationData":[OSD([sQuery(id+"F0.wireOp",EDGE,"E20")])],"isStart":true});
            var Q458;
            Q458=makeQuery(id+"F2.opExtrude","CAP_EDGE",EDGE,{"disambiguationData":[OSD([sQuery(id+"F0.wireOp",EDGE,"E26")])],"isStart":false});
            var Q459;
            Q459=makeQuery(id+"F2.opExtrude","CAP_EDGE",EDGE,{"disambiguationData":[OSD([sQuery(id+"F0.wireOp",EDGE,"E32")])],"isStart":false});
            var Q460;
            Q460=makeQuery(id+"F2.opExtrude","CAP_EDGE",EDGE,{"disambiguationData":[OSD([sQuery(id+"F0.wireOp",EDGE,"E37.0")])],"isStart":true});
            var Q461;
            Q461=makeQuery(id+"F2.opExtrude","CAP_EDGE",EDGE,{"disambiguationData":[OSD([sQuery(id+"F0.wireOp",EDGE,"E29")])],"isStart":false});
            var Q462;
            Q462=makeQuery(id+"F2.opExtrude","CAP_EDGE",EDGE,{"disambiguationData":[OSD([sQuery(id+"F0.wireOp",EDGE,"E51.0"),sQuery(id+"F0.wireOp",EDGE,"E54")])],"isStart":false});
            var Q463;
            Q463=makeQuery(id+"F2.opExtrude","CAP_EDGE",EDGE,{"disambiguationData":[OSD([sQuery(id+"F0.wireOp",EDGE,"E3")])],"isStart":false});
            var Q464;
            Q464=makeQuery(id+"F2.opExtrude","CAP_EDGE",EDGE,{"disambiguationData":[OSD([sQuery(id+"F0.wireOp",EDGE,"E36.0"),sQuery(id+"F0.wireOp",EDGE,"E42"),sQuery(id+"F0.wireOp",EDGE,"E43")])],"isStart":false});
            var Q465;
            Q465=makeQuery(id+"F2.opExtrude","CAP_EDGE",EDGE,{"disambiguationData":[OSD([sQuery(id+"F0.wireOp",EDGE,"E62.trimOffspring")])],"isStart":false});
            var Q466;
            Q466=makeQuery(id+"F2.opExtrude","CAP_EDGE",EDGE,{"disambiguationData":[OSD([sQuery(id+"F0.wireOp",EDGE,"E18")])],"isStart":false});
            var Q467;
            Q467=makeQuery(id+"F2.opExtrude","CAP_EDGE",EDGE,{"disambiguationData":[OSD([sQuery(id+"F0.wireOp",EDGE,"E2")])],"isStart":false});
            var Q468;
            Q468=makeQuery(id+"F2.opExtrude","CAP_EDGE",EDGE,{"disambiguationData":[OSD([sQuery(id+"F0.wireOp",EDGE,"E50.0"),sQuery(id+"F0.wireOp",EDGE,"E59")])],"isStart":false});
            var Q469;
            Q469=makeQuery(id+"F2.opExtrude","CAP_EDGE",EDGE,{"disambiguationData":[OSD([sQuery(id+"F0.wireOp",EDGE,"E10")])],"isStart":false});
            var Q470;
            Q470=makeQuery(id+"F2.opExtrude","CAP_EDGE",EDGE,{"disambiguationData":[OSD([sQuery(id+"F0.wireOp",EDGE,"E28")])],"isStart":false});
            var Q471;
            Q471=makeQuery(id+"F2.opExtrude","CAP_EDGE",EDGE,{"disambiguationData":[OSD([sQuery(id+"F0.wireOp",EDGE,"E61.trimOffspring")])],"isStart":false});
            var Q472;
            Q472=makeQuery(id+"F2.opExtrude","CAP_EDGE",EDGE,{"disambiguationData":[OSD([sQuery(id+"F0.wireOp",EDGE,"E60")])],"isStart":false});
            var Q473;
            {var subQ0=sQuery(id+"F0.wireOp",EDGE,"E9");Q473=makeQuery(id+"F2.opExtrude","CAP_EDGE",EDGE,{"disambiguationData":[OSD([subQ0]),TDD([makeQuery(id+"F0.imprint","IMPRINT",EDGE,{"disambiguationData":[TD([[makeQuery(id+"F0.imprint","INTERSECT",VERTEX,{"derivedFrom":[sQuery(id+"F0.wireOp",EDGE,"E0.4"),subQ0]}),-1.0]])],"derivedFrom":subQ0})])],"isStart":false});}
            var Q474;
            Q474=makeQuery(id+"F2.opExtrude","CAP_EDGE",EDGE,{"disambiguationData":[OSD([sQuery(id+"F0.wireOp",EDGE,"E0.5")])],"isStart":false});
            var Q475;
            Q475=makeQuery(id+"F2.opExtrude","SWEPT_EDGE",EDGE,{"disambiguationData":[OSD([sQuery(id+"F0.wireOp",EDGE,"E11"),sQuery(id+"F0.wireOp",EDGE,"E19")])]});
            var Q476;
            Q476=makeQuery(id+"F2.opExtrude","CAP_EDGE",EDGE,{"disambiguationData":[OSD([sQuery(id+"F0.wireOp",EDGE,"E34")])],"isStart":false});
            var Q477;
            Q477=makeQuery(id+"F2.opExtrude","CAP_EDGE",EDGE,{"disambiguationData":[OSD([sQuery(id+"F0.wireOp",EDGE,"E1")])],"isStart":false});
            var Q478;
            Q478=makeQuery(id+"F2.opExtrude","CAP_EDGE",EDGE,{"disambiguationData":[OSD([sQuery(id+"F0.wireOp",EDGE,"E16")])],"isStart":false});
            var Q479;
            Q479=makeQuery(id+"F2.opExtrude","CAP_EDGE",EDGE,{"disambiguationData":[OSD([sQuery(id+"F0.wireOp",EDGE,"E57.trimOffspring")])],"isStart":false});
            var Q480;
            Q480=makeQuery(id+"F2.opExtrude","CAP_EDGE",EDGE,{"disambiguationData":[OSD([sQuery(id+"F0.wireOp",EDGE,"E48.0"),sQuery(id+"F0.wireOp",EDGE,"E52")])],"isStart":false});
            var Q481;
            Q481=makeQuery(id+"F2.opExtrude","SWEPT_EDGE",EDGE,{"disambiguationData":[OSD([sQuery(id+"F0.wireOp",EDGE,"E11"),sQuery(id+"F0.wireOp",EDGE,"E20")])]});
            var Q482;
            Q482=makeQuery(id+"F2.opExtrude","CAP_EDGE",EDGE,{"disambiguationData":[OSD([sQuery(id+"F0.wireOp",EDGE,"E49.0"),sQuery(id+"F0.wireOp",EDGE,"E53")])],"isStart":false});
            var Q483;
            {var subQ0=sQuery(id+"F0.wireOp",EDGE,"E9");Q483=makeQuery(id+"F2.opExtrude","CAP_EDGE",EDGE,{"disambiguationData":[OSD([subQ0]),TDD([makeQuery(id+"F0.imprint","IMPRINT",EDGE,{"disambiguationData":[TD([[makeQuery(id+"F0.imprint","INTERSECT",VERTEX,{"derivedFrom":[sQuery(id+"F0.wireOp",EDGE,"E0.3"),subQ0]}),1.0]])],"derivedFrom":subQ0})])],"isStart":false});}
            var Q484;
            Q484=makeQuery(id+"F2.opExtrude","CAP_EDGE",EDGE,{"disambiguationData":[OSD([sQuery(id+"F0.wireOp",EDGE,"E27")])],"isStart":false});
            var Q485;
            Q485=makeQuery(id+"F2.opExtrude","CAP_EDGE",EDGE,{"disambiguationData":[OSD([sQuery(id+"F0.wireOp",EDGE,"E35.0"),sQuery(id+"F0.wireOp",EDGE,"E41"),sQuery(id+"F0.wireOp",EDGE,"E44")])],"isStart":false});
            var Q486;
            Q486=makeQuery(id+"F2.opExtrude","CAP_EDGE",EDGE,{"disambiguationData":[OSD([sQuery(id+"F0.wireOp",EDGE,"E17")])],"isStart":false});
            var Q487;
            Q487=makeQuery(id+"F2.opExtrude","SWEPT_EDGE",EDGE,{"disambiguationData":[OSD([sQuery(id+"F0.wireOp",EDGE,"E8"),sQuery(id+"F0.wireOp",EDGE,"E15")])]});
            var Q488;
            Q488=makeQuery(id+"F2.opExtrude","CAP_EDGE",EDGE,{"disambiguationData":[OSD([sQuery(id+"F0.wireOp",EDGE,"E40.0"),sQuery(id+"F0.wireOp",EDGE,"E45")])],"isStart":true});
            var Q489;
            Q489=makeQuery(id+"F2.opExtrude","CAP_EDGE",EDGE,{"disambiguationData":[OSD([sQuery(id+"F0.wireOp",EDGE,"E14")])],"isStart":true});
            var Q490;
            Q490=makeQuery(id+"F2.opExtrude","CAP_EDGE",EDGE,{"disambiguationData":[OSD([sQuery(id+"F0.wireOp",EDGE,"E0.3")])],"isStart":true});
            var Q491;
            Q491=makeQuery(id+"F2.opExtrude","SWEPT_EDGE",EDGE,{"disambiguationData":[OSD([sQuery(id+"F0.wireOp",EDGE,"E7"),sQuery(id+"F0.wireOp",EDGE,"E18")])]});
            var Q492;
            Q492=makeQuery(id+"F2.opExtrude","CAP_EDGE",EDGE,{"disambiguationData":[OSD([sQuery(id+"F0.wireOp",EDGE,"E56")])],"isStart":false});
            var Q493;
            Q493=makeQuery(id+"F2.opExtrude","CAP_EDGE",EDGE,{"disambiguationData":[OSD([sQuery(id+"F0.wireOp",EDGE,"E39.0"),sQuery(id+"F0.wireOp",EDGE,"E46")])],"isStart":false});
            var Q494;
            Q494=makeQuery(id+"F2.opExtrude","CAP_EDGE",EDGE,{"disambiguationData":[OSD([sQuery(id+"F0.wireOp",EDGE,"E31")])],"isStart":false});
            var Q495;
            Q495=makeQuery(id+"F2.opExtrude","CAP_EDGE",EDGE,{"disambiguationData":[OSD([sQuery(id+"F0.wireOp",EDGE,"E21")])],"isStart":false});
            var Q496;
            Q496=makeQuery(id+"F2.opExtrude","CAP_EDGE",EDGE,{"disambiguationData":[OSD([sQuery(id+"F0.wireOp",EDGE,"E13")])],"isStart":false});
            var Q497;
            Q497=makeQuery(id+"F2.opExtrude","CAP_EDGE",EDGE,{"disambiguationData":[OSD([sQuery(id+"F0.wireOp",EDGE,"E6")])],"isStart":false});
            var Q498;
            Q498=makeQuery(id+"F2.opExtrude","CAP_EDGE",EDGE,{"disambiguationData":[OSD([sQuery(id+"F0.wireOp",EDGE,"E0.2")])],"isStart":false});
            var Q499;
            Q499=makeQuery(id+"F2.opExtrude","SWEPT_EDGE",EDGE,{"disambiguationData":[OSD([sQuery(id+"F0.wireOp",EDGE,"E37.0"),sQuery(id+"F0.wireOp",EDGE,"E43")])]});
            var Q500;
            Q500=makeQuery(id+"F2.opExtrude","CAP_EDGE",EDGE,{"disambiguationData":[OSD([sQuery(id+"F0.wireOp",EDGE,"E55.trimOffspring")])],"isStart":false});
            var Q501;
            Q501=makeQuery(id+"F2.opExtrude","CAP_EDGE",EDGE,{"disambiguationData":[OSD([sQuery(id+"F0.wireOp",EDGE,"E38.0")])],"isStart":false});
            var Q502;
            Q502=makeQuery(id+"F2.opExtrude","CAP_EDGE",EDGE,{"disambiguationData":[OSD([sQuery(id+"F0.wireOp",EDGE,"E30")])],"isStart":false});
            var Q503;
            Q503=makeQuery(id+"F2.opExtrude","CAP_EDGE",EDGE,{"disambiguationData":[OSD([sQuery(id+"F0.wireOp",EDGE,"E12")])],"isStart":false});
            var Q504;
            Q504=makeQuery(id+"F2.opExtrude","CAP_EDGE",EDGE,{"disambiguationData":[OSD([sQuery(id+"F0.wireOp",EDGE,"E4")])],"isStart":false});
            var Q505;
            Q505=makeQuery(id+"F2.opExtrude","CAP_EDGE",EDGE,{"disambiguationData":[OSD([sQuery(id+"F0.wireOp",EDGE,"E0.1")])],"isStart":false});
            var Q506;
            Q506=makeQuery(id+"F2.opExtrude","SWEPT_EDGE",EDGE,{"disambiguationData":[OSD([sQuery(id+"F0.wireOp",EDGE,"E2"),sQuery(id+"F0.wireOp",EDGE,"E62.trimOffspring")])]});
            var Q507;
            Q507=makeQuery(id+"F2.opExtrude","CAP_EDGE",EDGE,{"disambiguationData":[OSD([sQuery(id+"F0.wireOp",EDGE,"E58")])],"isStart":false});
            var Q508;
            Q508=makeQuery(id+"F2.opExtrude","CAP_EDGE",EDGE,{"disambiguationData":[OSD([sQuery(id+"F0.wireOp",EDGE,"E47.0")])],"isStart":false});
            var Q509;
            Q509=makeQuery(id+"F2.opExtrude","CAP_EDGE",EDGE,{"disambiguationData":[OSD([sQuery(id+"F0.wireOp",EDGE,"E33")])],"isStart":false});
            var Q510;
            Q510=makeQuery(id+"F2.opExtrude","CAP_EDGE",EDGE,{"disambiguationData":[OSD([sQuery(id+"F0.wireOp",EDGE,"E24.trimOffspring")])],"isStart":false});
            var Q511;
            Q511=makeQuery(id+"F2.opExtrude","CAP_EDGE",EDGE,{"disambiguationData":[OSD([sQuery(id+"F0.wireOp",EDGE,"E15")])],"isStart":false});
            var Q512;
            Q512=makeQuery(id+"F2.opExtrude","CAP_EDGE",EDGE,{"disambiguationData":[OSD([sQuery(id+"F0.wireOp",EDGE,"E8")])],"isStart":false});
            var Q513;
            Q513=makeQuery(id+"F2.opExtrude","CAP_EDGE",EDGE,{"disambiguationData":[OSD([sQuery(id+"F0.wireOp",EDGE,"E0.4")])],"isStart":false});
            var Q514;
            Q514=makeQuery(id+"F2.opExtrude","SWEPT_EDGE",EDGE,{"disambiguationData":[OSD([sQuery(id+"F0.wireOp",EDGE,"E10"),sQuery(id+"F0.wireOp",EDGE,"E14")])]});
            var Q515;
            Q515=makeQuery(id+"F2.opExtrude","SWEPT_EDGE",EDGE,{"disambiguationData":[OSD([sQuery(id+"F0.wireOp",EDGE,"E3"),sQuery(id+"F0.wireOp",EDGE,"E4")])]});
            var Q516;
            Q516=makeQuery(id+"F2.opExtrude","SWEPT_EDGE",EDGE,{"disambiguationData":[OSD([sQuery(id+"F0.wireOp",EDGE,"E3"),sQuery(id+"F0.wireOp",EDGE,"E6")])]});
            var Q517;
            Q517=makeQuery(id+"F2.opExtrude","SWEPT_EDGE",EDGE,{"disambiguationData":[OSD([sQuery(id+"F0.wireOp",EDGE,"E1"),sQuery(id+"F0.wireOp",EDGE,"E60")])]});
            var Q518;
            Q518=makeQuery(id+"F2.opExtrude","SWEPT_EDGE",EDGE,{"disambiguationData":[OSD([sQuery(id+"F0.wireOp",EDGE,"E0.5"),sQuery(id+"F0.wireOp",EDGE,"E2")])]});
            var Q519;
            Q519=makeQuery(id+"F2.opExtrude","SWEPT_EDGE",EDGE,{"disambiguationData":[OSD([sQuery(id+"F0.wireOp",EDGE,"E0.5"),sQuery(id+"F0.wireOp",EDGE,"E14")])]});
            var Q520;
            Q520=makeQuery(id+"F2.opExtrude","SWEPT_EDGE",EDGE,{"disambiguationData":[OSD([sQuery(id+"F0.wireOp",EDGE,"E0.4"),sQuery(id+"F0.wireOp",EDGE,"E13")])]});
            var Q521;
            Q521=makeQuery(id+"F2.opExtrude","SWEPT_EDGE",EDGE,{"disambiguationData":[OSD([sQuery(id+"F0.wireOp",EDGE,"E0.4"),sQuery(id+"F0.wireOp",EDGE,"E9")])]});
            var Q522;
            Q522=makeQuery(id+"F2.opExtrude","SWEPT_EDGE",EDGE,{"disambiguationData":[OSD([sQuery(id+"F0.wireOp",EDGE,"E0.3"),sQuery(id+"F0.wireOp",EDGE,"E9")])]});
            var Q523;
            Q523=makeQuery(id+"F2.opExtrude","SWEPT_EDGE",EDGE,{"disambiguationData":[OSD([sQuery(id+"F0.wireOp",EDGE,"E0.3"),sQuery(id+"F0.wireOp",EDGE,"E15")])]});
            var Q524;
            Q524=makeQuery(id+"F2.opExtrude","SWEPT_EDGE",EDGE,{"disambiguationData":[OSD([sQuery(id+"F0.wireOp",EDGE,"E0.2"),sQuery(id+"F0.wireOp",EDGE,"E16")])]});
            var Q525;
            Q525=makeQuery(id+"F2.opExtrude","SWEPT_EDGE",EDGE,{"disambiguationData":[OSD([sQuery(id+"F0.wireOp",EDGE,"E0.2"),sQuery(id+"F0.wireOp",EDGE,"E57.trimOffspring")])]});
            var Q526;
            Q526=makeQuery(id+"F2.opExtrude","CAP_FACE",FACE,{"disambiguationData":[OSD([sQuery(id+"F0.wireOp",EDGE,"E0.1"),sQuery(id+"F0.wireOp",EDGE,"E0.2"),sQuery(id+"F0.wireOp",EDGE,"E0.3"),sQuery(id+"F0.wireOp",EDGE,"E0.4"),sQuery(id+"F0.wireOp",EDGE,"E0.5"),sQuery(id+"F0.wireOp",EDGE,"E1"),sQuery(id+"F0.wireOp",EDGE,"E2"),sQuery(id+"F0.wireOp",EDGE,"E3"),sQuery(id+"F0.wireOp",EDGE,"E4"),sQuery(id+"F0.wireOp",EDGE,"E6"),sQuery(id+"F0.wireOp",EDGE,"E7"),sQuery(id+"F0.wireOp",EDGE,"E8"),sQuery(id+"F0.wireOp",EDGE,"E9"),sQuery(id+"F0.wireOp",EDGE,"E10"),sQuery(id+"F0.wireOp",EDGE,"E11"),sQuery(id+"F0.wireOp",EDGE,"E12"),sQuery(id+"F0.wireOp",EDGE,"E13"),sQuery(id+"F0.wireOp",EDGE,"E14"),sQuery(id+"F0.wireOp",EDGE,"E15"),sQuery(id+"F0.wireOp",EDGE,"E16"),sQuery(id+"F0.wireOp",EDGE,"E17"),sQuery(id+"F0.wireOp",EDGE,"E18"),sQuery(id+"F0.wireOp",EDGE,"E19"),sQuery(id+"F0.wireOp",EDGE,"E20"),sQuery(id+"F0.wireOp",EDGE,"E21"),sQuery(id+"F0.wireOp",EDGE,"E22"),sQuery(id+"F0.wireOp",EDGE,"E24.trimOffspring"),sQuery(id+"F0.wireOp",EDGE,"E26"),sQuery(id+"F0.wireOp",EDGE,"E27"),sQuery(id+"F0.wireOp",EDGE,"E28"),sQuery(id+"F0.wireOp",EDGE,"E29"),sQuery(id+"F0.wireOp",EDGE,"E30"),sQuery(id+"F0.wireOp",EDGE,"E31"),sQuery(id+"F0.wireOp",EDGE,"E32"),sQuery(id+"F0.wireOp",EDGE,"E33"),sQuery(id+"F0.wireOp",EDGE,"E34"),sQuery(id+"F0.wireOp",EDGE,"E35.0"),sQuery(id+"F0.wireOp",EDGE,"E36.0"),sQuery(id+"F0.wireOp",EDGE,"E37.0"),sQuery(id+"F0.wireOp",EDGE,"E38.0"),sQuery(id+"F0.wireOp",EDGE,"E39.0"),sQuery(id+"F0.wireOp",EDGE,"E40.0"),sQuery(id+"F0.wireOp",EDGE,"E41"),sQuery(id+"F0.wireOp",EDGE,"E42"),sQuery(id+"F0.wireOp",EDGE,"E43"),sQuery(id+"F0.wireOp",EDGE,"E44"),sQuery(id+"F0.wireOp",EDGE,"E45"),sQuery(id+"F0.wireOp",EDGE,"E46"),sQuery(id+"F0.wireOp",EDGE,"E47.0"),sQuery(id+"F0.wireOp",EDGE,"E48.0"),sQuery(id+"F0.wireOp",EDGE,"E49.0"),sQuery(id+"F0.wireOp",EDGE,"E50.0"),sQuery(id+"F0.wireOp",EDGE,"E51.0"),sQuery(id+"F0.wireOp",EDGE,"E52"),sQuery(id+"F0.wireOp",EDGE,"E53"),sQuery(id+"F0.wireOp",EDGE,"E54"),sQuery(id+"F0.wireOp",EDGE,"E55.trimOffspring"),sQuery(id+"F0.wireOp",EDGE,"E56"),sQuery(id+"F0.wireOp",EDGE,"E57.trimOffspring"),sQuery(id+"F0.wireOp",EDGE,"E58"),sQuery(id+"F0.wireOp",EDGE,"E59"),sQuery(id+"F0.wireOp",EDGE,"E60"),sQuery(id+"F0.wireOp",EDGE,"E61.trimOffspring"),sQuery(id+"F0.wireOp",EDGE,"E62.trimOffspring")])],"isStart":true});
            var Q527;
            Q527=makeQuery(id+"F2.opExtrude","SWEPT_EDGE",EDGE,{"disambiguationData":[OSD([sQuery(id+"F0.wireOp",EDGE,"E0.1"),sQuery(id+"F0.wireOp",EDGE,"E24.trimOffspring")])]});
            var Q528;
            Q528=makeQuery(id+"F2.opExtrude","SWEPT_EDGE",EDGE,{"disambiguationData":[OSD([sQuery(id+"F0.wireOp",EDGE,"E0.1"),sQuery(id+"F0.wireOp",EDGE,"E1")])]});
            var Q529;
            Q529=makeQuery(id+"F2.opExtrude","SWEPT_EDGE",EDGE,{"disambiguationData":[OSD([sQuery(id+"F0.wireOp",EDGE,"E7"),sQuery(id+"F0.wireOp",EDGE,"E17")])]});
            var Q530;
            Q530=makeQuery(id+"F2.opExtrude","SWEPT_EDGE",EDGE,{"disambiguationData":[OSD([sQuery(id+"F0.wireOp",EDGE,"E4"),sQuery(id+"F0.wireOp",EDGE,"E60")])]});
            var Q531;
            Q531=makeQuery(id+"F2.opExtrude","SWEPT_EDGE",EDGE,{"disambiguationData":[OSD([sQuery(id+"F0.wireOp",EDGE,"E8"),sQuery(id+"F0.wireOp",EDGE,"E16")])]});
            var Q532;
            Q532=makeQuery(id+"F2.opExtrude","CAP_EDGE",EDGE,{"disambiguationData":[OSD([sQuery(id+"F0.wireOp",EDGE,"E99.MirrorC")])],"isStart":false});
            var Q533;
            Q533=makeQuery(id+"F2.opExtrude","CAP_EDGE",EDGE,{"disambiguationData":[OSD([sQuery(id+"F0.wireOp",EDGE,"E119.MirrorCS")])],"isStart":false});
            var Q534;
            Q534=makeQuery(id+"F2.opExtrude","CAP_EDGE",EDGE,{"disambiguationData":[OSD([sQuery(id+"F0.wireOp",EDGE,"E92.MirrorCS")])],"isStart":false});
            var Q535;
            Q535=makeQuery(id+"F2.opExtrude","SWEPT_EDGE",EDGE,{"disambiguationData":[OSD([sQuery(id+"F0.wireOp",EDGE,"E119.MirrorCS"),sQuery(id+"F0.wireOp",EDGE,"E117.MirrorCS")])]});
            var Q536;
            Q536=makeQuery(id+"F2.opExtrude","CAP_EDGE",EDGE,{"disambiguationData":[OSD([sQuery(id+"F0.wireOp",EDGE,"E89.MirrorCS")])],"isStart":false});
            var Q537;
            Q537=makeQuery(id+"F2.opExtrude","SWEPT_EDGE",EDGE,{"disambiguationData":[OSD([sQuery(id+"F0.wireOp",EDGE,"E116.MirrorCS"),sQuery(id+"F0.wireOp",EDGE,"E118.MirrorCS")])]});
            var Q538;
            Q538=makeQuery(id+"F2.opExtrude","CAP_EDGE",EDGE,{"disambiguationData":[OSD([sQuery(id+"F0.wireOp",EDGE,"E102.MirrorCS")])],"isStart":true});
            var Q539;
            Q539=makeQuery(id+"F2.opExtrude","CAP_EDGE",EDGE,{"disambiguationData":[OSD([sQuery(id+"F0.wireOp",EDGE,"E75.MirrorCS")])],"isStart":false});
            var Q540;
            {var subQ0=sQuery(id+"F0.wireOp",EDGE,"E74.MirrorCS");Q540=makeQuery(id+"F2.opExtrude","CAP_EDGE",EDGE,{"disambiguationData":[OSD([subQ0]),TDD([makeQuery(id+"F0.imprint","IMPRINT",EDGE,{"disambiguationData":[TD([[makeQuery(id+"F0.imprint","INTERSECT",VERTEX,{"derivedFrom":[sQuery(id+"F0.wireOp",EDGE,"E76.MirrorCS"),subQ0]}),1.0]])],"derivedFrom":subQ0})])],"isStart":false});}
            var Q541;
            Q541=makeQuery(id+"F2.opExtrude","CAP_EDGE",EDGE,{"disambiguationData":[OSD([sQuery(id+"F0.wireOp",EDGE,"E122.MirrorCS")])],"isStart":false});
            var Q542;
            Q542=makeQuery(id+"F2.opExtrude","SWEPT_EDGE",EDGE,{"disambiguationData":[OSD([sQuery(id+"F0.wireOp",EDGE,"E122.MirrorCS"),sQuery(id+"F0.wireOp",EDGE,"E112.MirrorCS")])]});
            var Q543;
            Q543=makeQuery(id+"F2.opExtrude","CAP_EDGE",EDGE,{"disambiguationData":[OSD([sQuery(id+"F0.wireOp",EDGE,"E113.MirrorCS")])],"isStart":false});
            var Q544;
            Q544=makeQuery(id+"F2.opExtrude","CAP_EDGE",EDGE,{"disambiguationData":[OSD([sQuery(id+"F0.wireOp",EDGE,"E124.MirrorCS")])],"isStart":false});
            var Q545;
            {var subQ0=sQuery(id+"F0.wireOp",EDGE,"E74.MirrorCS");Q545=makeQuery(id+"F2.opExtrude","CAP_EDGE",EDGE,{"disambiguationData":[OSD([subQ0]),TDD([makeQuery(id+"F0.imprint","IMPRINT",EDGE,{"disambiguationData":[TD([[makeQuery(id+"F0.imprint","INTERSECT",VERTEX,{"derivedFrom":[sQuery(id+"F0.wireOp",EDGE,"E75.MirrorCS"),subQ0]}),-1.0]])],"derivedFrom":subQ0})])],"isStart":false});}
            var Q546;
            Q546=makeQuery(id+"F2.opExtrude","CAP_EDGE",EDGE,{"disambiguationData":[OSD([sQuery(id+"F0.wireOp",EDGE,"E91.MirrorC")])],"isStart":false});
            var Q547;
            Q547=makeQuery(id+"F2.opExtrude","CAP_EDGE",EDGE,{"disambiguationData":[OSD([sQuery(id+"F0.wireOp",EDGE,"E86.MirrorC")])],"isStart":false});
            var Q548;
            Q548=makeQuery(id+"F2.opExtrude","CAP_EDGE",EDGE,{"disambiguationData":[OSD([sQuery(id+"F0.wireOp",EDGE,"E101.MirrorCS")])],"isStart":true});
            var Q549;
            Q549=makeQuery(id+"F2.opExtrude","SWEPT_EDGE",EDGE,{"disambiguationData":[OSD([sQuery(id+"F0.wireOp",EDGE,"E75.MirrorCS"),sQuery(id+"F0.wireOp",EDGE,"E112.MirrorCS")])]});
            var Q550;
            Q550=makeQuery(id+"F2.opExtrude","CAP_EDGE",EDGE,{"disambiguationData":[OSD([sQuery(id+"F0.wireOp",EDGE,"E84.MirrorCS"),sQuery(id+"F0.wireOp",EDGE,"E98.MirrorCS")])],"isStart":false});
            var Q551;
            Q551=makeQuery(id+"F2.opExtrude","CAP_EDGE",EDGE,{"disambiguationData":[OSD([sQuery(id+"F0.wireOp",EDGE,"E125.MirrorC")])],"isStart":false});
            var Q552;
            Q552=makeQuery(id+"F2.opExtrude","CAP_EDGE",EDGE,{"disambiguationData":[OSD([sQuery(id+"F0.wireOp",EDGE,"E107.MirrorC")])],"isStart":false});
            var Q553;
            Q553=makeQuery(id+"F2.opExtrude","CAP_EDGE",EDGE,{"disambiguationData":[OSD([sQuery(id+"F0.wireOp",EDGE,"E118.MirrorCS")])],"isStart":false});
            var Q554;
            Q554=makeQuery(id+"F2.opExtrude","CAP_EDGE",EDGE,{"disambiguationData":[OSD([sQuery(id+"F0.wireOp",EDGE,"E115.MirrorCS")])],"isStart":false});
            var Q555;
            Q555=makeQuery(id+"F2.opExtrude","CAP_EDGE",EDGE,{"disambiguationData":[OSD([sQuery(id+"F0.wireOp",EDGE,"E97.MirrorCS")])],"isStart":false});
            var Q556;
            Q556=makeQuery(id+"F2.opExtrude","SWEPT_EDGE",EDGE,{"disambiguationData":[OSD([sQuery(id+"F0.wireOp",EDGE,"E76.MirrorCS"),sQuery(id+"F0.wireOp",EDGE,"E120.MirrorCS")])]});
            var Q557;
            Q557=makeQuery(id+"F2.opExtrude","CAP_EDGE",EDGE,{"disambiguationData":[OSD([sQuery(id+"F0.wireOp",EDGE,"E78.MirrorC")])],"isStart":false});
            var Q558;
            Q558=makeQuery(id+"F2.opExtrude","CAP_FACE",FACE,{"disambiguationData":[OSD([sQuery(id+"F0.wireOp",EDGE,"E73.MirrorCS"),sQuery(id+"F0.wireOp",EDGE,"E68.MirrorCS"),sQuery(id+"F0.wireOp",EDGE,"E69.MirrorCS"),sQuery(id+"F0.wireOp",EDGE,"E89.MirrorCS"),sQuery(id+"F0.wireOp",EDGE,"E77.MirrorCS"),sQuery(id+"F0.wireOp",EDGE,"E67.MirrorCS"),sQuery(id+"F0.wireOp",EDGE,"E84.MirrorCS"),sQuery(id+"F0.wireOp",EDGE,"E85.MirrorCS"),sQuery(id+"F0.wireOp",EDGE,"E72.MirrorCS"),sQuery(id+"F0.wireOp",EDGE,"E91.MirrorC"),sQuery(id+"F0.wireOp",EDGE,"E75.MirrorCS"),sQuery(id+"F0.wireOp",EDGE,"E82.MirrorCS"),sQuery(id+"F0.wireOp",EDGE,"E87.MirrorCS"),sQuery(id+"F0.wireOp",EDGE,"E79.MirrorCS"),sQuery(id+"F0.wireOp",EDGE,"E78.MirrorC"),sQuery(id+"F0.wireOp",EDGE,"E70.MirrorCS"),sQuery(id+"F0.wireOp",EDGE,"E66.MirrorCS"),sQuery(id+"F0.wireOp",EDGE,"E80.MirrorCS"),sQuery(id+"F0.wireOp",EDGE,"E88.MirrorCS"),sQuery(id+"F0.wireOp",EDGE,"E86.MirrorC"),sQuery(id+"F0.wireOp",EDGE,"E65.MirrorCS"),sQuery(id+"F0.wireOp",EDGE,"E71.MirrorCS"),sQuery(id+"F0.wireOp",EDGE,"E83.MirrorCS"),sQuery(id+"F0.wireOp",EDGE,"E90.MirrorCS"),sQuery(id+"F0.wireOp",EDGE,"E76.MirrorCS"),sQuery(id+"F0.wireOp",EDGE,"E92.MirrorCS"),sQuery(id+"F0.wireOp",EDGE,"E63.MirrorC"),sQuery(id+"F0.wireOp",EDGE,"E64.MirrorCS"),sQuery(id+"F0.wireOp",EDGE,"E74.MirrorCS"),sQuery(id+"F0.wireOp",EDGE,"E96.MirrorCS"),sQuery(id+"F0.wireOp",EDGE,"E95.MirrorCS"),sQuery(id+"F0.wireOp",EDGE,"E93.MirrorCS"),sQuery(id+"F0.wireOp",EDGE,"E98.MirrorCS"),sQuery(id+"F0.wireOp",EDGE,"E94.MirrorCS"),sQuery(id+"F0.wireOp",EDGE,"E100.MirrorCS"),sQuery(id+"F0.wireOp",EDGE,"E97.MirrorCS"),sQuery(id+"F0.wireOp",EDGE,"E103.MirrorCS"),sQuery(id+"F0.wireOp",EDGE,"E113.MirrorCS"),sQuery(id+"F0.wireOp",EDGE,"E99.MirrorC"),sQuery(id+"F0.wireOp",EDGE,"E102.MirrorCS"),sQuery(id+"F0.wireOp",EDGE,"E106.MirrorCS"),sQuery(id+"F0.wireOp",EDGE,"E126.MirrorC"),sQuery(id+"F0.wireOp",EDGE,"E125.MirrorC"),sQuery(id+"F0.wireOp",EDGE,"E116.MirrorCS"),sQuery(id+"F0.wireOp",EDGE,"E115.MirrorCS"),sQuery(id+"F0.wireOp",EDGE,"E110.MirrorCS"),sQuery(id+"F0.wireOp",EDGE,"E101.MirrorCS"),sQuery(id+"F0.wireOp",EDGE,"E111.MirrorCS"),sQuery(id+"F0.wireOp",EDGE,"E119.MirrorCS"),sQuery(id+"F0.wireOp",EDGE,"E114.MirrorCS"),sQuery(id+"F0.wireOp",EDGE,"E104.MirrorCS"),sQuery(id+"F0.wireOp",EDGE,"E109.MirrorCS"),sQuery(id+"F0.wireOp",EDGE,"E105.MirrorCS"),sQuery(id+"F0.wireOp",EDGE,"E81.MirrorCS"),sQuery(id+"F0.wireOp",EDGE,"E120.MirrorCS"),sQuery(id+"F0.wireOp",EDGE,"E123.MirrorC"),sQuery(id+"F0.wireOp",EDGE,"E124.MirrorCS"),sQuery(id+"F0.wireOp",EDGE,"E122.MirrorCS"),sQuery(id+"F0.wireOp",EDGE,"E121.MirrorCS"),sQuery(id+"F0.wireOp",EDGE,"E108.MirrorCS"),sQuery(id+"F0.wireOp",EDGE,"E107.MirrorC"),sQuery(id+"F0.wireOp",EDGE,"E112.MirrorCS"),sQuery(id+"F0.wireOp",EDGE,"E118.MirrorCS"),sQuery(id+"F0.wireOp",EDGE,"E117.MirrorCS")])],"isStart":true});
            var Q559;
            Q559=makeQuery(id+"F2.opExtrude","CAP_EDGE",EDGE,{"disambiguationData":[OSD([sQuery(id+"F0.wireOp",EDGE,"E88.MirrorCS")])],"isStart":false});
            var Q560;
            Q560=makeQuery(id+"F2.opExtrude","CAP_EDGE",EDGE,{"disambiguationData":[OSD([sQuery(id+"F0.wireOp",EDGE,"E94.MirrorCS")])],"isStart":false});
            var Q561;
            Q561=makeQuery(id+"F2.opExtrude","CAP_EDGE",EDGE,{"disambiguationData":[OSD([sQuery(id+"F0.wireOp",EDGE,"E123.MirrorC")])],"isStart":false});
            var Q562;
            Q562=makeQuery(id+"F2.opExtrude","CAP_EDGE",EDGE,{"disambiguationData":[OSD([sQuery(id+"F0.wireOp",EDGE,"E85.MirrorCS")])],"isStart":false});
            var Q563;
            Q563=makeQuery(id+"F2.opExtrude","CAP_EDGE",EDGE,{"disambiguationData":[OSD([sQuery(id+"F0.wireOp",EDGE,"E80.MirrorCS"),sQuery(id+"F0.wireOp",EDGE,"E64.MirrorCS")])],"isStart":false});
            var Q564;
            Q564=makeQuery(id+"F2.opExtrude","CAP_EDGE",EDGE,{"disambiguationData":[OSD([sQuery(id+"F0.wireOp",EDGE,"E117.MirrorCS")])],"isStart":false});
            var Q565;
            Q565=makeQuery(id+"F2.opExtrude","SWEPT_EDGE",EDGE,{"disambiguationData":[OSD([sQuery(id+"F0.wireOp",EDGE,"E96.MirrorCS"),sQuery(id+"F0.wireOp",EDGE,"E109.MirrorCS")])]});
            var Q566;
            Q566=makeQuery(id+"F2.opExtrude","CAP_EDGE",EDGE,{"disambiguationData":[OSD([sQuery(id+"F0.wireOp",EDGE,"E120.MirrorCS")])],"isStart":false});
            var Q567;
            Q567=makeQuery(id+"F2.opExtrude","CAP_EDGE",EDGE,{"disambiguationData":[OSD([sQuery(id+"F0.wireOp",EDGE,"E73.MirrorCS"),sQuery(id+"F0.wireOp",EDGE,"E96.MirrorCS")])],"isStart":false});
            var Q568;
            Q568=makeQuery(id+"F2.opExtrude","CAP_EDGE",EDGE,{"disambiguationData":[OSD([sQuery(id+"F0.wireOp",EDGE,"E110.MirrorCS")])],"isStart":true});
            var Q569;
            Q569=makeQuery(id+"F2.opExtrude","CAP_EDGE",EDGE,{"disambiguationData":[OSD([sQuery(id+"F0.wireOp",EDGE,"E103.MirrorCS")])],"isStart":false});
            var Q570;
            Q570=makeQuery(id+"F2.opExtrude","SWEPT_EDGE",EDGE,{"disambiguationData":[OSD([sQuery(id+"F0.wireOp",EDGE,"E75.MirrorCS"),sQuery(id+"F0.wireOp",EDGE,"E74.MirrorCS")])]});
            var Q571;
            Q571=makeQuery(id+"F2.opExtrude","CAP_EDGE",EDGE,{"disambiguationData":[OSD([sQuery(id+"F0.wireOp",EDGE,"E63.MirrorC")])],"isStart":false});
            var Q572;
            Q572=makeQuery(id+"F2.opExtrude","CAP_EDGE",EDGE,{"disambiguationData":[OSD([sQuery(id+"F0.wireOp",EDGE,"E109.MirrorCS")])],"isStart":true});
            var Q573;
            Q573=makeQuery(id+"F2.opExtrude","CAP_EDGE",EDGE,{"disambiguationData":[OSD([sQuery(id+"F0.wireOp",EDGE,"E90.MirrorCS")])],"isStart":true});
            var Q574;
            Q574=makeQuery(id+"F2.opExtrude","SWEPT_EDGE",EDGE,{"disambiguationData":[OSD([sQuery(id+"F0.wireOp",EDGE,"E113.MirrorCS"),sQuery(id+"F0.wireOp",EDGE,"E102.MirrorCS")])]});
            var Q575;
            Q575=makeQuery(id+"F2.opExtrude","SWEPT_EDGE",EDGE,{"disambiguationData":[OSD([sQuery(id+"F0.wireOp",EDGE,"E90.MirrorCS"),sQuery(id+"F0.wireOp",EDGE,"E119.MirrorCS")])]});
            var Q576;
            Q576=makeQuery(id+"F2.opExtrude","SWEPT_EDGE",EDGE,{"disambiguationData":[OSD([sQuery(id+"F0.wireOp",EDGE,"E69.MirrorCS"),sQuery(id+"F0.wireOp",EDGE,"E89.MirrorCS")])]});
            var Q577;
            Q577=makeQuery(id+"F2.opExtrude","CAP_EDGE",EDGE,{"disambiguationData":[OSD([sQuery(id+"F0.wireOp",EDGE,"E108.MirrorCS")])],"isStart":false});
            var Q578;
            Q578=makeQuery(id+"F2.opExtrude","CAP_EDGE",EDGE,{"disambiguationData":[OSD([sQuery(id+"F0.wireOp",EDGE,"E104.MirrorCS")])],"isStart":false});
            var Q579;
            Q579=makeQuery(id+"F2.opExtrude","CAP_EDGE",EDGE,{"disambiguationData":[OSD([sQuery(id+"F0.wireOp",EDGE,"E126.MirrorC")])],"isStart":false});
            var Q580;
            Q580=makeQuery(id+"F2.opExtrude","CAP_EDGE",EDGE,{"disambiguationData":[OSD([sQuery(id+"F0.wireOp",EDGE,"E93.MirrorCS")])],"isStart":false});
            var Q581;
            Q581=makeQuery(id+"F2.opExtrude","CAP_EDGE",EDGE,{"disambiguationData":[OSD([sQuery(id+"F0.wireOp",EDGE,"E83.MirrorCS")])],"isStart":false});
            var Q582;
            Q582=makeQuery(id+"F2.opExtrude","CAP_EDGE",EDGE,{"disambiguationData":[OSD([sQuery(id+"F0.wireOp",EDGE,"E87.MirrorCS")])],"isStart":false});
            var Q583;
            Q583=makeQuery(id+"F2.opExtrude","SWEPT_EDGE",EDGE,{"disambiguationData":[OSD([sQuery(id+"F0.wireOp",EDGE,"E103.MirrorCS"),sQuery(id+"F0.wireOp",EDGE,"E105.MirrorCS")])]});
            var Q584;
            Q584=makeQuery(id+"F2.opExtrude","SWEPT_EDGE",EDGE,{"disambiguationData":[OSD([sQuery(id+"F0.wireOp",EDGE,"E83.MirrorCS"),sQuery(id+"F0.wireOp",EDGE,"E103.MirrorCS")])]});
            var Q585;
            Q585=makeQuery(id+"F2.opExtrude","CAP_EDGE",EDGE,{"disambiguationData":[OSD([sQuery(id+"F0.wireOp",EDGE,"E69.MirrorCS"),sQuery(id+"F0.wireOp",EDGE,"E79.MirrorCS"),sQuery(id+"F0.wireOp",EDGE,"E66.MirrorCS")])],"isStart":true});
            var Q586;
            Q586=makeQuery(id+"F2.opExtrude","SWEPT_EDGE",EDGE,{"disambiguationData":[OSD([sQuery(id+"F0.wireOp",EDGE,"E97.MirrorCS"),sQuery(id+"F0.wireOp",EDGE,"E102.MirrorCS")])]});
            var Q587;
            Q587=makeQuery(id+"F2.opExtrude","SWEPT_EDGE",EDGE,{"disambiguationData":[OSD([sQuery(id+"F0.wireOp",EDGE,"E83.MirrorCS"),sQuery(id+"F0.wireOp",EDGE,"E94.MirrorCS")])]});
            var Q588;
            Q588=makeQuery(id+"F2.opExtrude","SWEPT_EDGE",EDGE,{"disambiguationData":[OSD([sQuery(id+"F0.wireOp",EDGE,"E73.MirrorCS"),sQuery(id+"F0.wireOp",EDGE,"E85.MirrorCS")])]});
            var Q589;
            Q589=makeQuery(id+"F2.opExtrude","CAP_EDGE",EDGE,{"disambiguationData":[OSD([sQuery(id+"F0.wireOp",EDGE,"E121.MirrorCS")])],"isStart":false});
            var Q590;
            Q590=makeQuery(id+"F2.opExtrude","CAP_EDGE",EDGE,{"disambiguationData":[OSD([sQuery(id+"F0.wireOp",EDGE,"E114.MirrorCS")])],"isStart":false});
            var Q591;
            Q591=makeQuery(id+"F2.opExtrude","CAP_EDGE",EDGE,{"disambiguationData":[OSD([sQuery(id+"F0.wireOp",EDGE,"E95.MirrorCS")])],"isStart":false});
            var Q592;
            Q592=makeQuery(id+"F2.opExtrude","CAP_EDGE",EDGE,{"disambiguationData":[OSD([sQuery(id+"F0.wireOp",EDGE,"E71.MirrorCS"),sQuery(id+"F0.wireOp",EDGE,"E111.MirrorCS")])],"isStart":false});
            var Q593;
            Q593=makeQuery(id+"F2.opExtrude","CAP_EDGE",EDGE,{"disambiguationData":[OSD([sQuery(id+"F0.wireOp",EDGE,"E82.MirrorCS")])],"isStart":false});
            var Q594;
            Q594=makeQuery(id+"F2.opExtrude","CAP_EDGE",EDGE,{"disambiguationData":[OSD([sQuery(id+"F0.wireOp",EDGE,"E68.MirrorCS"),sQuery(id+"F0.wireOp",EDGE,"E77.MirrorCS"),sQuery(id+"F0.wireOp",EDGE,"E72.MirrorCS")])],"isStart":false});
            var Q595;
            Q595=makeQuery(id+"F2.opExtrude","SWEPT_EDGE",EDGE,{"disambiguationData":[OSD([sQuery(id+"F0.wireOp",EDGE,"E97.MirrorCS"),sQuery(id+"F0.wireOp",EDGE,"E104.MirrorCS")])]});
            var Q596;
            Q596=makeQuery(id+"F2.opExtrude","SWEPT_EDGE",EDGE,{"disambiguationData":[OSD([sQuery(id+"F0.wireOp",EDGE,"E88.MirrorCS"),sQuery(id+"F0.wireOp",EDGE,"E64.MirrorCS")])]});
            var Q597;
            Q597=makeQuery(id+"F2.opExtrude","CAP_EDGE",EDGE,{"disambiguationData":[OSD([sQuery(id+"F0.wireOp",EDGE,"E116.MirrorCS")])],"isStart":false});
            var Q598;
            Q598=makeQuery(id+"F2.opExtrude","CAP_EDGE",EDGE,{"disambiguationData":[OSD([sQuery(id+"F0.wireOp",EDGE,"E100.MirrorCS")])],"isStart":false});
            var Q599;
            Q599=makeQuery(id+"F2.opExtrude","CAP_EDGE",EDGE,{"disambiguationData":[OSD([sQuery(id+"F0.wireOp",EDGE,"E76.MirrorCS")])],"isStart":false});
            var Q600;
            Q600=makeQuery(id+"F2.opExtrude","CAP_EDGE",EDGE,{"disambiguationData":[OSD([sQuery(id+"F0.wireOp",EDGE,"E70.MirrorCS"),sQuery(id+"F0.wireOp",EDGE,"E106.MirrorCS")])],"isStart":false});
            var Q601;
            Q601=makeQuery(id+"F2.opExtrude","CAP_EDGE",EDGE,{"disambiguationData":[OSD([sQuery(id+"F0.wireOp",EDGE,"E67.MirrorCS"),sQuery(id+"F0.wireOp",EDGE,"E81.MirrorCS")])],"isStart":false});
            var Q602;
            Q602=makeQuery(id+"F2.opExtrude","SWEPT_EDGE",EDGE,{"disambiguationData":[OSD([sQuery(id+"F0.wireOp",EDGE,"E110.MirrorCS"),sQuery(id+"F0.wireOp",EDGE,"E101.MirrorCS")])]});
            var Q603;
            Q603=makeQuery(id+"F2.opExtrude","SWEPT_EDGE",EDGE,{"disambiguationData":[OSD([sQuery(id+"F0.wireOp",EDGE,"E92.MirrorCS"),sQuery(id+"F0.wireOp",EDGE,"E113.MirrorCS")])]});
            var Q604;
            Q604=makeQuery(id+"F2.opExtrude","CAP_EDGE",EDGE,{"disambiguationData":[OSD([sQuery(id+"F0.wireOp",EDGE,"E112.MirrorCS")])],"isStart":true});
            var Q605;
            Q605=makeQuery(id+"F2.opExtrude","CAP_EDGE",EDGE,{"disambiguationData":[OSD([sQuery(id+"F0.wireOp",EDGE,"E105.MirrorCS")])],"isStart":true});
            var Q606;
            Q606=makeQuery(id+"F2.opExtrude","SWEPT_EDGE",EDGE,{"disambiguationData":[OSD([sQuery(id+"F0.wireOp",EDGE,"E115.MirrorCS"),sQuery(id+"F0.wireOp",EDGE,"E118.MirrorCS")])]});
            var Q607;
            Q607=makeQuery(id+"F2.opExtrude","SWEPT_EDGE",EDGE,{"disambiguationData":[OSD([sQuery(id+"F0.wireOp",EDGE,"E76.MirrorCS"),sQuery(id+"F0.wireOp",EDGE,"E74.MirrorCS")])]});
            var Q608;
            Q608=makeQuery(id+"F2.opExtrude","SWEPT_EDGE",EDGE,{"disambiguationData":[OSD([sQuery(id+"F0.wireOp",EDGE,"E84.MirrorCS"),sQuery(id+"F0.wireOp",EDGE,"E85.MirrorCS")])]});
            var Q609;
            Q609=makeQuery(id+"F1.opExtrude","CAP_EDGE",EDGE,{"disambiguationData":[OSD([sQuery(id+"F0.wireOp",EDGE,"E87.MirrorCS")])],"isStart":true});
            var Q610;
            Q610=makeQuery(id+"F1.opExtrude","CAP_EDGE",EDGE,{"disambiguationData":[OSD([sQuery(id+"F0.wireOp",EDGE,"E83.MirrorCS")])],"isStart":true});
            var Q611;
            Q611=makeQuery(id+"F1.opExtrude","CAP_EDGE",EDGE,{"disambiguationData":[OSD([sQuery(id+"F0.wireOp",EDGE,"E126.MirrorC")])],"isStart":true});
            var Q612;
            Q612=makeQuery(id+"F1.opExtrude","CAP_EDGE",EDGE,{"disambiguationData":[OSD([sQuery(id+"F0.wireOp",EDGE,"E104.MirrorCS")])],"isStart":true});
            var Q613;
            Q613=makeQuery(id+"F1.opExtrude","CAP_EDGE",EDGE,{"disambiguationData":[OSD([sQuery(id+"F0.wireOp",EDGE,"E78.MirrorC")])],"isStart":true});
            var Q614;
            Q614=makeQuery(id+"F1.opExtrude","CAP_EDGE",EDGE,{"disambiguationData":[OSD([sQuery(id+"F0.wireOp",EDGE,"E108.MirrorCS")])],"isStart":true});
            var Q615;
            Q615=makeQuery(id+"F1.opExtrude","CAP_EDGE",EDGE,{"disambiguationData":[OSD([sQuery(id+"F0.wireOp",EDGE,"E107.MirrorC")])],"isStart":true});
            var Q616;
            Q616=makeQuery(id+"F1.opExtrude","CAP_EDGE",EDGE,{"disambiguationData":[OSD([sQuery(id+"F0.wireOp",EDGE,"E70.MirrorCS"),sQuery(id+"F0.wireOp",EDGE,"E106.MirrorCS")])],"isStart":true});
            var Q617;
            Q617=makeQuery(id+"F1.opExtrude","CAP_EDGE",EDGE,{"disambiguationData":[OSD([sQuery(id+"F0.wireOp",EDGE,"E116.MirrorCS")])],"isStart":true});
            var Q618;
            Q618=makeQuery(id+"F1.opExtrude","CAP_EDGE",EDGE,{"disambiguationData":[OSD([sQuery(id+"F0.wireOp",EDGE,"E84.MirrorCS"),sQuery(id+"F0.wireOp",EDGE,"E98.MirrorCS")])],"isStart":true});
            var Q619;
            Q619=makeQuery(id+"F1.opExtrude","CAP_EDGE",EDGE,{"disambiguationData":[OSD([sQuery(id+"F0.wireOp",EDGE,"E115.MirrorCS")])],"isStart":true});
            var Q620;
            Q620=makeQuery(id+"F1.opExtrude","CAP_EDGE",EDGE,{"disambiguationData":[OSD([sQuery(id+"F0.wireOp",EDGE,"E97.MirrorCS")])],"isStart":true});
            var Q621;
            Q621=makeQuery(id+"F1.opExtrude","CAP_EDGE",EDGE,{"disambiguationData":[OSD([sQuery(id+"F0.wireOp",EDGE,"E92.MirrorCS")])],"isStart":true});
            var Q622;
            Q622=makeQuery(id+"F1.opExtrude","CAP_EDGE",EDGE,{"disambiguationData":[OSD([sQuery(id+"F0.wireOp",EDGE,"E80.MirrorCS"),sQuery(id+"F0.wireOp",EDGE,"E64.MirrorCS")])],"isStart":true});
            var Q623;
            Q623=makeQuery(id+"F1.opExtrude","CAP_EDGE",EDGE,{"disambiguationData":[OSD([sQuery(id+"F0.wireOp",EDGE,"E118.MirrorCS")])],"isStart":true});
            var Q624;
            Q624=makeQuery(id+"F1.opExtrude","CAP_EDGE",EDGE,{"disambiguationData":[OSD([sQuery(id+"F0.wireOp",EDGE,"E120.MirrorCS")])],"isStart":true});
            var Q625;
            Q625=makeQuery(id+"F1.opExtrude","CAP_EDGE",EDGE,{"disambiguationData":[OSD([sQuery(id+"F0.wireOp",EDGE,"E117.MirrorCS")])],"isStart":true});
            var Q626;
            Q626=makeQuery(id+"F1.opExtrude","CAP_EDGE",EDGE,{"disambiguationData":[OSD([sQuery(id+"F0.wireOp",EDGE,"E113.MirrorCS")])],"isStart":true});
            var Q627;
            Q627=makeQuery(id+"F1.opExtrude","CAP_EDGE",EDGE,{"disambiguationData":[OSD([sQuery(id+"F0.wireOp",EDGE,"E85.MirrorCS")])],"isStart":true});
            var Q628;
            Q628=makeQuery(id+"F1.opExtrude","CAP_EDGE",EDGE,{"disambiguationData":[OSD([sQuery(id+"F0.wireOp",EDGE,"E88.MirrorCS")])],"isStart":true});
            var Q629;
            Q629=makeQuery(id+"F1.opExtrude","CAP_EDGE",EDGE,{"disambiguationData":[OSD([sQuery(id+"F0.wireOp",EDGE,"E86.MirrorC")])],"isStart":true});
            var Q630;
            Q630=makeQuery(id+"F1.opExtrude","CAP_EDGE",EDGE,{"disambiguationData":[OSD([sQuery(id+"F0.wireOp",EDGE,"E75.MirrorCS")])],"isStart":true});
            var Q631;
            Q631=makeQuery(id+"F1.opExtrude","CAP_EDGE",EDGE,{"disambiguationData":[OSD([sQuery(id+"F0.wireOp",EDGE,"E99.MirrorC")])],"isStart":true});
            var Q632;
            Q632=makeQuery(id+"F1.opExtrude","CAP_EDGE",EDGE,{"disambiguationData":[OSD([sQuery(id+"F0.wireOp",EDGE,"E119.MirrorCS")])],"isStart":true});
            var Q633;
            Q633=makeQuery(id+"F1.opExtrude","CAP_EDGE",EDGE,{"disambiguationData":[OSD([sQuery(id+"F0.wireOp",EDGE,"E73.MirrorCS"),sQuery(id+"F0.wireOp",EDGE,"E96.MirrorCS")])],"isStart":true});
            var Q634;
            {var subQ0=sQuery(id+"F0.wireOp",EDGE,"E74.MirrorCS");Q634=makeQuery(id+"F1.opExtrude","CAP_EDGE",EDGE,{"disambiguationData":[OSD([subQ0]),TDD([makeQuery(id+"F0.imprint","IMPRINT",EDGE,{"disambiguationData":[TD([[makeQuery(id+"F0.imprint","INTERSECT",VERTEX,{"derivedFrom":[sQuery(id+"F0.wireOp",EDGE,"E76.MirrorCS"),subQ0]}),1.0]])],"derivedFrom":subQ0})])],"isStart":true});}
            var Q635;
            Q635=makeQuery(id+"F1.opExtrude","CAP_EDGE",EDGE,{"disambiguationData":[OSD([sQuery(id+"F0.wireOp",EDGE,"E91.MirrorC")])],"isStart":true});
            var Q636;
            {var subQ0=sQuery(id+"F0.wireOp",EDGE,"E74.MirrorCS");Q636=makeQuery(id+"F1.opExtrude","CAP_EDGE",EDGE,{"disambiguationData":[OSD([subQ0]),TDD([makeQuery(id+"F0.imprint","IMPRINT",EDGE,{"disambiguationData":[TD([[makeQuery(id+"F0.imprint","INTERSECT",VERTEX,{"derivedFrom":[sQuery(id+"F0.wireOp",EDGE,"E75.MirrorCS"),subQ0]}),-1.0]])],"derivedFrom":subQ0})])],"isStart":true});}
            var Q637;
            Q637=makeQuery(id+"F1.opExtrude","CAP_EDGE",EDGE,{"disambiguationData":[OSD([sQuery(id+"F0.wireOp",EDGE,"E124.MirrorCS")])],"isStart":true});
            var Q638;
            Q638=makeQuery(id+"F1.opExtrude","CAP_EDGE",EDGE,{"disambiguationData":[OSD([sQuery(id+"F0.wireOp",EDGE,"E121.MirrorCS")])],"isStart":true});
            var Q639;
            Q639=makeQuery(id+"F1.opExtrude","CAP_EDGE",EDGE,{"disambiguationData":[OSD([sQuery(id+"F0.wireOp",EDGE,"E68.MirrorCS"),sQuery(id+"F0.wireOp",EDGE,"E77.MirrorCS"),sQuery(id+"F0.wireOp",EDGE,"E72.MirrorCS")])],"isStart":true});
            var Q640;
            Q640=makeQuery(id+"F1.opExtrude","CAP_EDGE",EDGE,{"disambiguationData":[OSD([sQuery(id+"F0.wireOp",EDGE,"E95.MirrorCS")])],"isStart":true});
            var Q641;
            Q641=makeQuery(id+"F1.opExtrude","CAP_EDGE",EDGE,{"disambiguationData":[OSD([sQuery(id+"F0.wireOp",EDGE,"E114.MirrorCS")])],"isStart":true});
            var Q642;
            Q642=makeQuery(id+"F1.opExtrude","CAP_EDGE",EDGE,{"disambiguationData":[OSD([sQuery(id+"F0.wireOp",EDGE,"E71.MirrorCS"),sQuery(id+"F0.wireOp",EDGE,"E111.MirrorCS")])],"isStart":true});
            var Q643;
            Q643=makeQuery(id+"F1.opExtrude","CAP_EDGE",EDGE,{"disambiguationData":[OSD([sQuery(id+"F0.wireOp",EDGE,"E122.MirrorCS")])],"isStart":true});
            var Q644;
            Q644=makeQuery(id+"F1.opExtrude","CAP_EDGE",EDGE,{"disambiguationData":[OSD([sQuery(id+"F0.wireOp",EDGE,"E82.MirrorCS")])],"isStart":true});
            var Q645;
            Q645=makeQuery(id+"F1.opExtrude","CAP_EDGE",EDGE,{"disambiguationData":[OSD([sQuery(id+"F0.wireOp",EDGE,"E63.MirrorC")])],"isStart":true});
            var Q646;
            Q646=makeQuery(id+"F1.opExtrude","CAP_EDGE",EDGE,{"disambiguationData":[OSD([sQuery(id+"F0.wireOp",EDGE,"E103.MirrorCS")])],"isStart":true});
            var Q647;
            Q647=makeQuery(id+"F1.opExtrude","CAP_EDGE",EDGE,{"disambiguationData":[OSD([sQuery(id+"F0.wireOp",EDGE,"E123.MirrorC")])],"isStart":true});
            var Q648;
            Q648=makeQuery(id+"F1.opExtrude","CAP_EDGE",EDGE,{"disambiguationData":[OSD([sQuery(id+"F0.wireOp",EDGE,"E67.MirrorCS"),sQuery(id+"F0.wireOp",EDGE,"E81.MirrorCS")])],"isStart":true});
            var Q649;
            Q649=makeQuery(id+"F1.opExtrude","CAP_EDGE",EDGE,{"disambiguationData":[OSD([sQuery(id+"F0.wireOp",EDGE,"E76.MirrorCS")])],"isStart":true});
            var Q650;
            Q650=makeQuery(id+"F1.opExtrude","CAP_EDGE",EDGE,{"disambiguationData":[OSD([sQuery(id+"F0.wireOp",EDGE,"E100.MirrorCS")])],"isStart":true});
            var Q651;
            Q651=makeQuery(id+"F1.opExtrude","CAP_EDGE",EDGE,{"disambiguationData":[OSD([sQuery(id+"F0.wireOp",EDGE,"E89.MirrorCS")])],"isStart":true});
            var Q652;
            Q652=makeQuery(id+"F1.opExtrude","CAP_EDGE",EDGE,{"disambiguationData":[OSD([sQuery(id+"F0.wireOp",EDGE,"E94.MirrorCS")])],"isStart":true});
            var Q653;
            Q653=makeQuery(id+"F1.opExtrude","CAP_EDGE",EDGE,{"disambiguationData":[OSD([sQuery(id+"F0.wireOp",EDGE,"E125.MirrorC")])],"isStart":true});
            var Q654;
            Q654=makeQuery(id+"F1.opExtrude","CAP_EDGE",EDGE,{"disambiguationData":[OSD([sQuery(id+"F0.wireOp",EDGE,"E93.MirrorCS")])],"isStart":true});
            var Q655;
            Q655=makeQuery(id+"F1.opExtrude","CAP_EDGE",EDGE,{"disambiguationData":[OSD([sQuery(id+"F0.wireOp",EDGE,"E38.0")])],"isStart":true});
            var Q656;
            Q656=makeQuery(id+"F1.opExtrude","CAP_EDGE",EDGE,{"disambiguationData":[OSD([sQuery(id+"F0.wireOp",EDGE,"E55.trimOffspring")])],"isStart":true});
            var Q657;
            Q657=makeQuery(id+"F1.opExtrude","CAP_EDGE",EDGE,{"disambiguationData":[OSD([sQuery(id+"F0.wireOp",EDGE,"E4")])],"isStart":true});
            var Q658;
            Q658=makeQuery(id+"F1.opExtrude","CAP_EDGE",EDGE,{"disambiguationData":[OSD([sQuery(id+"F0.wireOp",EDGE,"E12")])],"isStart":true});
            var Q659;
            Q659=makeQuery(id+"F1.opExtrude","CAP_EDGE",EDGE,{"disambiguationData":[OSD([sQuery(id+"F0.wireOp",EDGE,"E30")])],"isStart":true});
            var Q660;
            Q660=makeQuery(id+"F1.opExtrude","CAP_EDGE",EDGE,{"disambiguationData":[OSD([sQuery(id+"F0.wireOp",EDGE,"E0.1")])],"isStart":true});
            var Q661;
            Q661=makeQuery(id+"F1.opExtrude","CAP_EDGE",EDGE,{"disambiguationData":[OSD([sQuery(id+"F0.wireOp",EDGE,"E11")])],"isStart":true});
            var Q662;
            Q662=makeQuery(id+"F1.opExtrude","CAP_EDGE",EDGE,{"disambiguationData":[OSD([sQuery(id+"F0.wireOp",EDGE,"E19")])],"isStart":true});
            var Q663;
            Q663=makeQuery(id+"F1.opExtrude","CAP_EDGE",EDGE,{"disambiguationData":[OSD([sQuery(id+"F0.wireOp",EDGE,"E2")])],"isStart":true});
            var Q664;
            Q664=makeQuery(id+"F1.opExtrude","CAP_EDGE",EDGE,{"disambiguationData":[OSD([sQuery(id+"F0.wireOp",EDGE,"E51.0"),sQuery(id+"F0.wireOp",EDGE,"E54")])],"isStart":true});
            var Q665;
            Q665=makeQuery(id+"F1.opExtrude","CAP_EDGE",EDGE,{"disambiguationData":[OSD([sQuery(id+"F0.wireOp",EDGE,"E3")])],"isStart":true});
            var Q666;
            Q666=makeQuery(id+"F1.opExtrude","CAP_EDGE",EDGE,{"disambiguationData":[OSD([sQuery(id+"F0.wireOp",EDGE,"E29")])],"isStart":true});
            var Q667;
            Q667=makeQuery(id+"F1.opExtrude","SWEPT_EDGE",EDGE,{"disambiguationData":[OSD([sQuery(id+"F0.wireOp",EDGE,"E12"),sQuery(id+"F0.wireOp",EDGE,"E22")])]});
            var Q668;
            Q668=makeQuery(id+"F1.opExtrude","CAP_EDGE",EDGE,{"disambiguationData":[OSD([sQuery(id+"F0.wireOp",EDGE,"E61.trimOffspring")])],"isStart":true});
            var Q669;
            Q669=makeQuery(id+"F1.opExtrude","CAP_EDGE",EDGE,{"disambiguationData":[OSD([sQuery(id+"F0.wireOp",EDGE,"E50.0"),sQuery(id+"F0.wireOp",EDGE,"E59")])],"isStart":true});
            var Q670;
            Q670=makeQuery(id+"F1.opExtrude","CAP_EDGE",EDGE,{"disambiguationData":[OSD([sQuery(id+"F0.wireOp",EDGE,"E62.trimOffspring")])],"isStart":true});
            var Q671;
            Q671=makeQuery(id+"F1.opExtrude","CAP_EDGE",EDGE,{"disambiguationData":[OSD([sQuery(id+"F0.wireOp",EDGE,"E10")])],"isStart":true});
            var Q672;
            Q672=makeQuery(id+"F1.opExtrude","CAP_EDGE",EDGE,{"disambiguationData":[OSD([sQuery(id+"F0.wireOp",EDGE,"E18")])],"isStart":true});
            var Q673;
            Q673=makeQuery(id+"F1.opExtrude","CAP_EDGE",EDGE,{"disambiguationData":[OSD([sQuery(id+"F0.wireOp",EDGE,"E28")])],"isStart":true});
            var Q674;
            Q674=makeQuery(id+"F1.opExtrude","CAP_EDGE",EDGE,{"disambiguationData":[OSD([sQuery(id+"F0.wireOp",EDGE,"E36.0"),sQuery(id+"F0.wireOp",EDGE,"E42"),sQuery(id+"F0.wireOp",EDGE,"E43")])],"isStart":true});
            var Q675;
            Q675=makeQuery(id+"F1.opExtrude","CAP_EDGE",EDGE,{"disambiguationData":[OSD([sQuery(id+"F0.wireOp",EDGE,"E49.0"),sQuery(id+"F0.wireOp",EDGE,"E53")])],"isStart":true});
            var Q676;
            Q676=makeQuery(id+"F1.opExtrude","CAP_EDGE",EDGE,{"disambiguationData":[OSD([sQuery(id+"F0.wireOp",EDGE,"E34")])],"isStart":true});
            var Q677;
            Q677=makeQuery(id+"F1.opExtrude","CAP_EDGE",EDGE,{"disambiguationData":[OSD([sQuery(id+"F0.wireOp",EDGE,"E48.0"),sQuery(id+"F0.wireOp",EDGE,"E52")])],"isStart":true});
            var Q678;
            Q678=makeQuery(id+"F1.opExtrude","CAP_EDGE",EDGE,{"disambiguationData":[OSD([sQuery(id+"F0.wireOp",EDGE,"E60")])],"isStart":true});
            var Q679;
            Q679=makeQuery(id+"F1.opExtrude","CAP_EDGE",EDGE,{"disambiguationData":[OSD([sQuery(id+"F0.wireOp",EDGE,"E0.5")])],"isStart":true});
            var Q680;
            {var subQ0=sQuery(id+"F0.wireOp",EDGE,"E9");Q680=makeQuery(id+"F1.opExtrude","CAP_EDGE",EDGE,{"disambiguationData":[OSD([subQ0]),TDD([makeQuery(id+"F0.imprint","IMPRINT",EDGE,{"disambiguationData":[TD([[makeQuery(id+"F0.imprint","INTERSECT",VERTEX,{"derivedFrom":[sQuery(id+"F0.wireOp",EDGE,"E0.4"),subQ0]}),-1.0]])],"derivedFrom":subQ0})])],"isStart":true});}
            var Q681;
            Q681=makeQuery(id+"F1.opExtrude","CAP_EDGE",EDGE,{"disambiguationData":[OSD([sQuery(id+"F0.wireOp",EDGE,"E16")])],"isStart":true});
            var Q682;
            Q682=makeQuery(id+"F1.opExtrude","CAP_EDGE",EDGE,{"disambiguationData":[OSD([sQuery(id+"F0.wireOp",EDGE,"E26")])],"isStart":true});
            var Q683;
            {var subQ0=sQuery(id+"F0.wireOp",EDGE,"E9");Q683=makeQuery(id+"F1.opExtrude","CAP_EDGE",EDGE,{"disambiguationData":[OSD([subQ0]),TDD([makeQuery(id+"F0.imprint","IMPRINT",EDGE,{"disambiguationData":[TD([[makeQuery(id+"F0.imprint","INTERSECT",VERTEX,{"derivedFrom":[sQuery(id+"F0.wireOp",EDGE,"E0.3"),subQ0]}),1.0]])],"derivedFrom":subQ0})])],"isStart":true});}
            var Q684;
            Q684=makeQuery(id+"F1.opExtrude","CAP_EDGE",EDGE,{"disambiguationData":[OSD([sQuery(id+"F0.wireOp",EDGE,"E17")])],"isStart":true});
            var Q685;
            Q685=makeQuery(id+"F1.opExtrude","CAP_EDGE",EDGE,{"disambiguationData":[OSD([sQuery(id+"F0.wireOp",EDGE,"E27")])],"isStart":true});
            var Q686;
            Q686=makeQuery(id+"F1.opExtrude","CAP_EDGE",EDGE,{"disambiguationData":[OSD([sQuery(id+"F0.wireOp",EDGE,"E35.0"),sQuery(id+"F0.wireOp",EDGE,"E41"),sQuery(id+"F0.wireOp",EDGE,"E44")])],"isStart":true});
            var Q687;
            Q687=makeQuery(id+"F1.opExtrude","CAP_EDGE",EDGE,{"disambiguationData":[OSD([sQuery(id+"F0.wireOp",EDGE,"E1")])],"isStart":true});
            var Q688;
            Q688=makeQuery(id+"F1.opExtrude","CAP_EDGE",EDGE,{"disambiguationData":[OSD([sQuery(id+"F0.wireOp",EDGE,"E57.trimOffspring")])],"isStart":true});
            var Q689;
            Q689=makeQuery(id+"F1.opExtrude","CAP_EDGE",EDGE,{"disambiguationData":[OSD([sQuery(id+"F0.wireOp",EDGE,"E7")])],"isStart":true});
            var Q690;
            Q690=makeQuery(id+"F1.opExtrude","CAP_EDGE",EDGE,{"disambiguationData":[OSD([sQuery(id+"F0.wireOp",EDGE,"E32")])],"isStart":true});
            var Q691;
            Q691=makeQuery(id+"F1.opExtrude","CAP_EDGE",EDGE,{"disambiguationData":[OSD([sQuery(id+"F0.wireOp",EDGE,"E24.trimOffspring")])],"isStart":true});
            var Q692;
            Q692=makeQuery(id+"F1.opExtrude","CAP_EDGE",EDGE,{"disambiguationData":[OSD([sQuery(id+"F0.wireOp",EDGE,"E33")])],"isStart":true});
            var Q693;
            Q693=makeQuery(id+"F1.opExtrude","CAP_EDGE",EDGE,{"disambiguationData":[OSD([sQuery(id+"F0.wireOp",EDGE,"E47.0")])],"isStart":true});
            var Q694;
            Q694=makeQuery(id+"F1.opExtrude","CAP_EDGE",EDGE,{"disambiguationData":[OSD([sQuery(id+"F0.wireOp",EDGE,"E58")])],"isStart":true});
            var Q695;
            Q695=makeQuery(id+"F1.opExtrude","CAP_EDGE",EDGE,{"disambiguationData":[OSD([sQuery(id+"F0.wireOp",EDGE,"E0.4")])],"isStart":true});
            var Q696;
            Q696=makeQuery(id+"F1.opExtrude","CAP_EDGE",EDGE,{"disambiguationData":[OSD([sQuery(id+"F0.wireOp",EDGE,"E8")])],"isStart":true});
            var Q697;
            Q697=makeQuery(id+"F1.opExtrude","CAP_EDGE",EDGE,{"disambiguationData":[OSD([sQuery(id+"F0.wireOp",EDGE,"E15")])],"isStart":true});
            var Q698;
            Q698=makeQuery(id+"F1.opExtrude","CAP_EDGE",EDGE,{"disambiguationData":[OSD([sQuery(id+"F0.wireOp",EDGE,"E39.0"),sQuery(id+"F0.wireOp",EDGE,"E46")])],"isStart":true});
            var Q699;
            Q699=makeQuery(id+"F1.opExtrude","CAP_EDGE",EDGE,{"disambiguationData":[OSD([sQuery(id+"F0.wireOp",EDGE,"E56")])],"isStart":true});
            var Q700;
            Q700=makeQuery(id+"F1.opExtrude","CAP_EDGE",EDGE,{"disambiguationData":[OSD([sQuery(id+"F0.wireOp",EDGE,"E6")])],"isStart":true});
            var Q701;
            Q701=makeQuery(id+"F1.opExtrude","CAP_EDGE",EDGE,{"disambiguationData":[OSD([sQuery(id+"F0.wireOp",EDGE,"E13")])],"isStart":true});
            var Q702;
            Q702=makeQuery(id+"F1.opExtrude","CAP_EDGE",EDGE,{"disambiguationData":[OSD([sQuery(id+"F0.wireOp",EDGE,"E21")])],"isStart":true});
            var Q703;
            Q703=makeQuery(id+"F1.opExtrude","CAP_EDGE",EDGE,{"disambiguationData":[OSD([sQuery(id+"F0.wireOp",EDGE,"E31")])],"isStart":true});
            var Q704;
            Q704=makeQuery(id+"F1.opExtrude","CAP_EDGE",EDGE,{"disambiguationData":[OSD([sQuery(id+"F0.wireOp",EDGE,"E0.2")])],"isStart":true});
            var Q705;
            Q705=makeQuery(id+"F2.opExtrude","SWEPT_EDGE",EDGE,{"disambiguationData":[OSD([sQuery(id+"F0.wireOp",EDGE,"E47.0"),sQuery(id+"F0.wireOp",EDGE,"E51.0")])]});
            var Q706;
            Q706=makeQuery(id+"F2.opExtrude","SWEPT_EDGE",EDGE,{"disambiguationData":[OSD([sQuery(id+"F0.wireOp",EDGE,"E47.0"),sQuery(id+"F0.wireOp",EDGE,"E48.0")])]});
            var Q707;
            Q707=makeQuery(id+"F2.opExtrude","SWEPT_EDGE",EDGE,{"disambiguationData":[OSD([sQuery(id+"F0.wireOp",EDGE,"E58"),sQuery(id+"F0.wireOp",EDGE,"E59")])]});
            var Q708;
            Q708=makeQuery(id+"F2.opExtrude","SWEPT_EDGE",EDGE,{"disambiguationData":[OSD([sQuery(id+"F0.wireOp",EDGE,"E9"),sQuery(id+"F0.wireOp",EDGE,"E20")])]});
            var Q709;
            Q709=makeQuery(id+"F2.opExtrude","SWEPT_EDGE",EDGE,{"disambiguationData":[OSD([sQuery(id+"F0.wireOp",EDGE,"E9"),sQuery(id+"F0.wireOp",EDGE,"E19")])]});
            var Q710;
            Q710=makeQuery(id+"F2.opExtrude","SWEPT_EDGE",EDGE,{"disambiguationData":[OSD([sQuery(id+"F0.wireOp",EDGE,"E53"),sQuery(id+"F0.wireOp",EDGE,"E61.trimOffspring")])]});
            var Q711;
            Q711=makeQuery(id+"F2.opExtrude","SWEPT_EDGE",EDGE,{"disambiguationData":[OSD([sQuery(id+"F0.wireOp",EDGE,"E54"),sQuery(id+"F0.wireOp",EDGE,"E58")])]});
            var Q712;
            Q712=makeQuery(id+"F2.opExtrude","SWEPT_EDGE",EDGE,{"disambiguationData":[OSD([sQuery(id+"F0.wireOp",EDGE,"E17"),sQuery(id+"F0.wireOp",EDGE,"E57.trimOffspring")])]});
            var Q713;
            Q713=makeQuery(id+"F2.opExtrude","SWEPT_EDGE",EDGE,{"disambiguationData":[OSD([sQuery(id+"F0.wireOp",EDGE,"E52"),sQuery(id+"F0.wireOp",EDGE,"E61.trimOffspring")])]});
            var Q714;
            Q714=makeQuery(id+"F2.opExtrude","SWEPT_EDGE",EDGE,{"disambiguationData":[OSD([sQuery(id+"F0.wireOp",EDGE,"E18"),sQuery(id+"F0.wireOp",EDGE,"E24.trimOffspring")])]});
            var Q715;
            Q715=makeQuery(id+"F2.opExtrude","CAP_EDGE",EDGE,{"disambiguationData":[OSD([sQuery(id+"F0.wireOp",EDGE,"E22")])],"isStart":false});
            var Q716;
            Q716=makeQuery(id+"F2.opExtrude","SWEPT_EDGE",EDGE,{"disambiguationData":[OSD([sQuery(id+"F0.wireOp",EDGE,"E49.0"),sQuery(id+"F0.wireOp",EDGE,"E50.0")])]});
            var Q717;
            Q717=makeQuery(id+"F2.opExtrude","SWEPT_EDGE",EDGE,{"disambiguationData":[OSD([sQuery(id+"F0.wireOp",EDGE,"E10"),sQuery(id+"F0.wireOp",EDGE,"E13")])]});
            var Q718;
            Q718=makeQuery(id+"F2.opExtrude","SWEPT_EDGE",EDGE,{"disambiguationData":[OSD([sQuery(id+"F0.wireOp",EDGE,"E12"),sQuery(id+"F0.wireOp",EDGE,"E21")])]});
            var Q719;
            Q719=makeQuery(id+"F2.opExtrude","SWEPT_EDGE",EDGE,{"disambiguationData":[OSD([sQuery(id+"F0.wireOp",EDGE,"E45"),sQuery(id+"F0.wireOp",EDGE,"E56")])]});
            var Q720;
            Q720=makeQuery(id+"F2.opExtrude","SWEPT_EDGE",EDGE,{"disambiguationData":[OSD([sQuery(id+"F0.wireOp",EDGE,"E46"),sQuery(id+"F0.wireOp",EDGE,"E56")])]});
            var Q721;
            Q721=makeQuery(id+"F2.opExtrude","SWEPT_EDGE",EDGE,{"disambiguationData":[OSD([sQuery(id+"F0.wireOp",EDGE,"E38.0"),sQuery(id+"F0.wireOp",EDGE,"E39.0")])]});
            var Q722;
            Q722=makeQuery(id+"F2.opExtrude","SWEPT_EDGE",EDGE,{"disambiguationData":[OSD([sQuery(id+"F0.wireOp",EDGE,"E37.0"),sQuery(id+"F0.wireOp",EDGE,"E38.0")])]});
            var Q723;
            Q723=makeQuery(id+"F2.opExtrude","SWEPT_EDGE",EDGE,{"disambiguationData":[OSD([sQuery(id+"F0.wireOp",EDGE,"E21"),sQuery(id+"F0.wireOp",EDGE,"E62.trimOffspring")])]});
            var Q724;
            Q724=makeQuery(id+"F2.opExtrude","SWEPT_EDGE",EDGE,{"disambiguationData":[OSD([sQuery(id+"F0.wireOp",EDGE,"E42"),sQuery(id+"F0.wireOp",EDGE,"E55.trimOffspring")])]});
            var Q725;
            Q725=makeQuery(id+"F2.opExtrude","SWEPT_EDGE",EDGE,{"disambiguationData":[OSD([sQuery(id+"F0.wireOp",EDGE,"E6"),sQuery(id+"F0.wireOp",EDGE,"E22")])]});
            var Q726;
            Q726=makeQuery(id+"F2.opExtrude","SWEPT_EDGE",EDGE,{"disambiguationData":[OSD([sQuery(id+"F0.wireOp",EDGE,"E41"),sQuery(id+"F0.wireOp",EDGE,"E55.trimOffspring")])]});
            var Q727;
            Q727=makeQuery(id+"F2.opExtrude","SWEPT_EDGE",EDGE,{"disambiguationData":[OSD([sQuery(id+"F0.wireOp",EDGE,"E93.MirrorCS"),sQuery(id+"F0.wireOp",EDGE,"E121.MirrorCS")])]});
            var Q728;
            Q728=makeQuery(id+"F2.opExtrude","SWEPT_EDGE",EDGE,{"disambiguationData":[OSD([sQuery(id+"F0.wireOp",EDGE,"E66.MirrorCS"),sQuery(id+"F0.wireOp",EDGE,"E80.MirrorCS")])]});
            var Q729;
            Q729=makeQuery(id+"F2.opExtrude","SWEPT_EDGE",EDGE,{"disambiguationData":[OSD([sQuery(id+"F0.wireOp",EDGE,"E74.MirrorCS"),sQuery(id+"F0.wireOp",EDGE,"E100.MirrorCS")])]});
            var Q730;
            Q730=makeQuery(id+"F2.opExtrude","SWEPT_EDGE",EDGE,{"disambiguationData":[OSD([sQuery(id+"F0.wireOp",EDGE,"E100.MirrorCS"),sQuery(id+"F0.wireOp",EDGE,"E124.MirrorCS")])]});
            var Q731;
            Q731=makeQuery(id+"F2.opExtrude","CAP_EDGE",EDGE,{"disambiguationData":[OSD([sQuery(id+"F0.wireOp",EDGE,"E65.MirrorCS")])],"isStart":false});
            var Q732;
            Q732=makeQuery(id+"F2.opExtrude","SWEPT_EDGE",EDGE,{"disambiguationData":[OSD([sQuery(id+"F0.wireOp",EDGE,"E122.MirrorCS"),sQuery(id+"F0.wireOp",EDGE,"E108.MirrorCS")])]});
            var Q733;
            Q733=makeQuery(id+"F2.opExtrude","SWEPT_EDGE",EDGE,{"disambiguationData":[OSD([sQuery(id+"F0.wireOp",EDGE,"E94.MirrorCS"),sQuery(id+"F0.wireOp",EDGE,"E121.MirrorCS")])]});
            var Q734;
            Q734=makeQuery(id+"F2.opExtrude","SWEPT_EDGE",EDGE,{"disambiguationData":[OSD([sQuery(id+"F0.wireOp",EDGE,"E87.MirrorCS"),sQuery(id+"F0.wireOp",EDGE,"E114.MirrorCS")])]});
            var Q735;
            Q735=makeQuery(id+"F2.opExtrude","SWEPT_EDGE",EDGE,{"disambiguationData":[OSD([sQuery(id+"F0.wireOp",EDGE,"E120.MirrorCS"),sQuery(id+"F0.wireOp",EDGE,"E117.MirrorCS")])]});
            var Q736;
            Q736=makeQuery(id+"F2.opExtrude","SWEPT_EDGE",EDGE,{"disambiguationData":[OSD([sQuery(id+"F0.wireOp",EDGE,"E98.MirrorCS"),sQuery(id+"F0.wireOp",EDGE,"E106.MirrorCS")])]});
            var Q737;
            Q737=makeQuery(id+"F2.opExtrude","SWEPT_EDGE",EDGE,{"disambiguationData":[OSD([sQuery(id+"F0.wireOp",EDGE,"E114.MirrorCS"),sQuery(id+"F0.wireOp",EDGE,"E104.MirrorCS")])]});
            var Q738;
            Q738=makeQuery(id+"F2.opExtrude","SWEPT_EDGE",EDGE,{"disambiguationData":[OSD([sQuery(id+"F0.wireOp",EDGE,"E101.MirrorCS"),sQuery(id+"F0.wireOp",EDGE,"E111.MirrorCS")])]});
            var Q739;
            Q739=makeQuery(id+"F2.opExtrude","SWEPT_EDGE",EDGE,{"disambiguationData":[OSD([sQuery(id+"F0.wireOp",EDGE,"E105.MirrorCS"),sQuery(id+"F0.wireOp",EDGE,"E108.MirrorCS")])]});
            var Q740;
            Q740=makeQuery(id+"F2.opExtrude","SWEPT_EDGE",EDGE,{"disambiguationData":[OSD([sQuery(id+"F0.wireOp",EDGE,"E87.MirrorCS"),sQuery(id+"F0.wireOp",EDGE,"E115.MirrorCS")])]});
            var Q741;
            Q741=makeQuery(id+"F2.opExtrude","SWEPT_EDGE",EDGE,{"disambiguationData":[OSD([sQuery(id+"F0.wireOp",EDGE,"E88.MirrorCS"),sQuery(id+"F0.wireOp",EDGE,"E71.MirrorCS")])]});
            var Q742;
            Q742=makeQuery(id+"F2.opExtrude","SWEPT_EDGE",EDGE,{"disambiguationData":[OSD([sQuery(id+"F0.wireOp",EDGE,"E95.MirrorCS"),sQuery(id+"F0.wireOp",EDGE,"E124.MirrorCS")])]});
            var Q743;
            Q743=makeQuery(id+"F2.opExtrude","SWEPT_EDGE",EDGE,{"disambiguationData":[OSD([sQuery(id+"F0.wireOp",EDGE,"E67.MirrorCS"),sQuery(id+"F0.wireOp",EDGE,"E65.MirrorCS")])]});
            var Q744;
            Q744=makeQuery(id+"F2.opExtrude","SWEPT_EDGE",EDGE,{"disambiguationData":[OSD([sQuery(id+"F0.wireOp",EDGE,"E70.MirrorCS"),sQuery(id+"F0.wireOp",EDGE,"E65.MirrorCS")])]});
            var Q745;
            Q745=makeQuery(id+"F2.opExtrude","SWEPT_EDGE",EDGE,{"disambiguationData":[OSD([sQuery(id+"F0.wireOp",EDGE,"E82.MirrorCS"),sQuery(id+"F0.wireOp",EDGE,"E90.MirrorCS")])]});
            var Q746;
            Q746=makeQuery(id+"F2.opExtrude","SWEPT_EDGE",EDGE,{"disambiguationData":[OSD([sQuery(id+"F0.wireOp",EDGE,"E109.MirrorCS"),sQuery(id+"F0.wireOp",EDGE,"E81.MirrorCS")])]});
            var Q747;
            Q747=makeQuery(id+"F2.opExtrude","SWEPT_EDGE",EDGE,{"disambiguationData":[OSD([sQuery(id+"F0.wireOp",EDGE,"E92.MirrorCS"),sQuery(id+"F0.wireOp",EDGE,"E93.MirrorCS")])]});
            var Q748;
            Q748=makeQuery(id+"F2.opExtrude","SWEPT_EDGE",EDGE,{"disambiguationData":[OSD([sQuery(id+"F0.wireOp",EDGE,"E74.MirrorCS"),sQuery(id+"F0.wireOp",EDGE,"E95.MirrorCS")])]});
            var Q749;
            Q749=makeQuery(id+"F2.opExtrude","SWEPT_EDGE",EDGE,{"disambiguationData":[OSD([sQuery(id+"F0.wireOp",EDGE,"E82.MirrorCS"),sQuery(id+"F0.wireOp",EDGE,"E116.MirrorCS")])]});
            var Q750;
            Q750=makeQuery(id+"F2.opExtrude","SWEPT_EDGE",EDGE,{"disambiguationData":[OSD([sQuery(id+"F0.wireOp",EDGE,"E68.MirrorCS"),sQuery(id+"F0.wireOp",EDGE,"E89.MirrorCS")])]});
            var Q751;
            Q751=makeQuery(id+"F2.opExtrude","SWEPT_EDGE",EDGE,{"disambiguationData":[OSD([sQuery(id+"F0.wireOp",EDGE,"E72.MirrorCS"),sQuery(id+"F0.wireOp",EDGE,"E110.MirrorCS")])]});
            var Q752;
            Q752=makeQuery(id+"F1.opExtrude","CAP_EDGE",EDGE,{"disambiguationData":[OSD([sQuery(id+"F0.wireOp",EDGE,"E65.MirrorCS")])],"isStart":true});
            var Q753;
            Q753=makeQuery(id+"F1.opExtrude","CAP_EDGE",EDGE,{"disambiguationData":[OSD([sQuery(id+"F0.wireOp",EDGE,"E22")])],"isStart":true});
            var Q754;
            Q754=makeQuery(id+"F2.opExtrude","CAP_EDGE",EDGE,{"disambiguationData":[OSD([sQuery(id+"F0.wireOp",EDGE,"E51.0"),sQuery(id+"F0.wireOp",EDGE,"E54")])],"isStart":true});
            var Q755;
            Q755=makeQuery(id+"F2.opExtrude","CAP_EDGE",EDGE,{"disambiguationData":[OSD([sQuery(id+"F0.wireOp",EDGE,"E60")])],"isStart":true});
            var Q756;
            Q756=makeQuery(id+"F2.opExtrude","CAP_EDGE",EDGE,{"disambiguationData":[OSD([sQuery(id+"F0.wireOp",EDGE,"E26")])],"isStart":true});
            var Q757;
            Q757=makeQuery(id+"F2.opExtrude","CAP_EDGE",EDGE,{"disambiguationData":[OSD([sQuery(id+"F0.wireOp",EDGE,"E62.trimOffspring")])],"isStart":true});
            var Q758;
            Q758=makeQuery(id+"F2.opExtrude","CAP_EDGE",EDGE,{"disambiguationData":[OSD([sQuery(id+"F0.wireOp",EDGE,"E16")])],"isStart":true});
            var Q759;
            Q759=makeQuery(id+"F2.opExtrude","CAP_EDGE",EDGE,{"disambiguationData":[OSD([sQuery(id+"F0.wireOp",EDGE,"E34")])],"isStart":true});
            var Q760;
            Q760=makeQuery(id+"F2.opExtrude","CAP_EDGE",EDGE,{"disambiguationData":[OSD([sQuery(id+"F0.wireOp",EDGE,"E0.5")])],"isStart":true});
            var Q761;
            Q761=makeQuery(id+"F2.opExtrude","CAP_EDGE",EDGE,{"disambiguationData":[OSD([sQuery(id+"F0.wireOp",EDGE,"E4")])],"isStart":true});
            var Q762;
            Q762=makeQuery(id+"F2.opExtrude","CAP_EDGE",EDGE,{"disambiguationData":[OSD([sQuery(id+"F0.wireOp",EDGE,"E3")])],"isStart":true});
            var Q763;
            Q763=makeQuery(id+"F2.opExtrude","CAP_EDGE",EDGE,{"disambiguationData":[OSD([sQuery(id+"F0.wireOp",EDGE,"E19")])],"isStart":true});
            var Q764;
            Q764=makeQuery(id+"F2.opExtrude","CAP_EDGE",EDGE,{"disambiguationData":[OSD([sQuery(id+"F0.wireOp",EDGE,"E0.1")])],"isStart":true});
            var Q765;
            Q765=makeQuery(id+"F2.opExtrude","CAP_EDGE",EDGE,{"disambiguationData":[OSD([sQuery(id+"F0.wireOp",EDGE,"E12")])],"isStart":true});
            var Q766;
            Q766=makeQuery(id+"F2.opExtrude","CAP_EDGE",EDGE,{"disambiguationData":[OSD([sQuery(id+"F0.wireOp",EDGE,"E30")])],"isStart":true});
            var Q767;
            Q767=makeQuery(id+"F2.opExtrude","CAP_EDGE",EDGE,{"disambiguationData":[OSD([sQuery(id+"F0.wireOp",EDGE,"E38.0")])],"isStart":true});
            var Q768;
            Q768=makeQuery(id+"F2.opExtrude","CAP_EDGE",EDGE,{"disambiguationData":[OSD([sQuery(id+"F0.wireOp",EDGE,"E11")])],"isStart":true});
            var Q769;
            Q769=makeQuery(id+"F2.opExtrude","CAP_EDGE",EDGE,{"disambiguationData":[OSD([sQuery(id+"F0.wireOp",EDGE,"E29")])],"isStart":true});
            var Q770;
            Q770=makeQuery(id+"F2.opExtrude","CAP_EDGE",EDGE,{"disambiguationData":[OSD([sQuery(id+"F0.wireOp",EDGE,"E35.0"),sQuery(id+"F0.wireOp",EDGE,"E41"),sQuery(id+"F0.wireOp",EDGE,"E44")])],"isStart":true});
            var Q771;
            Q771=makeQuery(id+"F2.opExtrude","CAP_EDGE",EDGE,{"disambiguationData":[OSD([sQuery(id+"F0.wireOp",EDGE,"E55.trimOffspring")])],"isStart":true});
            var Q772;
            Q772=makeQuery(id+"F2.opExtrude","CAP_EDGE",EDGE,{"disambiguationData":[OSD([sQuery(id+"F0.wireOp",EDGE,"E49.0"),sQuery(id+"F0.wireOp",EDGE,"E53")])],"isStart":true});
            var Q773;
            Q773=makeQuery(id+"F2.opExtrude","CAP_EDGE",EDGE,{"disambiguationData":[OSD([sQuery(id+"F0.wireOp",EDGE,"E48.0"),sQuery(id+"F0.wireOp",EDGE,"E52")])],"isStart":true});
            var Q774;
            Q774=makeQuery(id+"F2.opExtrude","CAP_EDGE",EDGE,{"disambiguationData":[OSD([sQuery(id+"F0.wireOp",EDGE,"E61.trimOffspring")])],"isStart":true});
            var Q775;
            Q775=makeQuery(id+"F2.opExtrude","CAP_EDGE",EDGE,{"disambiguationData":[OSD([sQuery(id+"F0.wireOp",EDGE,"E36.0"),sQuery(id+"F0.wireOp",EDGE,"E42"),sQuery(id+"F0.wireOp",EDGE,"E43")])],"isStart":true});
            var Q776;
            {var subQ0=sQuery(id+"F0.wireOp",EDGE,"E9");Q776=makeQuery(id+"F2.opExtrude","CAP_EDGE",EDGE,{"disambiguationData":[OSD([subQ0]),TDD([makeQuery(id+"F0.imprint","IMPRINT",EDGE,{"disambiguationData":[TD([[makeQuery(id+"F0.imprint","INTERSECT",VERTEX,{"derivedFrom":[sQuery(id+"F0.wireOp",EDGE,"E0.4"),subQ0]}),-1.0]])],"derivedFrom":subQ0})])],"isStart":true});}
            var Q777;
            Q777=makeQuery(id+"F2.opExtrude","CAP_EDGE",EDGE,{"disambiguationData":[OSD([sQuery(id+"F0.wireOp",EDGE,"E17")])],"isStart":true});
            var Q778;
            Q778=makeQuery(id+"F2.opExtrude","SWEPT_EDGE",EDGE,{"disambiguationData":[OSD([sQuery(id+"F0.wireOp",EDGE,"E12"),sQuery(id+"F0.wireOp",EDGE,"E22")])]});
            var Q779;
            Q779=makeQuery(id+"F2.opExtrude","CAP_EDGE",EDGE,{"disambiguationData":[OSD([sQuery(id+"F0.wireOp",EDGE,"E28")])],"isStart":true});
            var Q780;
            Q780=makeQuery(id+"F2.opExtrude","CAP_EDGE",EDGE,{"disambiguationData":[OSD([sQuery(id+"F0.wireOp",EDGE,"E1")])],"isStart":true});
            var Q781;
            Q781=makeQuery(id+"F2.opExtrude","CAP_EDGE",EDGE,{"disambiguationData":[OSD([sQuery(id+"F0.wireOp",EDGE,"E18")])],"isStart":true});
            var Q782;
            Q782=makeQuery(id+"F2.opExtrude","CAP_EDGE",EDGE,{"disambiguationData":[OSD([sQuery(id+"F0.wireOp",EDGE,"E27")])],"isStart":true});
            var Q783;
            Q783=makeQuery(id+"F2.opExtrude","CAP_EDGE",EDGE,{"disambiguationData":[OSD([sQuery(id+"F0.wireOp",EDGE,"E2")])],"isStart":true});
            var Q784;
            {var subQ0=sQuery(id+"F0.wireOp",EDGE,"E9");Q784=makeQuery(id+"F2.opExtrude","CAP_EDGE",EDGE,{"disambiguationData":[OSD([subQ0]),TDD([makeQuery(id+"F0.imprint","IMPRINT",EDGE,{"disambiguationData":[TD([[makeQuery(id+"F0.imprint","INTERSECT",VERTEX,{"derivedFrom":[sQuery(id+"F0.wireOp",EDGE,"E0.3"),subQ0]}),1.0]])],"derivedFrom":subQ0})])],"isStart":true});}
            var Q785;
            Q785=makeQuery(id+"F2.opExtrude","CAP_EDGE",EDGE,{"disambiguationData":[OSD([sQuery(id+"F0.wireOp",EDGE,"E10")])],"isStart":true});
            var Q786;
            Q786=makeQuery(id+"F2.opExtrude","CAP_EDGE",EDGE,{"disambiguationData":[OSD([sQuery(id+"F0.wireOp",EDGE,"E50.0"),sQuery(id+"F0.wireOp",EDGE,"E59")])],"isStart":true});
            var Q787;
            Q787=makeQuery(id+"F2.opExtrude","CAP_EDGE",EDGE,{"disambiguationData":[OSD([sQuery(id+"F0.wireOp",EDGE,"E57.trimOffspring")])],"isStart":true});
            var Q788;
            Q788=makeQuery(id+"F2.opExtrude","CAP_EDGE",EDGE,{"disambiguationData":[OSD([sQuery(id+"F0.wireOp",EDGE,"E32")])],"isStart":true});
            var Q789;
            Q789=makeQuery(id+"F2.opExtrude","CAP_EDGE",EDGE,{"disambiguationData":[OSD([sQuery(id+"F0.wireOp",EDGE,"E7")])],"isStart":true});
            var Q790;
            Q790=makeQuery(id+"F2.opExtrude","CAP_EDGE",EDGE,{"disambiguationData":[OSD([sQuery(id+"F0.wireOp",EDGE,"E56")])],"isStart":true});
            var Q791;
            Q791=makeQuery(id+"F2.opExtrude","CAP_EDGE",EDGE,{"disambiguationData":[OSD([sQuery(id+"F0.wireOp",EDGE,"E39.0"),sQuery(id+"F0.wireOp",EDGE,"E46")])],"isStart":true});
            var Q792;
            Q792=makeQuery(id+"F2.opExtrude","CAP_EDGE",EDGE,{"disambiguationData":[OSD([sQuery(id+"F0.wireOp",EDGE,"E31")])],"isStart":true});
            var Q793;
            Q793=makeQuery(id+"F2.opExtrude","CAP_EDGE",EDGE,{"disambiguationData":[OSD([sQuery(id+"F0.wireOp",EDGE,"E21")])],"isStart":true});
            var Q794;
            Q794=makeQuery(id+"F2.opExtrude","CAP_EDGE",EDGE,{"disambiguationData":[OSD([sQuery(id+"F0.wireOp",EDGE,"E13")])],"isStart":true});
            var Q795;
            Q795=makeQuery(id+"F2.opExtrude","CAP_EDGE",EDGE,{"disambiguationData":[OSD([sQuery(id+"F0.wireOp",EDGE,"E6")])],"isStart":true});
            var Q796;
            Q796=makeQuery(id+"F2.opExtrude","CAP_EDGE",EDGE,{"disambiguationData":[OSD([sQuery(id+"F0.wireOp",EDGE,"E0.2")])],"isStart":true});
            var Q797;
            Q797=makeQuery(id+"F2.opExtrude","CAP_EDGE",EDGE,{"disambiguationData":[OSD([sQuery(id+"F0.wireOp",EDGE,"E58")])],"isStart":true});
            var Q798;
            Q798=makeQuery(id+"F2.opExtrude","CAP_EDGE",EDGE,{"disambiguationData":[OSD([sQuery(id+"F0.wireOp",EDGE,"E47.0")])],"isStart":true});
            var Q799;
            Q799=makeQuery(id+"F2.opExtrude","CAP_EDGE",EDGE,{"disambiguationData":[OSD([sQuery(id+"F0.wireOp",EDGE,"E33")])],"isStart":true});
            var Q800;
            Q800=makeQuery(id+"F2.opExtrude","CAP_EDGE",EDGE,{"disambiguationData":[OSD([sQuery(id+"F0.wireOp",EDGE,"E24.trimOffspring")])],"isStart":true});
            var Q801;
            Q801=makeQuery(id+"F2.opExtrude","CAP_EDGE",EDGE,{"disambiguationData":[OSD([sQuery(id+"F0.wireOp",EDGE,"E15")])],"isStart":true});
            var Q802;
            Q802=makeQuery(id+"F2.opExtrude","CAP_EDGE",EDGE,{"disambiguationData":[OSD([sQuery(id+"F0.wireOp",EDGE,"E8")])],"isStart":true});
            var Q803;
            Q803=makeQuery(id+"F2.opExtrude","CAP_EDGE",EDGE,{"disambiguationData":[OSD([sQuery(id+"F0.wireOp",EDGE,"E0.4")])],"isStart":true});
            var Q804;
            Q804=makeQuery(id+"F2.opExtrude","CAP_EDGE",EDGE,{"disambiguationData":[OSD([sQuery(id+"F0.wireOp",EDGE,"E86.MirrorC")])],"isStart":true});
            var Q805;
            Q805=makeQuery(id+"F2.opExtrude","CAP_EDGE",EDGE,{"disambiguationData":[OSD([sQuery(id+"F0.wireOp",EDGE,"E92.MirrorCS")])],"isStart":true});
            var Q806;
            Q806=makeQuery(id+"F2.opExtrude","CAP_EDGE",EDGE,{"disambiguationData":[OSD([sQuery(id+"F0.wireOp",EDGE,"E71.MirrorCS"),sQuery(id+"F0.wireOp",EDGE,"E111.MirrorCS")])],"isStart":true});
            var Q807;
            Q807=makeQuery(id+"F2.opExtrude","CAP_EDGE",EDGE,{"disambiguationData":[OSD([sQuery(id+"F0.wireOp",EDGE,"E68.MirrorCS"),sQuery(id+"F0.wireOp",EDGE,"E77.MirrorCS"),sQuery(id+"F0.wireOp",EDGE,"E72.MirrorCS")])],"isStart":true});
            var Q808;
            Q808=makeQuery(id+"F2.opExtrude","CAP_EDGE",EDGE,{"disambiguationData":[OSD([sQuery(id+"F0.wireOp",EDGE,"E99.MirrorC")])],"isStart":true});
            var Q809;
            Q809=makeQuery(id+"F2.opExtrude","CAP_EDGE",EDGE,{"disambiguationData":[OSD([sQuery(id+"F0.wireOp",EDGE,"E122.MirrorCS")])],"isStart":true});
            var Q810;
            Q810=makeQuery(id+"F2.opExtrude","CAP_EDGE",EDGE,{"disambiguationData":[OSD([sQuery(id+"F0.wireOp",EDGE,"E75.MirrorCS")])],"isStart":true});
            var Q811;
            {var subQ0=sQuery(id+"F0.wireOp",EDGE,"E74.MirrorCS");Q811=makeQuery(id+"F2.opExtrude","CAP_EDGE",EDGE,{"disambiguationData":[OSD([subQ0]),TDD([makeQuery(id+"F0.imprint","IMPRINT",EDGE,{"disambiguationData":[TD([[makeQuery(id+"F0.imprint","INTERSECT",VERTEX,{"derivedFrom":[sQuery(id+"F0.wireOp",EDGE,"E76.MirrorCS"),subQ0]}),1.0]])],"derivedFrom":subQ0})])],"isStart":true});}
            var Q812;
            Q812=makeQuery(id+"F2.opExtrude","CAP_EDGE",EDGE,{"disambiguationData":[OSD([sQuery(id+"F0.wireOp",EDGE,"E119.MirrorCS")])],"isStart":true});
            var Q813;
            Q813=makeQuery(id+"F2.opExtrude","CAP_EDGE",EDGE,{"disambiguationData":[OSD([sQuery(id+"F0.wireOp",EDGE,"E73.MirrorCS"),sQuery(id+"F0.wireOp",EDGE,"E96.MirrorCS")])],"isStart":true});
            var Q814;
            Q814=makeQuery(id+"F2.opExtrude","CAP_EDGE",EDGE,{"disambiguationData":[OSD([sQuery(id+"F0.wireOp",EDGE,"E113.MirrorCS")])],"isStart":true});
            var Q815;
            Q815=makeQuery(id+"F2.opExtrude","CAP_EDGE",EDGE,{"disambiguationData":[OSD([sQuery(id+"F0.wireOp",EDGE,"E124.MirrorCS")])],"isStart":true});
            var Q816;
            Q816=makeQuery(id+"F2.opExtrude","CAP_EDGE",EDGE,{"disambiguationData":[OSD([sQuery(id+"F0.wireOp",EDGE,"E91.MirrorC")])],"isStart":true});
            var Q817;
            Q817=makeQuery(id+"F2.opExtrude","CAP_EDGE",EDGE,{"disambiguationData":[OSD([sQuery(id+"F0.wireOp",EDGE,"E123.MirrorC")])],"isStart":true});
            var Q818;
            Q818=makeQuery(id+"F2.opExtrude","CAP_EDGE",EDGE,{"disambiguationData":[OSD([sQuery(id+"F0.wireOp",EDGE,"E80.MirrorCS"),sQuery(id+"F0.wireOp",EDGE,"E64.MirrorCS")])],"isStart":true});
            var Q819;
            {var subQ0=sQuery(id+"F0.wireOp",EDGE,"E74.MirrorCS");Q819=makeQuery(id+"F2.opExtrude","CAP_EDGE",EDGE,{"disambiguationData":[OSD([subQ0]),TDD([makeQuery(id+"F0.imprint","IMPRINT",EDGE,{"disambiguationData":[TD([[makeQuery(id+"F0.imprint","INTERSECT",VERTEX,{"derivedFrom":[sQuery(id+"F0.wireOp",EDGE,"E75.MirrorCS"),subQ0]}),-1.0]])],"derivedFrom":subQ0})])],"isStart":true});}
            var Q820;
            Q820=makeQuery(id+"F2.opExtrude","CAP_EDGE",EDGE,{"disambiguationData":[OSD([sQuery(id+"F0.wireOp",EDGE,"E85.MirrorCS")])],"isStart":true});
            var Q821;
            Q821=makeQuery(id+"F2.opExtrude","CAP_EDGE",EDGE,{"disambiguationData":[OSD([sQuery(id+"F0.wireOp",EDGE,"E114.MirrorCS")])],"isStart":true});
            var Q822;
            Q822=makeQuery(id+"F2.opExtrude","CAP_EDGE",EDGE,{"disambiguationData":[OSD([sQuery(id+"F0.wireOp",EDGE,"E95.MirrorCS")])],"isStart":true});
            var Q823;
            Q823=makeQuery(id+"F2.opExtrude","CAP_EDGE",EDGE,{"disambiguationData":[OSD([sQuery(id+"F0.wireOp",EDGE,"E82.MirrorCS")])],"isStart":true});
            var Q824;
            Q824=makeQuery(id+"F2.opExtrude","CAP_EDGE",EDGE,{"disambiguationData":[OSD([sQuery(id+"F0.wireOp",EDGE,"E115.MirrorCS")])],"isStart":true});
            var Q825;
            Q825=makeQuery(id+"F2.opExtrude","CAP_EDGE",EDGE,{"disambiguationData":[OSD([sQuery(id+"F0.wireOp",EDGE,"E121.MirrorCS")])],"isStart":true});
            var Q826;
            Q826=makeQuery(id+"F2.opExtrude","CAP_EDGE",EDGE,{"disambiguationData":[OSD([sQuery(id+"F0.wireOp",EDGE,"E63.MirrorC")])],"isStart":true});
            var Q827;
            Q827=makeQuery(id+"F2.opExtrude","CAP_EDGE",EDGE,{"disambiguationData":[OSD([sQuery(id+"F0.wireOp",EDGE,"E120.MirrorCS")])],"isStart":true});
            var Q828;
            Q828=makeQuery(id+"F2.opExtrude","CAP_EDGE",EDGE,{"disambiguationData":[OSD([sQuery(id+"F0.wireOp",EDGE,"E103.MirrorCS")])],"isStart":true});
            var Q829;
            Q829=makeQuery(id+"F2.opExtrude","CAP_EDGE",EDGE,{"disambiguationData":[OSD([sQuery(id+"F0.wireOp",EDGE,"E84.MirrorCS"),sQuery(id+"F0.wireOp",EDGE,"E98.MirrorCS")])],"isStart":true});
            var Q830;
            Q830=makeQuery(id+"F2.opExtrude","CAP_EDGE",EDGE,{"disambiguationData":[OSD([sQuery(id+"F0.wireOp",EDGE,"E88.MirrorCS")])],"isStart":true});
            var Q831;
            Q831=makeQuery(id+"F2.opExtrude","CAP_EDGE",EDGE,{"disambiguationData":[OSD([sQuery(id+"F0.wireOp",EDGE,"E97.MirrorCS")])],"isStart":true});
            var Q832;
            Q832=makeQuery(id+"F2.opExtrude","CAP_EDGE",EDGE,{"disambiguationData":[OSD([sQuery(id+"F0.wireOp",EDGE,"E117.MirrorCS")])],"isStart":true});
            var Q833;
            Q833=makeQuery(id+"F2.opExtrude","CAP_EDGE",EDGE,{"disambiguationData":[OSD([sQuery(id+"F0.wireOp",EDGE,"E118.MirrorCS")])],"isStart":true});
            var Q834;
            Q834=makeQuery(id+"F2.opExtrude","CAP_EDGE",EDGE,{"disambiguationData":[OSD([sQuery(id+"F0.wireOp",EDGE,"E107.MirrorC")])],"isStart":true});
            var Q835;
            Q835=makeQuery(id+"F2.opExtrude","CAP_EDGE",EDGE,{"disambiguationData":[OSD([sQuery(id+"F0.wireOp",EDGE,"E125.MirrorC")])],"isStart":true});
            var Q836;
            Q836=makeQuery(id+"F2.opExtrude","CAP_EDGE",EDGE,{"disambiguationData":[OSD([sQuery(id+"F0.wireOp",EDGE,"E94.MirrorCS")])],"isStart":true});
            var Q837;
            Q837=makeQuery(id+"F2.opExtrude","CAP_EDGE",EDGE,{"disambiguationData":[OSD([sQuery(id+"F0.wireOp",EDGE,"E78.MirrorC")])],"isStart":true});
            var Q838;
            Q838=makeQuery(id+"F2.opExtrude","CAP_EDGE",EDGE,{"disambiguationData":[OSD([sQuery(id+"F0.wireOp",EDGE,"E89.MirrorCS")])],"isStart":true});
            var Q839;
            Q839=makeQuery(id+"F2.opExtrude","CAP_EDGE",EDGE,{"disambiguationData":[OSD([sQuery(id+"F0.wireOp",EDGE,"E108.MirrorCS")])],"isStart":true});
            var Q840;
            Q840=makeQuery(id+"F2.opExtrude","CAP_EDGE",EDGE,{"disambiguationData":[OSD([sQuery(id+"F0.wireOp",EDGE,"E104.MirrorCS")])],"isStart":true});
            var Q841;
            Q841=makeQuery(id+"F2.opExtrude","CAP_EDGE",EDGE,{"disambiguationData":[OSD([sQuery(id+"F0.wireOp",EDGE,"E126.MirrorC")])],"isStart":true});
            var Q842;
            Q842=makeQuery(id+"F2.opExtrude","CAP_EDGE",EDGE,{"disambiguationData":[OSD([sQuery(id+"F0.wireOp",EDGE,"E93.MirrorCS")])],"isStart":true});
            var Q843;
            Q843=makeQuery(id+"F2.opExtrude","CAP_EDGE",EDGE,{"disambiguationData":[OSD([sQuery(id+"F0.wireOp",EDGE,"E83.MirrorCS")])],"isStart":true});
            var Q844;
            Q844=makeQuery(id+"F2.opExtrude","CAP_EDGE",EDGE,{"disambiguationData":[OSD([sQuery(id+"F0.wireOp",EDGE,"E87.MirrorCS")])],"isStart":true});
            var Q845;
            Q845=makeQuery(id+"F2.opExtrude","CAP_EDGE",EDGE,{"disambiguationData":[OSD([sQuery(id+"F0.wireOp",EDGE,"E116.MirrorCS")])],"isStart":true});
            var Q846;
            Q846=makeQuery(id+"F2.opExtrude","CAP_EDGE",EDGE,{"disambiguationData":[OSD([sQuery(id+"F0.wireOp",EDGE,"E100.MirrorCS")])],"isStart":true});
            var Q847;
            Q847=makeQuery(id+"F2.opExtrude","CAP_EDGE",EDGE,{"disambiguationData":[OSD([sQuery(id+"F0.wireOp",EDGE,"E76.MirrorCS")])],"isStart":true});
            var Q848;
            Q848=makeQuery(id+"F2.opExtrude","CAP_EDGE",EDGE,{"disambiguationData":[OSD([sQuery(id+"F0.wireOp",EDGE,"E70.MirrorCS"),sQuery(id+"F0.wireOp",EDGE,"E106.MirrorCS")])],"isStart":true});
            var Q849;
            Q849=makeQuery(id+"F2.opExtrude","CAP_EDGE",EDGE,{"disambiguationData":[OSD([sQuery(id+"F0.wireOp",EDGE,"E67.MirrorCS"),sQuery(id+"F0.wireOp",EDGE,"E81.MirrorCS")])],"isStart":true});
            var Q850;
            Q850=makeQuery(id+"F2.opExtrude","CAP_EDGE",EDGE,{"disambiguationData":[OSD([sQuery(id+"F0.wireOp",EDGE,"E22")])],"isStart":true});
            var Q851;
            Q851=makeQuery(id+"F2.opExtrude","CAP_EDGE",EDGE,{"disambiguationData":[OSD([sQuery(id+"F0.wireOp",EDGE,"E65.MirrorCS")])],"isStart":true});
            fillet(context, id + "F3", {"entities" : qUnion([Q0, Q1, Q2, Q3, Q4, Q5, Q6, Q7, Q8, Q9, Q10, Q11, Q12, Q13, Q14, Q15, Q16, Q17, Q18, Q19, Q20, Q21, Q22, Q23, Q24, Q25, Q26, Q27, Q28, Q29, Q30, Q31, Q32, Q33, Q34, Q35, Q36, Q37, Q38, Q39, Q40, Q41, Q42, Q43, Q44, Q45, Q46, Q47, Q48, Q49, Q50, Q51, Q52, Q53, Q54, Q55, Q56, Q57, Q58, Q59, Q60, Q61, Q62, Q63, Q64, Q65, Q66, Q67, Q68, Q69, Q70, Q71, Q72, Q73, Q74, Q75, Q76, Q77, Q78, Q79, Q80, Q81, Q82, Q83, Q84, Q85, Q86, Q87, Q88, Q89, Q90, Q91, Q92, Q93, Q94, Q95, Q96, Q97, Q98, Q99, Q100, Q101, Q102, Q103, Q104, Q105, Q106, Q107, Q108, Q109, Q110, Q111, Q112, Q113, Q114, Q115, Q116, Q117, Q118, Q119, Q120, Q121, Q122, Q123, Q124, Q125, Q126, Q127, Q128, Q129, Q130, Q131, Q132, Q133, Q134, Q135, Q136, Q137, Q138, Q139, Q140, Q141, Q142, Q143, Q144, Q145, Q146, Q147, Q148, Q149, Q150, Q151, Q152, Q153, Q154, Q155, Q156, Q157, Q158, Q159, Q160, Q161, Q162, Q163, Q164, Q165, Q166, Q167, Q168, Q169, Q170, Q171, Q172, Q173, Q174, Q175, Q176, Q177, Q178, Q179, Q180, Q181, Q182, Q183, Q184, Q185, Q186, Q187, Q188, Q189, Q190, Q191, Q192, Q193, Q194, Q195, Q196, Q197, Q198, Q199, Q200, Q201, Q202, Q203, Q204, Q205, Q206, Q207, Q208, Q209, Q210, Q211, Q212, Q213, Q214, Q215, Q216, Q217, Q218, Q219, Q220, Q221, Q222, Q223, Q224, Q225, Q226, Q227, Q228, Q229, Q230, Q231, Q232, Q233, Q234, Q235, Q236, Q237, Q238, Q239, Q240, Q241, Q242, Q243, Q244, Q245, Q246, Q247, Q248, Q249, Q250, Q251, Q252, Q253, Q254, Q255, Q256, Q257, Q258, Q259, Q260, Q261, Q262, Q263, Q264, Q265, Q266, Q267, Q268, Q269, Q270, Q271, Q272, Q273, Q274, Q275, Q276, Q277, Q278, Q279, Q280, Q281, Q282, Q283, Q284, Q285, Q286, Q287, Q288, Q289, Q290, Q291, Q292, Q293, Q294, Q295, Q296, Q297, Q298, Q299, Q300, Q301, Q302, Q303, Q304, Q305, Q306, Q307, Q308, Q309, Q310, Q311, Q312, Q313, Q314, Q315, Q316, Q317, Q318, Q319, Q320, Q321, Q322, Q323, Q324, Q325, Q326, Q327, Q328, Q329, Q330, Q331, Q332, Q333, Q334, Q335, Q336, Q337, Q338, Q339, Q340, Q341, Q342, Q343, Q344, Q345, Q346, Q347, Q348, Q349, Q350, Q351, Q352, Q353, Q354, Q355, Q356, Q357, Q358, Q359, Q360, Q361, Q362, Q363, Q364, Q365, Q366, Q367, Q368, Q369, Q370, Q371, Q372, Q373, Q374, Q375, Q376, Q377, Q378, Q379, Q380, Q381, Q382, Q383, Q384, Q385, Q386, Q387, Q388, Q389, Q390, Q391, Q392, Q393, Q394, Q395, Q396, Q397, Q398, Q399, Q400, Q401, Q402, Q403, Q404, Q405, Q406, Q407, Q408, Q409, Q410, Q411, Q412, Q413, Q414, Q415, Q416, Q417, Q418, Q419, Q420, Q421, Q422, Q423, Q424, Q425, Q426, Q427, Q428, Q429, Q430, Q431, Q432, Q433, Q434, Q435, Q436, Q437, Q438, Q439, Q440, Q441, Q442, Q443, Q444, Q445, Q446, Q447, Q448, Q449, Q450, Q451, Q452, Q453, Q454, Q455, Q456, Q457, Q458, Q459, Q460, Q461, Q462, Q463, Q464, Q465, Q466, Q467, Q468, Q469, Q470, Q471, Q472, Q473, Q474, Q475, Q476, Q477, Q478, Q479, Q480, Q481, Q482, Q483, Q484, Q485, Q486, Q487, Q488, Q489, Q490, Q491, Q492, Q493, Q494, Q495, Q496, Q497, Q498, Q499, Q500, Q501, Q502, Q503, Q504, Q505, Q506, Q507, Q508, Q509, Q510, Q511, Q512, Q513, Q514, Q515, Q516, Q517, Q518, Q519, Q520, Q521, Q522, Q523, Q524, Q525, Q526, Q527, Q528, Q529, Q530, Q531, Q532, Q533, Q534, Q535, Q536, Q537, Q538, Q539, Q540, Q541, Q542, Q543, Q544, Q545, Q546, Q547, Q548, Q549, Q550, Q551, Q552, Q553, Q554, Q555, Q556, Q557, Q558, Q559, Q560, Q561, Q562, Q563, Q564, Q565, Q566, Q567, Q568, Q569, Q570, Q571, Q572, Q573, Q574, Q575, Q576, Q577, Q578, Q579, Q580, Q581, Q582, Q583, Q584, Q585, Q586, Q587, Q588, Q589, Q590, Q591, Q592, Q593, Q594, Q595, Q596, Q597, Q598, Q599, Q600, Q601, Q602, Q603, Q604, Q605, Q606, Q607, Q608, Q609, Q610, Q611, Q612, Q613, Q614, Q615, Q616, Q617, Q618, Q619, Q620, Q621, Q622, Q623, Q624, Q625, Q626, Q627, Q628, Q629, Q630, Q631, Q632, Q633, Q634, Q635, Q636, Q637, Q638, Q639, Q640, Q641, Q642, Q643, Q644, Q645, Q646, Q647, Q648, Q649, Q650, Q651, Q652, Q653, Q654, Q655, Q656, Q657, Q658, Q659, Q660, Q661, Q662, Q663, Q664, Q665, Q666, Q667, Q668, Q669, Q670, Q671, Q672, Q673, Q674, Q675, Q676, Q677, Q678, Q679, Q680, Q681, Q682, Q683, Q684, Q685, Q686, Q687, Q688, Q689, Q690, Q691, Q692, Q693, Q694, Q695, Q696, Q697, Q698, Q699, Q700, Q701, Q702, Q703, Q704, Q705, Q706, Q707, Q708, Q709, Q710, Q711, Q712, Q713, Q714, Q715, Q716, Q717, Q718, Q719, Q720, Q721, Q722, Q723, Q724, Q725, Q726, Q727, Q728, Q729, Q730, Q731, Q732, Q733, Q734, Q735, Q736, Q737, Q738, Q739, Q740, Q741, Q742, Q743, Q744, Q745, Q746, Q747, Q748, Q749, Q750, Q751, Q752, Q753, Q754, Q755, Q756, Q757, Q758, Q759, Q760, Q761, Q762, Q763, Q764, Q765, Q766, Q767, Q768, Q769, Q770, Q771, Q772, Q773, Q774, Q775, Q776, Q777, Q778, Q779, Q780, Q781, Q782, Q783, Q784, Q785, Q786, Q787, Q788, Q789, Q790, Q791, Q792, Q793, Q794, Q795, Q796, Q797, Q798, Q799, Q800, Q801, Q802, Q803, Q804, Q805, Q806, Q807, Q808, Q809, Q810, Q811, Q812, Q813, Q814, Q815, Q816, Q817, Q818, Q819, Q820, Q821, Q822, Q823, Q824, Q825, Q826, Q827, Q828, Q829, Q830, Q831, Q832, Q833, Q834, Q835, Q836, Q837, Q838, Q839, Q840, Q841, Q842, Q843, Q844, Q845, Q846, Q847, Q848, Q849, Q850, Q851]), "radius" : 0.25 * mm, "tangentPropagation" : true, "allowEdgeOverflow" : false});
        }
        {
            var Q0;
            Q0=makeQuery(id+"F2.opExtrude","SWEPT_BODY",BODY,{"disambiguationData":[OSD([sQuery(id+"F0.wireOp",EDGE,"E0.1"),sQuery(id+"F0.wireOp",EDGE,"E0.2"),sQuery(id+"F0.wireOp",EDGE,"E0.3"),sQuery(id+"F0.wireOp",EDGE,"E0.4"),sQuery(id+"F0.wireOp",EDGE,"E0.5"),sQuery(id+"F0.wireOp",EDGE,"E1"),sQuery(id+"F0.wireOp",EDGE,"E2"),sQuery(id+"F0.wireOp",EDGE,"E3"),sQuery(id+"F0.wireOp",EDGE,"E4"),sQuery(id+"F0.wireOp",EDGE,"E6"),sQuery(id+"F0.wireOp",EDGE,"E7"),sQuery(id+"F0.wireOp",EDGE,"E8"),sQuery(id+"F0.wireOp",EDGE,"E9"),sQuery(id+"F0.wireOp",EDGE,"E10"),sQuery(id+"F0.wireOp",EDGE,"E11"),sQuery(id+"F0.wireOp",EDGE,"E12"),sQuery(id+"F0.wireOp",EDGE,"E13"),sQuery(id+"F0.wireOp",EDGE,"E14"),sQuery(id+"F0.wireOp",EDGE,"E15"),sQuery(id+"F0.wireOp",EDGE,"E16"),sQuery(id+"F0.wireOp",EDGE,"E17"),sQuery(id+"F0.wireOp",EDGE,"E18"),sQuery(id+"F0.wireOp",EDGE,"E19"),sQuery(id+"F0.wireOp",EDGE,"E20"),sQuery(id+"F0.wireOp",EDGE,"E21"),sQuery(id+"F0.wireOp",EDGE,"E22"),sQuery(id+"F0.wireOp",EDGE,"E24.trimOffspring"),sQuery(id+"F0.wireOp",EDGE,"E26"),sQuery(id+"F0.wireOp",EDGE,"E27"),sQuery(id+"F0.wireOp",EDGE,"E28"),sQuery(id+"F0.wireOp",EDGE,"E29"),sQuery(id+"F0.wireOp",EDGE,"E30"),sQuery(id+"F0.wireOp",EDGE,"E31"),sQuery(id+"F0.wireOp",EDGE,"E32"),sQuery(id+"F0.wireOp",EDGE,"E33"),sQuery(id+"F0.wireOp",EDGE,"E34"),sQuery(id+"F0.wireOp",EDGE,"E35.0"),sQuery(id+"F0.wireOp",EDGE,"E36.0"),sQuery(id+"F0.wireOp",EDGE,"E37.0"),sQuery(id+"F0.wireOp",EDGE,"E38.0"),sQuery(id+"F0.wireOp",EDGE,"E39.0"),sQuery(id+"F0.wireOp",EDGE,"E40.0"),sQuery(id+"F0.wireOp",EDGE,"E41"),sQuery(id+"F0.wireOp",EDGE,"E42"),sQuery(id+"F0.wireOp",EDGE,"E43"),sQuery(id+"F0.wireOp",EDGE,"E44"),sQuery(id+"F0.wireOp",EDGE,"E45"),sQuery(id+"F0.wireOp",EDGE,"E46"),sQuery(id+"F0.wireOp",EDGE,"E47.0"),sQuery(id+"F0.wireOp",EDGE,"E48.0"),sQuery(id+"F0.wireOp",EDGE,"E49.0"),sQuery(id+"F0.wireOp",EDGE,"E50.0"),sQuery(id+"F0.wireOp",EDGE,"E51.0"),sQuery(id+"F0.wireOp",EDGE,"E52"),sQuery(id+"F0.wireOp",EDGE,"E53"),sQuery(id+"F0.wireOp",EDGE,"E54"),sQuery(id+"F0.wireOp",EDGE,"E55.trimOffspring"),sQuery(id+"F0.wireOp",EDGE,"E56"),sQuery(id+"F0.wireOp",EDGE,"E57.trimOffspring"),sQuery(id+"F0.wireOp",EDGE,"E58"),sQuery(id+"F0.wireOp",EDGE,"E59"),sQuery(id+"F0.wireOp",EDGE,"E60"),sQuery(id+"F0.wireOp",EDGE,"E61.trimOffspring"),sQuery(id+"F0.wireOp",EDGE,"E62.trimOffspring")])]});
            deleteBodies(context, id + "F4", {"entities" : qUnion([Q0])});
        }
        {
            var Q0;
            Q0=makeQuery(id+"F2.opExtrude","SWEPT_BODY",BODY,{"disambiguationData":[OSD([sQuery(id+"F0.wireOp",EDGE,"E73.MirrorCS"),sQuery(id+"F0.wireOp",EDGE,"E68.MirrorCS"),sQuery(id+"F0.wireOp",EDGE,"E69.MirrorCS"),sQuery(id+"F0.wireOp",EDGE,"E89.MirrorCS"),sQuery(id+"F0.wireOp",EDGE,"E77.MirrorCS"),sQuery(id+"F0.wireOp",EDGE,"E67.MirrorCS"),sQuery(id+"F0.wireOp",EDGE,"E84.MirrorCS"),sQuery(id+"F0.wireOp",EDGE,"E85.MirrorCS"),sQuery(id+"F0.wireOp",EDGE,"E72.MirrorCS"),sQuery(id+"F0.wireOp",EDGE,"E91.MirrorC"),sQuery(id+"F0.wireOp",EDGE,"E75.MirrorCS"),sQuery(id+"F0.wireOp",EDGE,"E82.MirrorCS"),sQuery(id+"F0.wireOp",EDGE,"E87.MirrorCS"),sQuery(id+"F0.wireOp",EDGE,"E79.MirrorCS"),sQuery(id+"F0.wireOp",EDGE,"E78.MirrorC"),sQuery(id+"F0.wireOp",EDGE,"E70.MirrorCS"),sQuery(id+"F0.wireOp",EDGE,"E66.MirrorCS"),sQuery(id+"F0.wireOp",EDGE,"E80.MirrorCS"),sQuery(id+"F0.wireOp",EDGE,"E88.MirrorCS"),sQuery(id+"F0.wireOp",EDGE,"E86.MirrorC"),sQuery(id+"F0.wireOp",EDGE,"E65.MirrorCS"),sQuery(id+"F0.wireOp",EDGE,"E71.MirrorCS"),sQuery(id+"F0.wireOp",EDGE,"E83.MirrorCS"),sQuery(id+"F0.wireOp",EDGE,"E90.MirrorCS"),sQuery(id+"F0.wireOp",EDGE,"E76.MirrorCS"),sQuery(id+"F0.wireOp",EDGE,"E92.MirrorCS"),sQuery(id+"F0.wireOp",EDGE,"E63.MirrorC"),sQuery(id+"F0.wireOp",EDGE,"E64.MirrorCS"),sQuery(id+"F0.wireOp",EDGE,"E74.MirrorCS"),sQuery(id+"F0.wireOp",EDGE,"E96.MirrorCS"),sQuery(id+"F0.wireOp",EDGE,"E95.MirrorCS"),sQuery(id+"F0.wireOp",EDGE,"E93.MirrorCS"),sQuery(id+"F0.wireOp",EDGE,"E98.MirrorCS"),sQuery(id+"F0.wireOp",EDGE,"E94.MirrorCS"),sQuery(id+"F0.wireOp",EDGE,"E100.MirrorCS"),sQuery(id+"F0.wireOp",EDGE,"E97.MirrorCS"),sQuery(id+"F0.wireOp",EDGE,"E103.MirrorCS"),sQuery(id+"F0.wireOp",EDGE,"E113.MirrorCS"),sQuery(id+"F0.wireOp",EDGE,"E99.MirrorC"),sQuery(id+"F0.wireOp",EDGE,"E102.MirrorCS"),sQuery(id+"F0.wireOp",EDGE,"E106.MirrorCS"),sQuery(id+"F0.wireOp",EDGE,"E126.MirrorC"),sQuery(id+"F0.wireOp",EDGE,"E125.MirrorC"),sQuery(id+"F0.wireOp",EDGE,"E116.MirrorCS"),sQuery(id+"F0.wireOp",EDGE,"E115.MirrorCS"),sQuery(id+"F0.wireOp",EDGE,"E110.MirrorCS"),sQuery(id+"F0.wireOp",EDGE,"E101.MirrorCS"),sQuery(id+"F0.wireOp",EDGE,"E111.MirrorCS"),sQuery(id+"F0.wireOp",EDGE,"E119.MirrorCS"),sQuery(id+"F0.wireOp",EDGE,"E114.MirrorCS"),sQuery(id+"F0.wireOp",EDGE,"E104.MirrorCS"),sQuery(id+"F0.wireOp",EDGE,"E109.MirrorCS"),sQuery(id+"F0.wireOp",EDGE,"E105.MirrorCS"),sQuery(id+"F0.wireOp",EDGE,"E81.MirrorCS"),sQuery(id+"F0.wireOp",EDGE,"E120.MirrorCS"),sQuery(id+"F0.wireOp",EDGE,"E123.MirrorC"),sQuery(id+"F0.wireOp",EDGE,"E124.MirrorCS"),sQuery(id+"F0.wireOp",EDGE,"E122.MirrorCS"),sQuery(id+"F0.wireOp",EDGE,"E121.MirrorCS"),sQuery(id+"F0.wireOp",EDGE,"E108.MirrorCS"),sQuery(id+"F0.wireOp",EDGE,"E107.MirrorC"),sQuery(id+"F0.wireOp",EDGE,"E112.MirrorCS"),sQuery(id+"F0.wireOp",EDGE,"E118.MirrorCS"),sQuery(id+"F0.wireOp",EDGE,"E117.MirrorCS")])]});
            deleteBodies(context, id + "F5", {"entities" : qUnion([Q0])});
        }
    });
